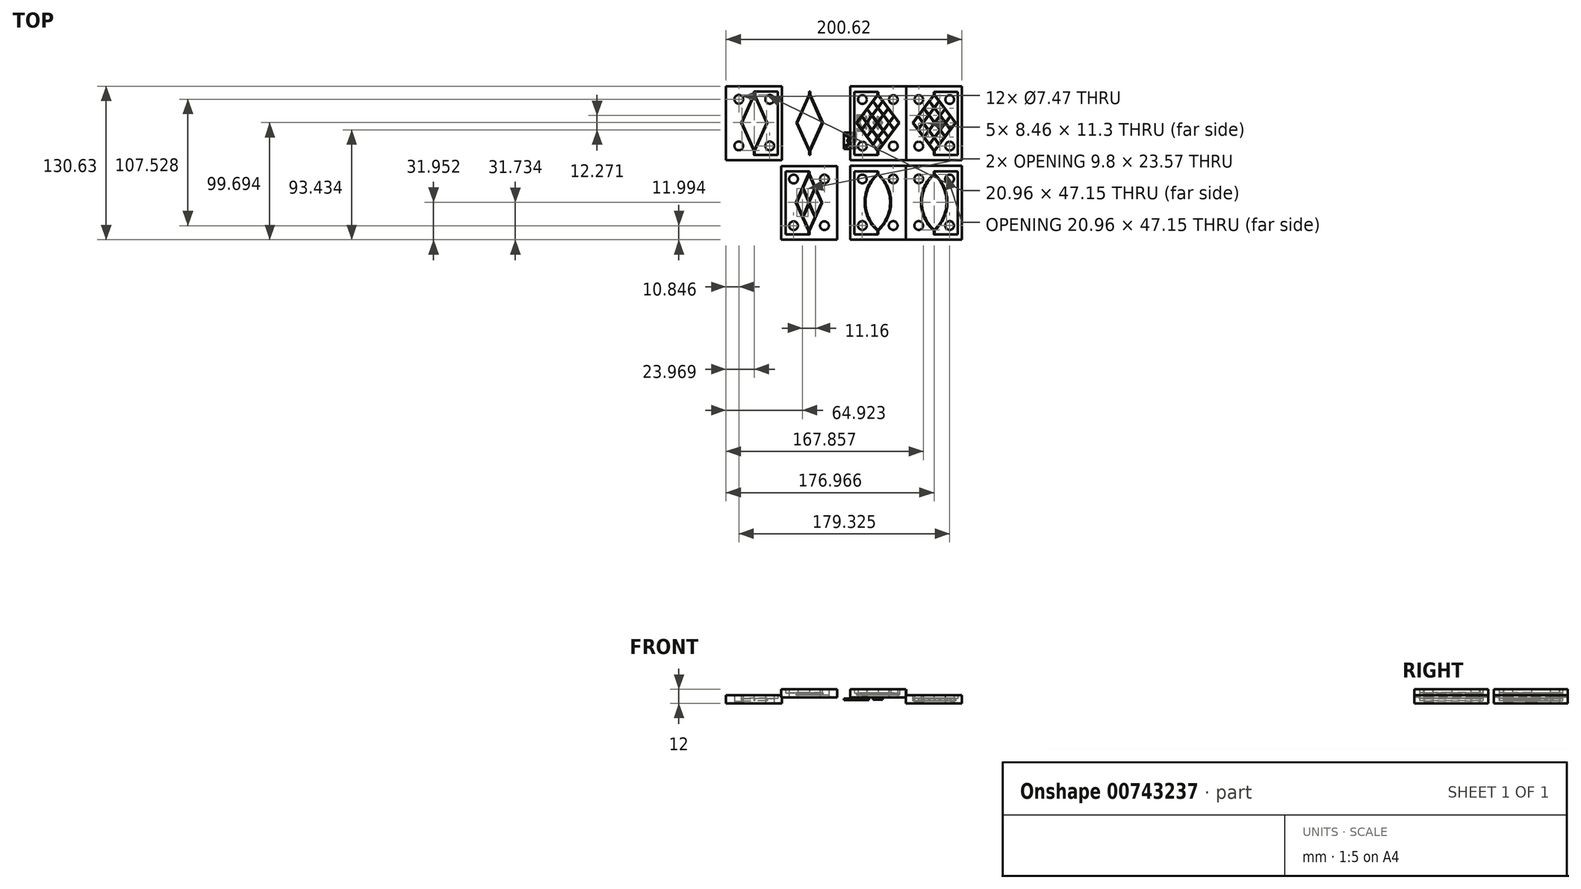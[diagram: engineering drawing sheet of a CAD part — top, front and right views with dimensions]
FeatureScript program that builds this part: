
annotation { "Feature Type Name" : "Feature", "Feature Type Description" : "" }
export const myFeature = defineFeature(function(context is Context, id is Id, definition is map)
    precondition{}
    {
        {
            var Q0;
            Q0=qCreatedBy(makeId("Top.planeOp"),FACE);
            var sketch = newSketch(context, id + "F0", { "sketchPlane" : qUnion([Q0])});
            skLineSegment(sketch, "E0.bottom", {"start": v(-19.96, 26.4) * mm, "end": v(20.09, 26.4) * mm});
            skLineSegment(sketch, "E0.top", {"start": v(-19.96, -27.38) * mm, "end": v(20.09, -27.38) * mm});
            skLineSegment(sketch, "E0.left", {"start": v(-19.96, 26.4) * mm, "end": v(-19.96, -27.38) * mm});
            skLineSegment(sketch, "E0.right", {"start": v(20.09, 26.4) * mm, "end": v(20.09, -27.38) * mm});
            skLineSegment(sketch, "E1.bottom", {"start": v(-23.57, 30.94) * mm, "end": v(23.97, 30.94) * mm});
            skLineSegment(sketch, "E1.top", {"start": v(-23.57, -31.82) * mm, "end": v(23.97, -31.82) * mm});
            skLineSegment(sketch, "E1.left", {"start": v(-23.57, 30.94) * mm, "end": v(-23.57, -31.82) * mm});
            skLineSegment(sketch, "E1.right", {"start": v(23.97, 30.94) * mm, "end": v(23.97, -31.82) * mm});
            skPoint(sketch, "E2.startSnap0", {"position": v(-19.96, -0.48) * mm});
            skLineSegment(sketch, "E3", {"start": v(-13.42, 5.65) * mm, "end": v(-9.19, 11.3) * mm});
            skLineSegment(sketch, "E4", {"start": v(-9.19, 11.3) * mm, "end": v(-5.32, 6.14) * mm});
            skLineSegment(sketch, "E5", {"start": v(-5.32, 6.14) * mm, "end": v(-9.55, 0.48) * mm});
            skLineSegment(sketch, "E6", {"start": v(-17.65, 0) * mm, "end": v(-13.78, 5.17) * mm});
            skLineSegment(sketch, "E7", {"start": v(0, 23.57) * mm, "end": v(-3.87, 18.4) * mm});
            skLineSegment(sketch, "E8", {"start": v(-4.23, 17.92) * mm, "end": v(-8.83, 11.79) * mm});
            skLineSegment(sketch, "E9", {"start": v(-13.78, -5.17) * mm, "end": v(-9.92, 0) * mm});
            skPoint(sketch, "E10.endSnap0", {"position": v(-4.96, 6.62) * mm});
            skLineSegment(sketch, "E11", {"start": v(0, 13.24) * mm, "end": v(3.87, 18.4) * mm});
            skLineSegment(sketch, "E12", {"start": v(-4.96, 6.62) * mm, "end": v(-0.36, 12.76) * mm});
            skLineSegment(sketch, "E13", {"start": v(-13.42, -5.65) * mm, "end": v(-9.55, -0.48) * mm});
            skLineSegment(sketch, "E14", {"start": v(-9.55, -0.48) * mm, "end": v(-5.32, -6.14) * mm});
            skLineSegment(sketch, "E15", {"start": v(-5.32, -6.14) * mm, "end": v(-9.19, -11.3) * mm});
            skLineSegment(sketch, "E16", {"start": v(-9.19, -11.3) * mm, "end": v(-13.42, -5.65) * mm});
            skLineSegment(sketch, "E17", {"start": v(-4.96, -5.65) * mm, "end": v(-0.73, 0) * mm});
            skLineSegment(sketch, "E18", {"start": v(-0.73, 0) * mm, "end": v(-4.96, 5.65) * mm});
            skLineSegment(sketch, "E19", {"start": v(-4.96, 5.65) * mm, "end": v(-9.19, 0) * mm});
            skLineSegment(sketch, "E20", {"start": v(-9.19, 0) * mm, "end": v(-4.96, -5.65) * mm});
            skLineSegment(sketch, "E21", {"start": v(4.23, 6.62) * mm, "end": v(0, 12.27) * mm});
            skLineSegment(sketch, "E22", {"start": v(0, 12.27) * mm, "end": v(-4.6, 6.14) * mm});
            skLineSegment(sketch, "E23", {"start": v(-4.6, 6.14) * mm, "end": v(-0.36, 0.48) * mm});
            skLineSegment(sketch, "E24", {"start": v(-0.36, 0.48) * mm, "end": v(4.23, 6.62) * mm});
            skLineSegment(sketch, "E25", {"start": v(4.6, 7.1) * mm, "end": v(8.46, 12.27) * mm});
            skLineSegment(sketch, "E26", {"start": v(8.46, 12.27) * mm, "end": v(4.23, 17.92) * mm});
            skLineSegment(sketch, "E27", {"start": v(4.23, 17.92) * mm, "end": v(0.36, 12.76) * mm});
            skLineSegment(sketch, "E28", {"start": v(0.36, 12.76) * mm, "end": v(4.6, 7.1) * mm});
            skLineSegment(sketch, "E29", {"start": v(-4.23, -17.92) * mm, "end": v(-0.36, -12.76) * mm});
            skLineSegment(sketch, "E30", {"start": v(-0.36, -12.76) * mm, "end": v(-4.96, -6.62) * mm});
            skLineSegment(sketch, "E31", {"start": v(-8.83, -11.79) * mm, "end": v(-4.96, -6.62) * mm});
            skLineSegment(sketch, "E32", {"start": v(-8.83, -11.79) * mm, "end": v(-4.23, -17.92) * mm});
            skLineSegment(sketch, "E33", {"start": v(0, -12.27) * mm, "end": v(-4.6, -6.14) * mm});
            skLineSegment(sketch, "E34", {"start": v(-0.36, -0.48) * mm, "end": v(-4.6, -6.14) * mm});
            skLineSegment(sketch, "E35", {"start": v(4.23, -6.62) * mm, "end": v(-0.36, -0.48) * mm});
            skLineSegment(sketch, "E36", {"start": v(4.23, -6.62) * mm, "end": v(0, -12.27) * mm});
            skLineSegment(sketch, "E37", {"start": v(9.19, 0) * mm, "end": v(4.6, 6.14) * mm});
            skLineSegment(sketch, "E38", {"start": v(4.6, 6.14) * mm, "end": v(0, 0) * mm});
            skLineSegment(sketch, "E39", {"start": v(0, 0) * mm, "end": v(4.6, -6.14) * mm});
            skLineSegment(sketch, "E40", {"start": v(4.6, -6.14) * mm, "end": v(9.19, 0) * mm});
            skLineSegment(sketch, "E41", {"start": v(4.96, 6.62) * mm, "end": v(8.83, 11.79) * mm});
            skLineSegment(sketch, "E42", {"start": v(8.83, 11.79) * mm, "end": v(13.42, 5.65) * mm});
            skLineSegment(sketch, "E43", {"start": v(13.42, 5.65) * mm, "end": v(9.55, 0.48) * mm});
            skLineSegment(sketch, "E44", {"start": v(9.55, 0.48) * mm, "end": v(4.96, 6.62) * mm});
            skLineSegment(sketch, "E45", {"start": v(-3.87, -18.4) * mm, "end": v(0, -13.24) * mm});
            skLineSegment(sketch, "E46", {"start": v(0, -13.24) * mm, "end": v(3.87, -18.4) * mm});
            skLineSegment(sketch, "E47", {"start": v(3.87, -18.4) * mm, "end": v(0, -23.57) * mm});
            skLineSegment(sketch, "E48", {"start": v(0, -23.57) * mm, "end": v(-3.87, -18.4) * mm});
            skLineSegment(sketch, "E49", {"start": v(4.23, -17.92) * mm, "end": v(8.46, -12.27) * mm});
            skLineSegment(sketch, "E50", {"start": v(8.46, -12.27) * mm, "end": v(4.6, -7.1) * mm});
            skLineSegment(sketch, "E51", {"start": v(4.6, -7.1) * mm, "end": v(0.36, -12.76) * mm});
            skLineSegment(sketch, "E52", {"start": v(0.36, -12.76) * mm, "end": v(4.23, -17.92) * mm});
            skLineSegment(sketch, "E53", {"start": v(8.83, -11.79) * mm, "end": v(4.96, -6.62) * mm});
            skLineSegment(sketch, "E54", {"start": v(4.96, -6.62) * mm, "end": v(9.55, -0.48) * mm});
            skLineSegment(sketch, "E55", {"start": v(9.55, -0.48) * mm, "end": v(13.42, -5.65) * mm});
            skLineSegment(sketch, "E56", {"start": v(13.42, -5.65) * mm, "end": v(8.83, -11.79) * mm});
            skLineSegment(sketch, "E57", {"start": v(17.65, 0) * mm, "end": v(13.78, 5.17) * mm});
            skLineSegment(sketch, "E58", {"start": v(13.78, 5.17) * mm, "end": v(9.92, 0) * mm});
            skLineSegment(sketch, "E59", {"start": v(9.92, 0) * mm, "end": v(13.78, -5.17) * mm});
            skLineSegment(sketch, "E60", {"start": v(13.78, -5.17) * mm, "end": v(17.65, 0) * mm});
            skLineSegment(sketch, "E61", {"start": v(0, 13.24) * mm, "end": v(-3.87, 18.4) * mm});
            skLineSegment(sketch, "E62", {"start": v(3.87, 18.4) * mm, "end": v(0, 23.57) * mm});
            skLineSegment(sketch, "E63", {"start": v(-0.36, 12.76) * mm, "end": v(-4.23, 17.92) * mm});
            skLineSegment(sketch, "E64", {"start": v(-13.78, -5.17) * mm, "end": v(-17.65, 0) * mm});
            skLineSegment(sketch, "E65", {"start": v(-9.92, 0) * mm, "end": v(-13.78, 5.17) * mm});
            skLineSegment(sketch, "E66", {"start": v(-9.55, 0.48) * mm, "end": v(-13.42, 5.65) * mm});
            skLineSegment(sketch, "E67", {"start": v(-4.96, 6.62) * mm, "end": v(-8.83, 11.79) * mm});
            skLineSegment(sketch, "E68", {"start": v(0.36, 24.06) * mm, "end": v(18.38, 0) * mm});
            skLineSegment(sketch, "E69", {"start": v(-18.38, 0) * mm, "end": v(-0.36, 24.06) * mm});
            skLineSegment(sketch, "E70.MirrorCS", {"start": v(-18.38, 0) * mm, "end": v(-0.36, -24.06) * mm});
            skLineSegment(sketch, "E71.MirrorCS", {"start": v(0.36, -24.06) * mm, "end": v(18.38, 0) * mm});
            skLineSegment(sketch, "E72", {"start": v(-0.36, -24.06) * mm, "end": v(-0.36, -27.38) * mm});
            skLineSegment(sketch, "E73", {"start": v(0.36, -24.06) * mm, "end": v(0.36, -27.38) * mm});
            skLineSegment(sketch, "E74", {"start": v(-0.36, 24.06) * mm, "end": v(-0.36, 26.4) * mm});
            skLineSegment(sketch, "E75", {"start": v(0.36, 24.06) * mm, "end": v(0.36, 26.4) * mm});
            skCircle(sketch, "E76", {"center": v(-13.12, 19.83) * mm, "radius": 3.73 * mm});
            skCircle(sketch, "E77.MirrorC", {"center": v(13.12, 19.83) * mm, "radius": 3.73 * mm});
            skCircle(sketch, "E78.MirrorC", {"center": v(-13.12, -19.83) * mm, "radius": 3.73 * mm});
            skCircle(sketch, "E79.MirrorC", {"center": v(13.12, -19.83) * mm, "radius": 3.73 * mm});
            skLineSegment(sketch, "E80.bottom", {"start": v(-77.96, 26.53) * mm, "end": v(-37.9, 26.53) * mm});
            skLineSegment(sketch, "E80.top", {"start": v(-77.96, -27.25) * mm, "end": v(-37.9, -27.25) * mm});
            skLineSegment(sketch, "E80.left", {"start": v(-77.96, 26.53) * mm, "end": v(-77.96, -27.25) * mm});
            skLineSegment(sketch, "E80.right", {"start": v(-37.9, 26.53) * mm, "end": v(-37.9, -27.25) * mm});
            skLineSegment(sketch, "E81.bottom", {"start": v(-81.56, 31.06) * mm, "end": v(-34.02, 31.06) * mm});
            skLineSegment(sketch, "E81.top", {"start": v(-81.56, -31.7) * mm, "end": v(-34.02, -31.7) * mm});
            skLineSegment(sketch, "E81.left", {"start": v(-81.56, 31.06) * mm, "end": v(-81.56, -31.7) * mm});
            skLineSegment(sketch, "E81.right", {"start": v(-34.02, 31.06) * mm, "end": v(-34.02, -31.7) * mm});
            skPoint(sketch, "E82.startSnap0", {"position": v(-77.96, -0.36) * mm});
            skLineSegment(sketch, "E83.MirrorCS", {"start": v(-69.2, -0.05) * mm, "end": v(-58.36, -23.93) * mm});
            skLineSegment(sketch, "E84", {"start": v(-58.36, -23.93) * mm, "end": v(-58.36, -27.25) * mm});
            skLineSegment(sketch, "E85", {"start": v(-57.63, -23.93) * mm, "end": v(-57.63, -27.25) * mm});
            skLineSegment(sketch, "E86", {"start": v(-58.36, 24.18) * mm, "end": v(-58.36, 26.53) * mm});
            skLineSegment(sketch, "E87", {"start": v(-57.63, 24.18) * mm, "end": v(-57.63, 26.53) * mm});
            skCircle(sketch, "E88", {"center": v(-71.12, 19.95) * mm, "radius": 3.73 * mm});
            skCircle(sketch, "E89.MirrorC", {"center": v(-44.87, 19.95) * mm, "radius": 3.73 * mm});
            skCircle(sketch, "E90.MirrorC", {"center": v(-71.12, -19.7) * mm, "radius": 3.73 * mm});
            skCircle(sketch, "E91.MirrorC", {"center": v(-44.87, -19.7) * mm, "radius": 3.73 * mm});
            skLineSegment(sketch, "E92", {"start": v(-69.2, -0.05) * mm, "end": v(-58.36, 24.18) * mm});
            skLineSegment(sketch, "E93.MirrorCS", {"start": v(-46.79, -0.05) * mm, "end": v(-57.63, 24.18) * mm});
            skLineSegment(sketch, "E94.MirrorCS", {"start": v(-47.52, -0.05) * mm, "end": v(-58, 23.7) * mm});
            skLineSegment(sketch, "E95.MirrorCS", {"start": v(-46.79, -0.05) * mm, "end": v(-57.63, -23.93) * mm});
            skLineSegment(sketch, "E96.MirrorCS", {"start": v(-47.52, -0.05) * mm, "end": v(-58, -23.45) * mm});
            skLineSegment(sketch, "E97.MirrorCS", {"start": v(-68.47, -0.05) * mm, "end": v(-58, 23.7) * mm});
            skLineSegment(sketch, "E98.MirrorCS", {"start": v(-68.47, -0.05) * mm, "end": v(-58, -23.45) * mm});
            skLineSegment(sketch, "E99.bottom", {"start": v(-78.56, -41.34) * mm, "end": v(-38.5, -41.34) * mm});
            skLineSegment(sketch, "E99.top", {"start": v(-78.56, -95.12) * mm, "end": v(-38.5, -95.12) * mm});
            skLineSegment(sketch, "E99.left", {"start": v(-78.56, -41.34) * mm, "end": v(-78.56, -95.12) * mm});
            skLineSegment(sketch, "E99.right", {"start": v(-38.5, -41.34) * mm, "end": v(-38.5, -95.12) * mm});
            skLineSegment(sketch, "E100.bottom", {"start": v(-82.17, -36.8) * mm, "end": v(-34.62, -36.8) * mm});
            skLineSegment(sketch, "E100.top", {"start": v(-82.17, -99.57) * mm, "end": v(-34.62, -99.57) * mm});
            skLineSegment(sketch, "E100.left", {"start": v(-82.17, -36.8) * mm, "end": v(-82.17, -99.57) * mm});
            skLineSegment(sketch, "E100.right", {"start": v(-34.62, -36.8) * mm, "end": v(-34.62, -99.57) * mm});
            skPoint(sketch, "E101.startSnap0", {"position": v(-78.56, -68.23) * mm});
            skLineSegment(sketch, "E102.MirrorCS", {"start": v(-69.8, -67.93) * mm, "end": v(-58.96, -91.8) * mm});
            skLineSegment(sketch, "E103", {"start": v(-58.96, -91.8) * mm, "end": v(-58.96, -95.12) * mm});
            skLineSegment(sketch, "E104", {"start": v(-58.23, -91.8) * mm, "end": v(-58.23, -95.12) * mm});
            skLineSegment(sketch, "E105", {"start": v(-58.96, -43.69) * mm, "end": v(-58.96, -41.34) * mm});
            skLineSegment(sketch, "E106", {"start": v(-58.23, -43.69) * mm, "end": v(-58.23, -41.34) * mm});
            skCircle(sketch, "E107", {"center": v(-71.72, -47.92) * mm, "radius": 3.73 * mm});
            skCircle(sketch, "E108.MirrorC", {"center": v(-45.47, -47.92) * mm, "radius": 3.73 * mm});
            skCircle(sketch, "E109.MirrorC", {"center": v(-71.72, -87.58) * mm, "radius": 3.73 * mm});
            skCircle(sketch, "E110.MirrorC", {"center": v(-45.47, -87.58) * mm, "radius": 3.73 * mm});
            skLineSegment(sketch, "E111", {"start": v(-69.8, -67.93) * mm, "end": v(-58.96, -43.69) * mm});
            skLineSegment(sketch, "E112.MirrorCS", {"start": v(-47.4, -67.93) * mm, "end": v(-58.23, -43.69) * mm});
            skLineSegment(sketch, "E113.MirrorCS", {"start": v(-47.4, -67.93) * mm, "end": v(-58.23, -91.8) * mm});
            skLineSegment(sketch, "E114", {"start": v(-58.6, -66.3) * mm, "end": v(-53.68, -55.31) * mm});
            skLineSegment(sketch, "E115", {"start": v(-53.68, -55.31) * mm, "end": v(-58.6, -44.17) * mm});
            skLineSegment(sketch, "E116", {"start": v(-58.6, -66.3) * mm, "end": v(-63.51, -55.31) * mm});
            skLineSegment(sketch, "E117", {"start": v(-63.51, -55.31) * mm, "end": v(-58.6, -44.17) * mm});
            skLineSegment(sketch, "E118", {"start": v(-53.36, -56.05) * mm, "end": v(-48.12, -67.93) * mm});
            skLineSegment(sketch, "E119", {"start": v(-63.84, -56.05) * mm, "end": v(-69.08, -67.93) * mm});
            skLineSegment(sketch, "E120", {"start": v(-58.6, -91.32) * mm, "end": v(-63.51, -80.35) * mm});
            skLineSegment(sketch, "E121", {"start": v(-63.51, -80.35) * mm, "end": v(-58.6, -69.52) * mm});
            skLineSegment(sketch, "E122", {"start": v(-58.6, -69.52) * mm, "end": v(-53.68, -80.35) * mm});
            skLineSegment(sketch, "E123", {"start": v(-53.68, -80.35) * mm, "end": v(-58.6, -91.32) * mm});
            skLineSegment(sketch, "E124", {"start": v(-69.08, -67.93) * mm, "end": v(-63.84, -79.62) * mm});
            skLineSegment(sketch, "E125", {"start": v(-53.36, -79.62) * mm, "end": v(-48.12, -67.93) * mm});
            skLineSegment(sketch, "E126.left", {"start": v(-57.92, -66.3) * mm, "end": v(-57.92, -69.37) * mm});
            skLineSegment(sketch, "E126.right", {"start": v(-59.28, -66.3) * mm, "end": v(-59.28, -69.37) * mm});
            skLineSegment(sketch, "E127", {"start": v(-63.84, -56.05) * mm, "end": v(-59.28, -66.3) * mm});
            skLineSegment(sketch, "E128", {"start": v(-57.92, -66.3) * mm, "end": v(-53.36, -56.05) * mm});
            skLineSegment(sketch, "E129", {"start": v(-57.92, -69.37) * mm, "end": v(-53.36, -79.62) * mm});
            skLineSegment(sketch, "E130", {"start": v(-59.28, -69.37) * mm, "end": v(-63.84, -79.62) * mm});
            skLineSegment(sketch, "E131.bottom", {"start": v(-20.04, -41.21) * mm, "end": v(20, -41.21) * mm});
            skLineSegment(sketch, "E131.top", {"start": v(-20.04, -95) * mm, "end": v(20, -95) * mm});
            skLineSegment(sketch, "E131.left", {"start": v(-20.04, -41.21) * mm, "end": v(-20.04, -95) * mm});
            skLineSegment(sketch, "E131.right", {"start": v(20, -41.21) * mm, "end": v(20, -95) * mm});
            skLineSegment(sketch, "E132.bottom", {"start": v(-23.65, -36.68) * mm, "end": v(23.9, -36.68) * mm});
            skLineSegment(sketch, "E132.top", {"start": v(-23.65, -99.44) * mm, "end": v(23.9, -99.44) * mm});
            skLineSegment(sketch, "E132.left", {"start": v(-23.65, -36.68) * mm, "end": v(-23.65, -99.44) * mm});
            skLineSegment(sketch, "E132.right", {"start": v(23.9, -36.68) * mm, "end": v(23.9, -99.44) * mm});
            skPoint(sketch, "E133.startSnap0", {"position": v(-20.04, -68.1) * mm});
            skLineSegment(sketch, "E134", {"start": v(-0.44, -91.68) * mm, "end": v(-0.44, -95) * mm});
            skLineSegment(sketch, "E135", {"start": v(0.28, -91.68) * mm, "end": v(0.28, -95) * mm});
            skLineSegment(sketch, "E136", {"start": v(-0.44, -43.56) * mm, "end": v(-0.44, -41.21) * mm});
            skLineSegment(sketch, "E137", {"start": v(0.28, -43.56) * mm, "end": v(0.28, -41.21) * mm});
            skCircle(sketch, "E138", {"center": v(-13.2, -47.79) * mm, "radius": 3.73 * mm});
            skCircle(sketch, "E139.MirrorC", {"center": v(13.04, -47.79) * mm, "radius": 3.73 * mm});
            skCircle(sketch, "E140.MirrorC", {"center": v(-13.2, -87.45) * mm, "radius": 3.73 * mm});
            skCircle(sketch, "E141.MirrorC", {"center": v(13.04, -87.45) * mm, "radius": 3.73 * mm});
            skArc(sketch, "E142", {"start": v(-0.44, -43.56) * mm, "mid": v(-11.29, -67.62) * mm, "end": v(-0.44, -91.68) * mm});
            skArc(sketch, "E143", {"start": v(-0.08, -44.04) * mm, "mid": v(-10.56, -67.62) * mm, "end": v(-0.08, -91.2) * mm});
            skArc(sketch, "E144", {"start": v(0.28, -91.68) * mm, "mid": v(11.12, -67.62) * mm, "end": v(0.28, -43.56) * mm});
            skArc(sketch, "E145", {"start": v(-0.08, -91.2) * mm, "mid": v(10.4, -67.62) * mm, "end": v(-0.08, -44.04) * mm});
            skSolve(sketch);
        }
        {
            var Q0;
            Q0=makeQuery(id+"F0.imprint","IMPRINT",FACE,{"disambiguationData":[TD([[makeQuery(id+"F0.imprint","IMPRINT",EDGE,{"derivedFrom":sQuery(id+"F0.wireOp",EDGE,"E3")}),1.0]])]});
            var Q1;
            Q1=makeQuery(id+"F0.imprint","IMPRINT",FACE,{"disambiguationData":[TD([[makeQuery(id+"F0.imprint","IMPRINT",EDGE,{"derivedFrom":sQuery(id+"F0.wireOp",EDGE,"E83.MirrorCS")}),1.0]])]});
            var Q2;
            Q2=makeQuery(id+"F0.imprint","IMPRINT",FACE,{"disambiguationData":[TD([[makeQuery(id+"F0.imprint","IMPRINT",EDGE,{"derivedFrom":sQuery(id+"F0.wireOp",EDGE,"E102.MirrorCS")}),1.0]])]});
            var Q3;
            {var subQ1=sQuery(id+"F0.wireOp",EDGE,"E134");Q3=makeQuery(id+"F0.imprint","IMPRINT",FACE,{"disambiguationData":[TD([[makeQuery(id+"F0.imprint","IMPRINT",EDGE,{"derivedFrom":subQ1}),1.0]])]});}
            extrude(context, id + "F1", {"entities" : qUnion([Q0, Q1, Q2, Q3]), "depth" : .3 * mm, "offsetDistance" : 25 * mm});
        }
        {
            var Q0;
            Q0=makeQuery(id+"F0.imprint","IMPRINT",FACE,{"disambiguationData":[TD([[makeQuery(id+"F0.imprint","IMPRINT",EDGE,{"derivedFrom":sQuery(id+"F0.wireOp",EDGE,"E0.bottom")}),1.0]])]});
            var Q1;
            Q1=makeQuery(id+"F0.imprint","IMPRINT",FACE,{"disambiguationData":[TD([[makeQuery(id+"F0.imprint","IMPRINT",EDGE,{"derivedFrom":sQuery(id+"F0.wireOp",EDGE,"E76")}),1.0]])]});
            var Q2;
            Q2=makeQuery(id+"F0.imprint","IMPRINT",FACE,{"disambiguationData":[TD([[makeQuery(id+"F0.imprint","IMPRINT",EDGE,{"derivedFrom":sQuery(id+"F0.wireOp",EDGE,"edaaeaec-2fa2-4ac8-96e5-24b6cc5294a60.MirrorC")}),-1.0]])]});
            var Q3;
            Q3=makeQuery(id+"F0.imprint","IMPRINT",FACE,{"disambiguationData":[TD([[makeQuery(id+"F0.imprint","IMPRINT",EDGE,{"derivedFrom":sQuery(id+"F0.wireOp",EDGE,"E77.MirrorC")}),-1.0]])]});
            var Q4;
            Q4=makeQuery(id+"F0.imprint","IMPRINT",FACE,{"disambiguationData":[TD([[makeQuery(id+"F0.imprint","IMPRINT",EDGE,{"derivedFrom":sQuery(id+"F0.wireOp",EDGE,"E88")}),1.0]])]});
            var Q5;
            Q5=makeQuery(id+"F0.imprint","IMPRINT",FACE,{"disambiguationData":[TD([[makeQuery(id+"F0.imprint","IMPRINT",EDGE,{"derivedFrom":sQuery(id+"F0.wireOp",EDGE,"E89.MirrorC")}),-1.0]])]});
            var Q6;
            {var subQ1=sQuery(id+"F0.wireOp",EDGE,"E80.left");Q6=makeQuery(id+"F0.imprint","IMPRINT",FACE,{"disambiguationData":[TD([[makeQuery(id+"F0.imprint","IMPRINT",EDGE,{"derivedFrom":subQ1}),-1.0]])]});}
            var Q7;
            Q7=makeQuery(id+"F0.imprint","IMPRINT",FACE,{"disambiguationData":[TD([[makeQuery(id+"F0.imprint","IMPRINT",EDGE,{"derivedFrom":sQuery(id+"F0.wireOp",EDGE,"E107")}),1.0]])]});
            var Q8;
            Q8=makeQuery(id+"F0.imprint","IMPRINT",FACE,{"disambiguationData":[TD([[makeQuery(id+"F0.imprint","IMPRINT",EDGE,{"derivedFrom":sQuery(id+"F0.wireOp",EDGE,"E108.MirrorC")}),-1.0]])]});
            var Q9;
            {var subQ1=sQuery(id+"F0.wireOp",EDGE,"E99.left");Q9=makeQuery(id+"F0.imprint","IMPRINT",FACE,{"disambiguationData":[TD([[makeQuery(id+"F0.imprint","IMPRINT",EDGE,{"derivedFrom":subQ1}),-1.0]])]});}
            var Q10;
            {var subQ1=sQuery(id+"F0.wireOp",EDGE,"E131.left");Q10=makeQuery(id+"F0.imprint","IMPRINT",FACE,{"disambiguationData":[TD([[makeQuery(id+"F0.imprint","IMPRINT",EDGE,{"derivedFrom":subQ1}),-1.0]])]});}
            var Q11;
            Q11=makeQuery(id+"F0.imprint","IMPRINT",FACE,{"disambiguationData":[TD([[makeQuery(id+"F0.imprint","IMPRINT",EDGE,{"derivedFrom":sQuery(id+"F0.wireOp",EDGE,"E138")}),1.0]])]});
            var Q12;
            Q12=makeQuery(id+"F0.imprint","IMPRINT",FACE,{"disambiguationData":[TD([[makeQuery(id+"F0.imprint","IMPRINT",EDGE,{"derivedFrom":sQuery(id+"F0.wireOp",EDGE,"E139.MirrorC")}),-1.0]])]});
            extrude(context, id + "F2", {"entities" : qUnion([Q0, Q1, Q2, Q3, Q4, Q5, Q6, Q7, Q8, Q9, Q10, Q11, Q12]), "depth" : 5 * mm, "offsetDistance" : 25 * mm});
        }
        {
            var Q0;
            {var subQ0=sQuery(id+"F0.wireOp",EDGE,"E0.right");Q0=makeQuery(id+"F0.imprint","IMPRINT",FACE,{"disambiguationData":[TD([[makeQuery(id+"F0.imprint","IMPRINT",EDGE,{"derivedFrom":subQ0}),-1.0]])]});}
            var Q1;
            {var subQ0=sQuery(id+"F0.wireOp",EDGE,"E0.left");Q1=makeQuery(id+"F0.imprint","IMPRINT",FACE,{"disambiguationData":[TD([[makeQuery(id+"F0.imprint","IMPRINT",EDGE,{"derivedFrom":subQ0}),1.0]])]});}
            var Q2;
            {var subQ1=sQuery(id+"F0.wireOp",EDGE,"E131.right");Q2=makeQuery(id+"F0.imprint","IMPRINT",FACE,{"disambiguationData":[TD([[makeQuery(id+"F0.imprint","IMPRINT",EDGE,{"derivedFrom":subQ1}),-1.0]])]});}
            var Q3;
            {var subQ1=sQuery(id+"F0.wireOp",EDGE,"E131.left");Q3=makeQuery(id+"F0.imprint","IMPRINT",FACE,{"disambiguationData":[TD([[makeQuery(id+"F0.imprint","IMPRINT",EDGE,{"derivedFrom":subQ1}),1.0]])]});}
            var Q4;
            Q4=makeQuery(id+"F0.imprint","IMPRINT",FACE,{"disambiguationData":[TD([[makeQuery(id+"F0.imprint","IMPRINT",EDGE,{"derivedFrom":sQuery(id+"F0.wireOp",EDGE,"E143")}),1.0]])]});
            var Q5;
            Q5=makeQuery(id+"F1.opExtrude","CAP_FACE",FACE,{"disambiguationData":[OSD([sQuery(id+"F0.wireOp",EDGE,"E131.bottom"),sQuery(id+"F0.wireOp",EDGE,"E131.top"),sQuery(id+"F0.wireOp",EDGE,"E134"),sQuery(id+"F0.wireOp",EDGE,"E135"),sQuery(id+"F0.wireOp",EDGE,"E136"),sQuery(id+"F0.wireOp",EDGE,"E137"),sQuery(id+"F0.wireOp",EDGE,"E142"),sQuery(id+"F0.wireOp",EDGE,"E143"),sQuery(id+"F0.wireOp",EDGE,"E144"),sQuery(id+"F0.wireOp",EDGE,"E145")])],"isStart":false});
            var Q6;
            {var subQ1=sQuery(id+"F0.wireOp",EDGE,"E99.right");Q6=makeQuery(id+"F0.imprint","IMPRINT",FACE,{"disambiguationData":[TD([[makeQuery(id+"F0.imprint","IMPRINT",EDGE,{"derivedFrom":subQ1}),-1.0]])]});}
            var Q7;
            Q7=makeQuery(id+"F0.imprint","IMPRINT",FACE,{"disambiguationData":[TD([[makeQuery(id+"F0.imprint","IMPRINT",EDGE,{"derivedFrom":sQuery(id+"F0.wireOp",EDGE,"E118")}),-1.0]])]});
            var Q8;
            Q8=makeQuery(id+"F0.imprint","IMPRINT",FACE,{"disambiguationData":[TD([[makeQuery(id+"F0.imprint","IMPRINT",EDGE,{"derivedFrom":sQuery(id+"F0.wireOp",EDGE,"E114")}),1.0]])]});
            var Q9;
            Q9=makeQuery(id+"F0.imprint","IMPRINT",FACE,{"disambiguationData":[TD([[makeQuery(id+"F0.imprint","IMPRINT",EDGE,{"derivedFrom":sQuery(id+"F0.wireOp",EDGE,"E119")}),1.0]])]});
            var Q10;
            Q10=makeQuery(id+"F0.imprint","IMPRINT",FACE,{"disambiguationData":[TD([[makeQuery(id+"F0.imprint","IMPRINT",EDGE,{"derivedFrom":sQuery(id+"F0.wireOp",EDGE,"E120")}),-1.0]])]});
            var Q11;
            {var subQ0=sQuery(id+"F0.wireOp",EDGE,"E99.left");Q11=makeQuery(id+"F0.imprint","IMPRINT",FACE,{"disambiguationData":[TD([[makeQuery(id+"F0.imprint","IMPRINT",EDGE,{"derivedFrom":subQ0}),1.0]])]});}
            var Q12;
            Q12=makeQuery(id+"F1.opExtrude","CAP_FACE",FACE,{"disambiguationData":[OSD([sQuery(id+"F0.wireOp",EDGE,"E99.bottom"),sQuery(id+"F0.wireOp",EDGE,"E99.top"),sQuery(id+"F0.wireOp",EDGE,"E102.MirrorCS"),sQuery(id+"F0.wireOp",EDGE,"E103"),sQuery(id+"F0.wireOp",EDGE,"E104"),sQuery(id+"F0.wireOp",EDGE,"E105"),sQuery(id+"F0.wireOp",EDGE,"E106"),sQuery(id+"F0.wireOp",EDGE,"E111"),sQuery(id+"F0.wireOp",EDGE,"E112.MirrorCS"),sQuery(id+"F0.wireOp",EDGE,"E113.MirrorCS"),sQuery(id+"F0.wireOp",EDGE,"E114"),sQuery(id+"F0.wireOp",EDGE,"E115"),sQuery(id+"F0.wireOp",EDGE,"E116"),sQuery(id+"F0.wireOp",EDGE,"E117"),sQuery(id+"F0.wireOp",EDGE,"E118"),sQuery(id+"F0.wireOp",EDGE,"E119"),sQuery(id+"F0.wireOp",EDGE,"E120"),sQuery(id+"F0.wireOp",EDGE,"E121"),sQuery(id+"F0.wireOp",EDGE,"E122"),sQuery(id+"F0.wireOp",EDGE,"E123"),sQuery(id+"F0.wireOp",EDGE,"E124"),sQuery(id+"F0.wireOp",EDGE,"E125"),sQuery(id+"F0.wireOp",EDGE,"E126.right"),sQuery(id+"F0.wireOp",EDGE,"E126.left"),sQuery(id+"F0.wireOp",EDGE,"E127"),sQuery(id+"F0.wireOp",EDGE,"E128"),sQuery(id+"F0.wireOp",EDGE,"E129"),sQuery(id+"F0.wireOp",EDGE,"E130")])],"isStart":false});
            var Q13;
            {var subQ0=sQuery(id+"F0.wireOp",EDGE,"E80.left");Q13=makeQuery(id+"F0.imprint","IMPRINT",FACE,{"disambiguationData":[TD([[makeQuery(id+"F0.imprint","IMPRINT",EDGE,{"derivedFrom":subQ0}),1.0]])]});}
            var Q14;
            Q14=makeQuery(id+"F1.opExtrude","CAP_FACE",FACE,{"disambiguationData":[OSD([sQuery(id+"F0.wireOp",EDGE,"E80.bottom"),sQuery(id+"F0.wireOp",EDGE,"E80.top"),sQuery(id+"F0.wireOp",EDGE,"E83.MirrorCS"),sQuery(id+"F0.wireOp",EDGE,"E84"),sQuery(id+"F0.wireOp",EDGE,"E85"),sQuery(id+"F0.wireOp",EDGE,"E86"),sQuery(id+"F0.wireOp",EDGE,"E87"),sQuery(id+"F0.wireOp",EDGE,"E92"),sQuery(id+"F0.wireOp",EDGE,"E93.MirrorCS"),sQuery(id+"F0.wireOp",EDGE,"E94.MirrorCS"),sQuery(id+"F0.wireOp",EDGE,"E95.MirrorCS"),sQuery(id+"F0.wireOp",EDGE,"E96.MirrorCS"),sQuery(id+"F0.wireOp",EDGE,"E97.MirrorCS"),sQuery(id+"F0.wireOp",EDGE,"E98.MirrorCS")])],"isStart":false});
            var Q15;
            Q15=makeQuery(id+"F0.imprint","IMPRINT",FACE,{"disambiguationData":[TD([[makeQuery(id+"F0.imprint","IMPRINT",EDGE,{"derivedFrom":sQuery(id+"F0.wireOp",EDGE,"E94.MirrorCS")}),1.0]])]});
            var Q16;
            {var subQ1=sQuery(id+"F0.wireOp",EDGE,"E80.right");Q16=makeQuery(id+"F0.imprint","IMPRINT",FACE,{"disambiguationData":[TD([[makeQuery(id+"F0.imprint","IMPRINT",EDGE,{"derivedFrom":subQ1}),-1.0]])]});}
            var Q17;
            Q17=makeQuery(id+"F0.imprint","IMPRINT",FACE,{"disambiguationData":[TD([[makeQuery(id+"F0.imprint","IMPRINT",EDGE,{"derivedFrom":sQuery(id+"F0.wireOp",EDGE,"E7")}),1.0]])]});
            var Q18;
            Q18=makeQuery(id+"F0.imprint","IMPRINT",FACE,{"disambiguationData":[TD([[makeQuery(id+"F0.imprint","IMPRINT",EDGE,{"derivedFrom":sQuery(id+"F0.wireOp",EDGE,"E8")}),1.0]])]});
            var Q19;
            Q19=makeQuery(id+"F0.imprint","IMPRINT",FACE,{"disambiguationData":[TD([[makeQuery(id+"F0.imprint","IMPRINT",EDGE,{"derivedFrom":sQuery(id+"F0.wireOp",EDGE,"E25")}),1.0]])]});
            var Q20;
            Q20=makeQuery(id+"F0.imprint","IMPRINT",FACE,{"disambiguationData":[TD([[makeQuery(id+"F0.imprint","IMPRINT",EDGE,{"derivedFrom":sQuery(id+"F0.wireOp",EDGE,"E21")}),1.0]])]});
            var Q21;
            Q21=makeQuery(id+"F0.imprint","IMPRINT",FACE,{"disambiguationData":[TD([[makeQuery(id+"F0.imprint","IMPRINT",EDGE,{"derivedFrom":sQuery(id+"F0.wireOp",EDGE,"E41")}),-1.0]])]});
            var Q22;
            Q22=makeQuery(id+"F0.imprint","IMPRINT",FACE,{"disambiguationData":[TD([[makeQuery(id+"F0.imprint","IMPRINT",EDGE,{"derivedFrom":sQuery(id+"F0.wireOp",EDGE,"E37")}),1.0]])]});
            var Q23;
            Q23=makeQuery(id+"F0.imprint","IMPRINT",FACE,{"disambiguationData":[TD([[makeQuery(id+"F0.imprint","IMPRINT",EDGE,{"derivedFrom":sQuery(id+"F0.wireOp",EDGE,"E57")}),1.0]])]});
            var Q24;
            Q24=makeQuery(id+"F0.imprint","IMPRINT",FACE,{"disambiguationData":[TD([[makeQuery(id+"F0.imprint","IMPRINT",EDGE,{"derivedFrom":sQuery(id+"F0.wireOp",EDGE,"E53")}),-1.0]])]});
            var Q25;
            Q25=makeQuery(id+"F0.imprint","IMPRINT",FACE,{"disambiguationData":[TD([[makeQuery(id+"F0.imprint","IMPRINT",EDGE,{"derivedFrom":sQuery(id+"F0.wireOp",EDGE,"E49")}),1.0]])]});
            var Q26;
            Q26=makeQuery(id+"F0.imprint","IMPRINT",FACE,{"disambiguationData":[TD([[makeQuery(id+"F0.imprint","IMPRINT",EDGE,{"derivedFrom":sQuery(id+"F0.wireOp",EDGE,"E33")}),-1.0]])]});
            var Q27;
            Q27=makeQuery(id+"F0.imprint","IMPRINT",FACE,{"disambiguationData":[TD([[makeQuery(id+"F0.imprint","IMPRINT",EDGE,{"derivedFrom":sQuery(id+"F0.wireOp",EDGE,"E45")}),-1.0]])]});
            var Q28;
            Q28=makeQuery(id+"F0.imprint","IMPRINT",FACE,{"disambiguationData":[TD([[makeQuery(id+"F0.imprint","IMPRINT",EDGE,{"derivedFrom":sQuery(id+"F0.wireOp",EDGE,"E29")}),1.0]])]});
            var Q29;
            Q29=makeQuery(id+"F0.imprint","IMPRINT",FACE,{"disambiguationData":[TD([[makeQuery(id+"F0.imprint","IMPRINT",EDGE,{"derivedFrom":sQuery(id+"F0.wireOp",EDGE,"E17")}),1.0]])]});
            var Q30;
            Q30=makeQuery(id+"F0.imprint","IMPRINT",FACE,{"disambiguationData":[TD([[makeQuery(id+"F0.imprint","IMPRINT",EDGE,{"derivedFrom":sQuery(id+"F0.wireOp",EDGE,"E13")}),-1.0]])]});
            var Q31;
            Q31=makeQuery(id+"F0.imprint","IMPRINT",FACE,{"disambiguationData":[TD([[makeQuery(id+"F0.imprint","IMPRINT",EDGE,{"derivedFrom":sQuery(id+"F0.wireOp",EDGE,"E3")}),-1.0]])]});
            var Q32;
            Q32=makeQuery(id+"F1.opExtrude","CAP_FACE",FACE,{"disambiguationData":[OSD([sQuery(id+"F0.wireOp",EDGE,"E0.bottom"),sQuery(id+"F0.wireOp",EDGE,"E0.top"),sQuery(id+"F0.wireOp",EDGE,"E3"),sQuery(id+"F0.wireOp",EDGE,"E4"),sQuery(id+"F0.wireOp",EDGE,"E5"),sQuery(id+"F0.wireOp",EDGE,"E6"),sQuery(id+"F0.wireOp",EDGE,"E7"),sQuery(id+"F0.wireOp",EDGE,"E8"),sQuery(id+"F0.wireOp",EDGE,"E9"),sQuery(id+"F0.wireOp",EDGE,"E11"),sQuery(id+"F0.wireOp",EDGE,"E12"),sQuery(id+"F0.wireOp",EDGE,"E13"),sQuery(id+"F0.wireOp",EDGE,"E14"),sQuery(id+"F0.wireOp",EDGE,"E15"),sQuery(id+"F0.wireOp",EDGE,"E16"),sQuery(id+"F0.wireOp",EDGE,"E17"),sQuery(id+"F0.wireOp",EDGE,"E18"),sQuery(id+"F0.wireOp",EDGE,"E19"),sQuery(id+"F0.wireOp",EDGE,"E20"),sQuery(id+"F0.wireOp",EDGE,"E21"),sQuery(id+"F0.wireOp",EDGE,"E22"),sQuery(id+"F0.wireOp",EDGE,"E23"),sQuery(id+"F0.wireOp",EDGE,"E24"),sQuery(id+"F0.wireOp",EDGE,"E25"),sQuery(id+"F0.wireOp",EDGE,"E26"),sQuery(id+"F0.wireOp",EDGE,"E27"),sQuery(id+"F0.wireOp",EDGE,"E28"),sQuery(id+"F0.wireOp",EDGE,"E29"),sQuery(id+"F0.wireOp",EDGE,"E30"),sQuery(id+"F0.wireOp",EDGE,"E31"),sQuery(id+"F0.wireOp",EDGE,"E32"),sQuery(id+"F0.wireOp",EDGE,"E33"),sQuery(id+"F0.wireOp",EDGE,"E34"),sQuery(id+"F0.wireOp",EDGE,"E35"),sQuery(id+"F0.wireOp",EDGE,"E36"),sQuery(id+"F0.wireOp",EDGE,"E37"),sQuery(id+"F0.wireOp",EDGE,"E38"),sQuery(id+"F0.wireOp",EDGE,"E39"),sQuery(id+"F0.wireOp",EDGE,"E40"),sQuery(id+"F0.wireOp",EDGE,"E41"),sQuery(id+"F0.wireOp",EDGE,"E42"),sQuery(id+"F0.wireOp",EDGE,"E43"),sQuery(id+"F0.wireOp",EDGE,"E44"),sQuery(id+"F0.wireOp",EDGE,"E45"),sQuery(id+"F0.wireOp",EDGE,"E46"),sQuery(id+"F0.wireOp",EDGE,"E47"),sQuery(id+"F0.wireOp",EDGE,"E48"),sQuery(id+"F0.wireOp",EDGE,"E49"),sQuery(id+"F0.wireOp",EDGE,"E50"),sQuery(id+"F0.wireOp",EDGE,"E51"),sQuery(id+"F0.wireOp",EDGE,"E52"),sQuery(id+"F0.wireOp",EDGE,"E53"),sQuery(id+"F0.wireOp",EDGE,"E54"),sQuery(id+"F0.wireOp",EDGE,"E55"),sQuery(id+"F0.wireOp",EDGE,"E56"),sQuery(id+"F0.wireOp",EDGE,"E57"),sQuery(id+"F0.wireOp",EDGE,"E58"),sQuery(id+"F0.wireOp",EDGE,"E59"),sQuery(id+"F0.wireOp",EDGE,"E60"),sQuery(id+"F0.wireOp",EDGE,"E61"),sQuery(id+"F0.wireOp",EDGE,"E62"),sQuery(id+"F0.wireOp",EDGE,"E63"),sQuery(id+"F0.wireOp",EDGE,"E64"),sQuery(id+"F0.wireOp",EDGE,"E65"),sQuery(id+"F0.wireOp",EDGE,"E66"),sQuery(id+"F0.wireOp",EDGE,"E67"),sQuery(id+"F0.wireOp",EDGE,"E68"),sQuery(id+"F0.wireOp",EDGE,"E69"),sQuery(id+"F0.wireOp",EDGE,"E70.MirrorCS"),sQuery(id+"F0.wireOp",EDGE,"E71.MirrorCS"),sQuery(id+"F0.wireOp",EDGE,"E72"),sQuery(id+"F0.wireOp",EDGE,"E73"),sQuery(id+"F0.wireOp",EDGE,"E74"),sQuery(id+"F0.wireOp",EDGE,"E75")])],"isStart":false});
            extrude(context, id + "F3", {"entities" : qUnion([Q0, Q1, Q2, Q3, Q4, Q5, Q6, Q7, Q8, Q9, Q10, Q11, Q12, Q13, Q14, Q15, Q16, Q17, Q18, Q19, Q20, Q21, Q22, Q23, Q24, Q25, Q26, Q27, Q28, Q29, Q30, Q31, Q32]), "depth" : 2 * mm, "offsetDistance" : 25 * mm});
        }
        {
            var Q0;
            {var subQ0=sQuery(id+"F0.wireOp",EDGE,"E72");Q0=makeQuery(id+"F3.opExtrude","CAP_EDGE",EDGE,{"disambiguationData":[OSD([subQ0]),TDD([makeQuery(id+"F1.opExtrude","CAP_EDGE",EDGE,{"disambiguationData":[OSD([subQ0])],"isStart":false})])],"isStart":false});}
            var Q1;
            {var subQ0=sQuery(id+"F0.wireOp",EDGE,"E73");Q1=makeQuery(id+"F3.opExtrude","CAP_EDGE",EDGE,{"disambiguationData":[OSD([subQ0]),TDD([makeQuery(id+"F1.opExtrude","CAP_EDGE",EDGE,{"disambiguationData":[OSD([subQ0])],"isStart":false})])],"isStart":false});}
            var Q2;
            {var subQ0=sQuery(id+"F0.wireOp",EDGE,"E70.MirrorCS");Q2=makeQuery(id+"F3.opExtrude","CAP_EDGE",EDGE,{"disambiguationData":[OSD([subQ0]),TDD([makeQuery(id+"F1.opExtrude","CAP_EDGE",EDGE,{"disambiguationData":[OSD([subQ0])],"isStart":false})])],"isStart":false});}
            var Q3;
            {var subQ0=sQuery(id+"F0.wireOp",EDGE,"E71.MirrorCS");Q3=makeQuery(id+"F3.opExtrude","CAP_EDGE",EDGE,{"disambiguationData":[OSD([subQ0]),TDD([makeQuery(id+"F1.opExtrude","CAP_EDGE",EDGE,{"disambiguationData":[OSD([subQ0])],"isStart":false})])],"isStart":false});}
            var Q4;
            {var subQ0=sQuery(id+"F0.wireOp",EDGE,"E47");Q4=makeQuery(id+"F3.opExtrude","CAP_EDGE",EDGE,{"disambiguationData":[OSD([subQ0]),TDD([makeQuery(id+"F1.opExtrude","CAP_EDGE",EDGE,{"disambiguationData":[OSD([subQ0])],"isStart":false})])],"isStart":false});}
            var Q5;
            {var subQ0=sQuery(id+"F0.wireOp",EDGE,"E48");Q5=makeQuery(id+"F3.opExtrude","CAP_EDGE",EDGE,{"disambiguationData":[OSD([subQ0]),TDD([makeQuery(id+"F1.opExtrude","CAP_EDGE",EDGE,{"disambiguationData":[OSD([subQ0])],"isStart":false})])],"isStart":false});}
            var Q6;
            {var subQ0=sQuery(id+"F0.wireOp",EDGE,"E46");Q6=makeQuery(id+"F3.opExtrude","CAP_EDGE",EDGE,{"disambiguationData":[OSD([subQ0]),TDD([makeQuery(id+"F1.opExtrude","CAP_EDGE",EDGE,{"disambiguationData":[OSD([subQ0])],"isStart":false})])],"isStart":false});}
            var Q7;
            {var subQ0=sQuery(id+"F0.wireOp",EDGE,"E45");Q7=makeQuery(id+"F3.opExtrude","CAP_EDGE",EDGE,{"disambiguationData":[OSD([subQ0]),TDD([makeQuery(id+"F1.opExtrude","CAP_EDGE",EDGE,{"disambiguationData":[OSD([subQ0])],"isStart":false})])],"isStart":false});}
            var Q8;
            {var subQ0=sQuery(id+"F0.wireOp",EDGE,"E52");Q8=makeQuery(id+"F3.opExtrude","CAP_EDGE",EDGE,{"disambiguationData":[OSD([subQ0]),TDD([makeQuery(id+"F1.opExtrude","CAP_EDGE",EDGE,{"disambiguationData":[OSD([subQ0])],"isStart":false})])],"isStart":false});}
            var Q9;
            {var subQ0=sQuery(id+"F0.wireOp",EDGE,"E49");Q9=makeQuery(id+"F3.opExtrude","CAP_EDGE",EDGE,{"disambiguationData":[OSD([subQ0]),TDD([makeQuery(id+"F1.opExtrude","CAP_EDGE",EDGE,{"disambiguationData":[OSD([subQ0])],"isStart":false})])],"isStart":false});}
            var Q10;
            {var subQ0=sQuery(id+"F0.wireOp",EDGE,"E50");Q10=makeQuery(id+"F3.opExtrude","CAP_EDGE",EDGE,{"disambiguationData":[OSD([subQ0]),TDD([makeQuery(id+"F1.opExtrude","CAP_EDGE",EDGE,{"disambiguationData":[OSD([subQ0])],"isStart":false})])],"isStart":false});}
            var Q11;
            {var subQ0=sQuery(id+"F0.wireOp",EDGE,"E51");Q11=makeQuery(id+"F3.opExtrude","CAP_EDGE",EDGE,{"disambiguationData":[OSD([subQ0]),TDD([makeQuery(id+"F1.opExtrude","CAP_EDGE",EDGE,{"disambiguationData":[OSD([subQ0])],"isStart":false})])],"isStart":false});}
            var Q12;
            {var subQ0=sQuery(id+"F0.wireOp",EDGE,"E56");Q12=makeQuery(id+"F3.opExtrude","CAP_EDGE",EDGE,{"disambiguationData":[OSD([subQ0]),TDD([makeQuery(id+"F1.opExtrude","CAP_EDGE",EDGE,{"disambiguationData":[OSD([subQ0])],"isStart":false})])],"isStart":false});}
            var Q13;
            {var subQ0=sQuery(id+"F0.wireOp",EDGE,"E55");Q13=makeQuery(id+"F3.opExtrude","CAP_EDGE",EDGE,{"disambiguationData":[OSD([subQ0]),TDD([makeQuery(id+"F1.opExtrude","CAP_EDGE",EDGE,{"disambiguationData":[OSD([subQ0])],"isStart":false})])],"isStart":false});}
            var Q14;
            {var subQ0=sQuery(id+"F0.wireOp",EDGE,"E53");Q14=makeQuery(id+"F3.opExtrude","CAP_EDGE",EDGE,{"disambiguationData":[OSD([subQ0]),TDD([makeQuery(id+"F1.opExtrude","CAP_EDGE",EDGE,{"disambiguationData":[OSD([subQ0])],"isStart":false})])],"isStart":false});}
            var Q15;
            {var subQ0=sQuery(id+"F0.wireOp",EDGE,"E54");Q15=makeQuery(id+"F3.opExtrude","CAP_EDGE",EDGE,{"disambiguationData":[OSD([subQ0]),TDD([makeQuery(id+"F1.opExtrude","CAP_EDGE",EDGE,{"disambiguationData":[OSD([subQ0])],"isStart":false})])],"isStart":false});}
            var Q16;
            {var subQ0=sQuery(id+"F0.wireOp",EDGE,"E68");Q16=makeQuery(id+"F3.opExtrude","CAP_EDGE",EDGE,{"disambiguationData":[OSD([subQ0]),TDD([makeQuery(id+"F1.opExtrude","CAP_EDGE",EDGE,{"disambiguationData":[OSD([subQ0])],"isStart":false})])],"isStart":false});}
            var Q17;
            {var subQ0=sQuery(id+"F0.wireOp",EDGE,"E57");Q17=makeQuery(id+"F3.opExtrude","CAP_EDGE",EDGE,{"disambiguationData":[OSD([subQ0]),TDD([makeQuery(id+"F1.opExtrude","CAP_EDGE",EDGE,{"disambiguationData":[OSD([subQ0])],"isStart":false})])],"isStart":false});}
            var Q18;
            {var subQ0=sQuery(id+"F0.wireOp",EDGE,"E60");Q18=makeQuery(id+"F3.opExtrude","CAP_EDGE",EDGE,{"disambiguationData":[OSD([subQ0]),TDD([makeQuery(id+"F1.opExtrude","CAP_EDGE",EDGE,{"disambiguationData":[OSD([subQ0])],"isStart":false})])],"isStart":false});}
            var Q19;
            {var subQ0=sQuery(id+"F0.wireOp",EDGE,"E59");Q19=makeQuery(id+"F3.opExtrude","CAP_EDGE",EDGE,{"disambiguationData":[OSD([subQ0]),TDD([makeQuery(id+"F1.opExtrude","CAP_EDGE",EDGE,{"disambiguationData":[OSD([subQ0])],"isStart":false})])],"isStart":false});}
            var Q20;
            {var subQ0=sQuery(id+"F0.wireOp",EDGE,"E58");Q20=makeQuery(id+"F3.opExtrude","CAP_EDGE",EDGE,{"disambiguationData":[OSD([subQ0]),TDD([makeQuery(id+"F1.opExtrude","CAP_EDGE",EDGE,{"disambiguationData":[OSD([subQ0])],"isStart":false})])],"isStart":false});}
            var Q21;
            {var subQ0=sQuery(id+"F0.wireOp",EDGE,"E43");Q21=makeQuery(id+"F3.opExtrude","CAP_EDGE",EDGE,{"disambiguationData":[OSD([subQ0]),TDD([makeQuery(id+"F1.opExtrude","CAP_EDGE",EDGE,{"disambiguationData":[OSD([subQ0])],"isStart":false})])],"isStart":false});}
            var Q22;
            {var subQ0=sQuery(id+"F0.wireOp",EDGE,"E44");Q22=makeQuery(id+"F3.opExtrude","CAP_EDGE",EDGE,{"disambiguationData":[OSD([subQ0]),TDD([makeQuery(id+"F1.opExtrude","CAP_EDGE",EDGE,{"disambiguationData":[OSD([subQ0])],"isStart":false})])],"isStart":false});}
            var Q23;
            {var subQ0=sQuery(id+"F0.wireOp",EDGE,"E37");Q23=makeQuery(id+"F3.opExtrude","CAP_EDGE",EDGE,{"disambiguationData":[OSD([subQ0]),TDD([makeQuery(id+"F1.opExtrude","CAP_EDGE",EDGE,{"disambiguationData":[OSD([subQ0])],"isStart":false})])],"isStart":false});}
            var Q24;
            {var subQ0=sQuery(id+"F0.wireOp",EDGE,"E40");Q24=makeQuery(id+"F3.opExtrude","CAP_EDGE",EDGE,{"disambiguationData":[OSD([subQ0]),TDD([makeQuery(id+"F1.opExtrude","CAP_EDGE",EDGE,{"disambiguationData":[OSD([subQ0])],"isStart":false})])],"isStart":false});}
            var Q25;
            {var subQ0=sQuery(id+"F0.wireOp",EDGE,"E38");Q25=makeQuery(id+"F3.opExtrude","CAP_EDGE",EDGE,{"disambiguationData":[OSD([subQ0]),TDD([makeQuery(id+"F1.opExtrude","CAP_EDGE",EDGE,{"disambiguationData":[OSD([subQ0])],"isStart":false})])],"isStart":false});}
            var Q26;
            {var subQ0=sQuery(id+"F0.wireOp",EDGE,"E39");Q26=makeQuery(id+"F3.opExtrude","CAP_EDGE",EDGE,{"disambiguationData":[OSD([subQ0]),TDD([makeQuery(id+"F1.opExtrude","CAP_EDGE",EDGE,{"disambiguationData":[OSD([subQ0])],"isStart":false})])],"isStart":false});}
            var Q27;
            {var subQ0=sQuery(id+"F0.wireOp",EDGE,"E25");Q27=makeQuery(id+"F3.opExtrude","CAP_EDGE",EDGE,{"disambiguationData":[OSD([subQ0]),TDD([makeQuery(id+"F1.opExtrude","CAP_EDGE",EDGE,{"disambiguationData":[OSD([subQ0])],"isStart":false})])],"isStart":false});}
            var Q28;
            {var subQ0=sQuery(id+"F0.wireOp",EDGE,"E26");Q28=makeQuery(id+"F3.opExtrude","CAP_EDGE",EDGE,{"disambiguationData":[OSD([subQ0]),TDD([makeQuery(id+"F1.opExtrude","CAP_EDGE",EDGE,{"disambiguationData":[OSD([subQ0])],"isStart":false})])],"isStart":false});}
            var Q29;
            {var subQ0=sQuery(id+"F0.wireOp",EDGE,"E27");Q29=makeQuery(id+"F3.opExtrude","CAP_EDGE",EDGE,{"disambiguationData":[OSD([subQ0]),TDD([makeQuery(id+"F1.opExtrude","CAP_EDGE",EDGE,{"disambiguationData":[OSD([subQ0])],"isStart":false})])],"isStart":false});}
            var Q30;
            {var subQ0=sQuery(id+"F0.wireOp",EDGE,"E28");Q30=makeQuery(id+"F3.opExtrude","CAP_EDGE",EDGE,{"disambiguationData":[OSD([subQ0]),TDD([makeQuery(id+"F1.opExtrude","CAP_EDGE",EDGE,{"disambiguationData":[OSD([subQ0])],"isStart":false})])],"isStart":false});}
            var Q31;
            {var subQ0=sQuery(id+"F0.wireOp",EDGE,"E24");Q31=makeQuery(id+"F3.opExtrude","CAP_EDGE",EDGE,{"disambiguationData":[OSD([subQ0]),TDD([makeQuery(id+"F1.opExtrude","CAP_EDGE",EDGE,{"disambiguationData":[OSD([subQ0])],"isStart":false})])],"isStart":false});}
            var Q32;
            {var subQ0=sQuery(id+"F0.wireOp",EDGE,"E21");Q32=makeQuery(id+"F3.opExtrude","CAP_EDGE",EDGE,{"disambiguationData":[OSD([subQ0]),TDD([makeQuery(id+"F1.opExtrude","CAP_EDGE",EDGE,{"disambiguationData":[OSD([subQ0])],"isStart":false})])],"isStart":false});}
            var Q33;
            {var subQ0=sQuery(id+"F0.wireOp",EDGE,"E22");Q33=makeQuery(id+"F3.opExtrude","CAP_EDGE",EDGE,{"disambiguationData":[OSD([subQ0]),TDD([makeQuery(id+"F1.opExtrude","CAP_EDGE",EDGE,{"disambiguationData":[OSD([subQ0])],"isStart":false})])],"isStart":false});}
            var Q34;
            {var subQ0=sQuery(id+"F0.wireOp",EDGE,"E23");Q34=makeQuery(id+"F3.opExtrude","CAP_EDGE",EDGE,{"disambiguationData":[OSD([subQ0]),TDD([makeQuery(id+"F1.opExtrude","CAP_EDGE",EDGE,{"disambiguationData":[OSD([subQ0])],"isStart":false})])],"isStart":false});}
            var Q35;
            {var subQ0=sQuery(id+"F0.wireOp",EDGE,"E17");Q35=makeQuery(id+"F3.opExtrude","CAP_EDGE",EDGE,{"disambiguationData":[OSD([subQ0]),TDD([makeQuery(id+"F1.opExtrude","CAP_EDGE",EDGE,{"disambiguationData":[OSD([subQ0])],"isStart":false})])],"isStart":false});}
            var Q36;
            {var subQ0=sQuery(id+"F0.wireOp",EDGE,"E18");Q36=makeQuery(id+"F3.opExtrude","CAP_EDGE",EDGE,{"disambiguationData":[OSD([subQ0]),TDD([makeQuery(id+"F1.opExtrude","CAP_EDGE",EDGE,{"disambiguationData":[OSD([subQ0])],"isStart":false})])],"isStart":false});}
            var Q37;
            {var subQ0=sQuery(id+"F0.wireOp",EDGE,"E19");Q37=makeQuery(id+"F3.opExtrude","CAP_EDGE",EDGE,{"disambiguationData":[OSD([subQ0]),TDD([makeQuery(id+"F1.opExtrude","CAP_EDGE",EDGE,{"disambiguationData":[OSD([subQ0])],"isStart":false})])],"isStart":false});}
            var Q38;
            {var subQ0=sQuery(id+"F0.wireOp",EDGE,"E20");Q38=makeQuery(id+"F3.opExtrude","CAP_EDGE",EDGE,{"disambiguationData":[OSD([subQ0]),TDD([makeQuery(id+"F1.opExtrude","CAP_EDGE",EDGE,{"disambiguationData":[OSD([subQ0])],"isStart":false})])],"isStart":false});}
            var Q39;
            {var subQ0=sQuery(id+"F0.wireOp",EDGE,"E15");Q39=makeQuery(id+"F3.opExtrude","CAP_EDGE",EDGE,{"disambiguationData":[OSD([subQ0]),TDD([makeQuery(id+"F1.opExtrude","CAP_EDGE",EDGE,{"disambiguationData":[OSD([subQ0])],"isStart":false})])],"isStart":false});}
            var Q40;
            {var subQ0=sQuery(id+"F0.wireOp",EDGE,"E16");Q40=makeQuery(id+"F3.opExtrude","CAP_EDGE",EDGE,{"disambiguationData":[OSD([subQ0]),TDD([makeQuery(id+"F1.opExtrude","CAP_EDGE",EDGE,{"disambiguationData":[OSD([subQ0])],"isStart":false})])],"isStart":false});}
            var Q41;
            {var subQ0=sQuery(id+"F0.wireOp",EDGE,"E14");Q41=makeQuery(id+"F3.opExtrude","CAP_EDGE",EDGE,{"disambiguationData":[OSD([subQ0]),TDD([makeQuery(id+"F1.opExtrude","CAP_EDGE",EDGE,{"disambiguationData":[OSD([subQ0])],"isStart":false})])],"isStart":false});}
            var Q42;
            {var subQ0=sQuery(id+"F0.wireOp",EDGE,"E13");Q42=makeQuery(id+"F3.opExtrude","CAP_EDGE",EDGE,{"disambiguationData":[OSD([subQ0]),TDD([makeQuery(id+"F1.opExtrude","CAP_EDGE",EDGE,{"disambiguationData":[OSD([subQ0])],"isStart":false})])],"isStart":false});}
            var Q43;
            {var subQ0=sQuery(id+"F0.wireOp",EDGE,"E9");Q43=makeQuery(id+"F3.opExtrude","CAP_EDGE",EDGE,{"disambiguationData":[OSD([subQ0]),TDD([makeQuery(id+"F1.opExtrude","CAP_EDGE",EDGE,{"disambiguationData":[OSD([subQ0])],"isStart":false})])],"isStart":false});}
            var Q44;
            {var subQ0=sQuery(id+"F0.wireOp",EDGE,"E64");Q44=makeQuery(id+"F3.opExtrude","CAP_EDGE",EDGE,{"disambiguationData":[OSD([subQ0]),TDD([makeQuery(id+"F1.opExtrude","CAP_EDGE",EDGE,{"disambiguationData":[OSD([subQ0])],"isStart":false})])],"isStart":false});}
            var Q45;
            {var subQ0=sQuery(id+"F0.wireOp",EDGE,"E65");Q45=makeQuery(id+"F3.opExtrude","CAP_EDGE",EDGE,{"disambiguationData":[OSD([subQ0]),TDD([makeQuery(id+"F1.opExtrude","CAP_EDGE",EDGE,{"disambiguationData":[OSD([subQ0])],"isStart":false})])],"isStart":false});}
            var Q46;
            {var subQ0=sQuery(id+"F0.wireOp",EDGE,"E6");Q46=makeQuery(id+"F3.opExtrude","CAP_EDGE",EDGE,{"disambiguationData":[OSD([subQ0]),TDD([makeQuery(id+"F1.opExtrude","CAP_EDGE",EDGE,{"disambiguationData":[OSD([subQ0])],"isStart":false})])],"isStart":false});}
            var Q47;
            {var subQ0=sQuery(id+"F0.wireOp",EDGE,"E66");Q47=makeQuery(id+"F3.opExtrude","CAP_EDGE",EDGE,{"disambiguationData":[OSD([subQ0]),TDD([makeQuery(id+"F1.opExtrude","CAP_EDGE",EDGE,{"disambiguationData":[OSD([subQ0])],"isStart":false})])],"isStart":false});}
            var Q48;
            {var subQ0=sQuery(id+"F0.wireOp",EDGE,"E3");Q48=makeQuery(id+"F3.opExtrude","CAP_EDGE",EDGE,{"disambiguationData":[OSD([subQ0]),TDD([makeQuery(id+"F1.opExtrude","CAP_EDGE",EDGE,{"disambiguationData":[OSD([subQ0])],"isStart":false})])],"isStart":false});}
            var Q49;
            {var subQ0=sQuery(id+"F0.wireOp",EDGE,"E4");Q49=makeQuery(id+"F3.opExtrude","CAP_EDGE",EDGE,{"disambiguationData":[OSD([subQ0]),TDD([makeQuery(id+"F1.opExtrude","CAP_EDGE",EDGE,{"disambiguationData":[OSD([subQ0])],"isStart":false})])],"isStart":false});}
            var Q50;
            {var subQ0=sQuery(id+"F0.wireOp",EDGE,"E5");Q50=makeQuery(id+"F3.opExtrude","CAP_EDGE",EDGE,{"disambiguationData":[OSD([subQ0]),TDD([makeQuery(id+"F1.opExtrude","CAP_EDGE",EDGE,{"disambiguationData":[OSD([subQ0])],"isStart":false})])],"isStart":false});}
            var Q51;
            {var subQ0=sQuery(id+"F0.wireOp",EDGE,"E63");Q51=makeQuery(id+"F3.opExtrude","CAP_EDGE",EDGE,{"disambiguationData":[OSD([subQ0]),TDD([makeQuery(id+"F1.opExtrude","CAP_EDGE",EDGE,{"disambiguationData":[OSD([subQ0])],"isStart":false})])],"isStart":false});}
            var Q52;
            {var subQ0=sQuery(id+"F0.wireOp",EDGE,"E12");Q52=makeQuery(id+"F3.opExtrude","CAP_EDGE",EDGE,{"disambiguationData":[OSD([subQ0]),TDD([makeQuery(id+"F1.opExtrude","CAP_EDGE",EDGE,{"disambiguationData":[OSD([subQ0])],"isStart":false})])],"isStart":false});}
            var Q53;
            {var subQ0=sQuery(id+"F0.wireOp",EDGE,"E8");Q53=makeQuery(id+"F3.opExtrude","CAP_EDGE",EDGE,{"disambiguationData":[OSD([subQ0]),TDD([makeQuery(id+"F1.opExtrude","CAP_EDGE",EDGE,{"disambiguationData":[OSD([subQ0])],"isStart":false})])],"isStart":false});}
            var Q54;
            {var subQ0=sQuery(id+"F0.wireOp",EDGE,"E67");Q54=makeQuery(id+"F3.opExtrude","CAP_EDGE",EDGE,{"disambiguationData":[OSD([subQ0]),TDD([makeQuery(id+"F1.opExtrude","CAP_EDGE",EDGE,{"disambiguationData":[OSD([subQ0])],"isStart":false})])],"isStart":false});}
            var Q55;
            {var subQ0=sQuery(id+"F0.wireOp",EDGE,"E75");Q55=makeQuery(id+"F3.opExtrude","CAP_EDGE",EDGE,{"disambiguationData":[OSD([subQ0]),TDD([makeQuery(id+"F1.opExtrude","CAP_EDGE",EDGE,{"disambiguationData":[OSD([subQ0])],"isStart":false})])],"isStart":false});}
            var Q56;
            {var subQ0=sQuery(id+"F0.wireOp",EDGE,"E74");Q56=makeQuery(id+"F3.opExtrude","CAP_EDGE",EDGE,{"disambiguationData":[OSD([subQ0]),TDD([makeQuery(id+"F1.opExtrude","CAP_EDGE",EDGE,{"disambiguationData":[OSD([subQ0])],"isStart":false})])],"isStart":false});}
            var Q57;
            {var subQ0=sQuery(id+"F0.wireOp",EDGE,"E7");Q57=makeQuery(id+"F3.opExtrude","CAP_EDGE",EDGE,{"disambiguationData":[OSD([subQ0]),TDD([makeQuery(id+"F1.opExtrude","CAP_EDGE",EDGE,{"disambiguationData":[OSD([subQ0])],"isStart":false})])],"isStart":false});}
            var Q58;
            {var subQ0=sQuery(id+"F0.wireOp",EDGE,"E69");Q58=makeQuery(id+"F3.opExtrude","CAP_EDGE",EDGE,{"disambiguationData":[OSD([subQ0]),TDD([makeQuery(id+"F1.opExtrude","CAP_EDGE",EDGE,{"disambiguationData":[OSD([subQ0])],"isStart":false})])],"isStart":false});}
            var Q59;
            {var subQ0=sQuery(id+"F0.wireOp",EDGE,"E62");Q59=makeQuery(id+"F3.opExtrude","CAP_EDGE",EDGE,{"disambiguationData":[OSD([subQ0]),TDD([makeQuery(id+"F1.opExtrude","CAP_EDGE",EDGE,{"disambiguationData":[OSD([subQ0])],"isStart":false})])],"isStart":false});}
            var Q60;
            {var subQ0=sQuery(id+"F0.wireOp",EDGE,"E61");Q60=makeQuery(id+"F3.opExtrude","CAP_EDGE",EDGE,{"disambiguationData":[OSD([subQ0]),TDD([makeQuery(id+"F1.opExtrude","CAP_EDGE",EDGE,{"disambiguationData":[OSD([subQ0])],"isStart":false})])],"isStart":false});}
            var Q61;
            {var subQ0=sQuery(id+"F0.wireOp",EDGE,"E11");Q61=makeQuery(id+"F3.opExtrude","CAP_EDGE",EDGE,{"disambiguationData":[OSD([subQ0]),TDD([makeQuery(id+"F1.opExtrude","CAP_EDGE",EDGE,{"disambiguationData":[OSD([subQ0])],"isStart":false})])],"isStart":false});}
            var Q62;
            {var subQ0=sQuery(id+"F0.wireOp",EDGE,"E32");Q62=makeQuery(id+"F3.opExtrude","CAP_EDGE",EDGE,{"disambiguationData":[OSD([subQ0]),TDD([makeQuery(id+"F1.opExtrude","CAP_EDGE",EDGE,{"disambiguationData":[OSD([subQ0])],"isStart":false})])],"isStart":false});}
            var Q63;
            {var subQ0=sQuery(id+"F0.wireOp",EDGE,"E30");Q63=makeQuery(id+"F3.opExtrude","CAP_EDGE",EDGE,{"disambiguationData":[OSD([subQ0]),TDD([makeQuery(id+"F1.opExtrude","CAP_EDGE",EDGE,{"disambiguationData":[OSD([subQ0])],"isStart":false})])],"isStart":false});}
            var Q64;
            {var subQ0=sQuery(id+"F0.wireOp",EDGE,"E31");Q64=makeQuery(id+"F3.opExtrude","CAP_EDGE",EDGE,{"disambiguationData":[OSD([subQ0]),TDD([makeQuery(id+"F1.opExtrude","CAP_EDGE",EDGE,{"disambiguationData":[OSD([subQ0])],"isStart":false})])],"isStart":false});}
            var Q65;
            {var subQ0=sQuery(id+"F0.wireOp",EDGE,"E29");Q65=makeQuery(id+"F3.opExtrude","CAP_EDGE",EDGE,{"disambiguationData":[OSD([subQ0]),TDD([makeQuery(id+"F1.opExtrude","CAP_EDGE",EDGE,{"disambiguationData":[OSD([subQ0])],"isStart":false})])],"isStart":false});}
            var Q66;
            {var subQ0=sQuery(id+"F0.wireOp",EDGE,"E33");Q66=makeQuery(id+"F3.opExtrude","CAP_EDGE",EDGE,{"disambiguationData":[OSD([subQ0]),TDD([makeQuery(id+"F1.opExtrude","CAP_EDGE",EDGE,{"disambiguationData":[OSD([subQ0])],"isStart":false})])],"isStart":false});}
            var Q67;
            {var subQ0=sQuery(id+"F0.wireOp",EDGE,"E36");Q67=makeQuery(id+"F3.opExtrude","CAP_EDGE",EDGE,{"disambiguationData":[OSD([subQ0]),TDD([makeQuery(id+"F1.opExtrude","CAP_EDGE",EDGE,{"disambiguationData":[OSD([subQ0])],"isStart":false})])],"isStart":false});}
            var Q68;
            {var subQ0=sQuery(id+"F0.wireOp",EDGE,"E34");Q68=makeQuery(id+"F3.opExtrude","CAP_EDGE",EDGE,{"disambiguationData":[OSD([subQ0]),TDD([makeQuery(id+"F1.opExtrude","CAP_EDGE",EDGE,{"disambiguationData":[OSD([subQ0])],"isStart":false})])],"isStart":false});}
            var Q69;
            {var subQ0=sQuery(id+"F0.wireOp",EDGE,"E35");Q69=makeQuery(id+"F3.opExtrude","CAP_EDGE",EDGE,{"disambiguationData":[OSD([subQ0]),TDD([makeQuery(id+"F1.opExtrude","CAP_EDGE",EDGE,{"disambiguationData":[OSD([subQ0])],"isStart":false})])],"isStart":false});}
            var Q70;
            {var subQ0=sQuery(id+"F0.wireOp",EDGE,"E41");Q70=makeQuery(id+"F3.opExtrude","CAP_EDGE",EDGE,{"disambiguationData":[OSD([subQ0]),TDD([makeQuery(id+"F1.opExtrude","CAP_EDGE",EDGE,{"disambiguationData":[OSD([subQ0])],"isStart":false})])],"isStart":false});}
            var Q71;
            {var subQ0=sQuery(id+"F0.wireOp",EDGE,"E42");Q71=makeQuery(id+"F3.opExtrude","CAP_EDGE",EDGE,{"disambiguationData":[OSD([subQ0]),TDD([makeQuery(id+"F1.opExtrude","CAP_EDGE",EDGE,{"disambiguationData":[OSD([subQ0])],"isStart":false})])],"isStart":false});}
            var Q72;
            {var subQ0=sQuery(id+"F0.wireOp",EDGE,"E92");Q72=makeQuery(id+"F3.opExtrude","CAP_EDGE",EDGE,{"disambiguationData":[OSD([subQ0]),TDD([makeQuery(id+"F1.opExtrude","CAP_EDGE",EDGE,{"disambiguationData":[OSD([subQ0])],"isStart":false})])],"isStart":false});}
            var Q73;
            {var subQ0=sQuery(id+"F0.wireOp",EDGE,"E97.MirrorCS");Q73=makeQuery(id+"F3.opExtrude","CAP_EDGE",EDGE,{"disambiguationData":[OSD([subQ0]),TDD([makeQuery(id+"F1.opExtrude","CAP_EDGE",EDGE,{"disambiguationData":[OSD([subQ0])],"isStart":false})])],"isStart":false});}
            var Q74;
            {var subQ0=sQuery(id+"F0.wireOp",EDGE,"E94.MirrorCS");Q74=makeQuery(id+"F3.opExtrude","CAP_EDGE",EDGE,{"disambiguationData":[OSD([subQ0]),TDD([makeQuery(id+"F1.opExtrude","CAP_EDGE",EDGE,{"disambiguationData":[OSD([subQ0])],"isStart":false})])],"isStart":false});}
            var Q75;
            {var subQ0=sQuery(id+"F0.wireOp",EDGE,"E93.MirrorCS");Q75=makeQuery(id+"F3.opExtrude","CAP_EDGE",EDGE,{"disambiguationData":[OSD([subQ0]),TDD([makeQuery(id+"F1.opExtrude","CAP_EDGE",EDGE,{"disambiguationData":[OSD([subQ0])],"isStart":false})])],"isStart":false});}
            var Q76;
            {var subQ0=sQuery(id+"F0.wireOp",EDGE,"E86");Q76=makeQuery(id+"F3.opExtrude","CAP_EDGE",EDGE,{"disambiguationData":[OSD([subQ0]),TDD([makeQuery(id+"F1.opExtrude","CAP_EDGE",EDGE,{"disambiguationData":[OSD([subQ0])],"isStart":false})])],"isStart":false});}
            var Q77;
            {var subQ0=sQuery(id+"F0.wireOp",EDGE,"E87");Q77=makeQuery(id+"F3.opExtrude","CAP_EDGE",EDGE,{"disambiguationData":[OSD([subQ0]),TDD([makeQuery(id+"F1.opExtrude","CAP_EDGE",EDGE,{"disambiguationData":[OSD([subQ0])],"isStart":false})])],"isStart":false});}
            var Q78;
            {var subQ0=sQuery(id+"F0.wireOp",EDGE,"E85");Q78=makeQuery(id+"F3.opExtrude","CAP_EDGE",EDGE,{"disambiguationData":[OSD([subQ0]),TDD([makeQuery(id+"F1.opExtrude","CAP_EDGE",EDGE,{"disambiguationData":[OSD([subQ0])],"isStart":false})])],"isStart":false});}
            var Q79;
            {var subQ0=sQuery(id+"F0.wireOp",EDGE,"E84");Q79=makeQuery(id+"F3.opExtrude","CAP_EDGE",EDGE,{"disambiguationData":[OSD([subQ0]),TDD([makeQuery(id+"F1.opExtrude","CAP_EDGE",EDGE,{"disambiguationData":[OSD([subQ0])],"isStart":false})])],"isStart":false});}
            var Q80;
            {var subQ0=sQuery(id+"F0.wireOp",EDGE,"E83.MirrorCS");Q80=makeQuery(id+"F3.opExtrude","CAP_EDGE",EDGE,{"disambiguationData":[OSD([subQ0]),TDD([makeQuery(id+"F1.opExtrude","CAP_EDGE",EDGE,{"disambiguationData":[OSD([subQ0])],"isStart":false})])],"isStart":false});}
            var Q81;
            {var subQ0=sQuery(id+"F0.wireOp",EDGE,"E98.MirrorCS");Q81=makeQuery(id+"F3.opExtrude","CAP_EDGE",EDGE,{"disambiguationData":[OSD([subQ0]),TDD([makeQuery(id+"F1.opExtrude","CAP_EDGE",EDGE,{"disambiguationData":[OSD([subQ0])],"isStart":false})])],"isStart":false});}
            var Q82;
            {var subQ0=sQuery(id+"F0.wireOp",EDGE,"E96.MirrorCS");Q82=makeQuery(id+"F3.opExtrude","CAP_EDGE",EDGE,{"disambiguationData":[OSD([subQ0]),TDD([makeQuery(id+"F1.opExtrude","CAP_EDGE",EDGE,{"disambiguationData":[OSD([subQ0])],"isStart":false})])],"isStart":false});}
            var Q83;
            {var subQ0=sQuery(id+"F0.wireOp",EDGE,"E95.MirrorCS");Q83=makeQuery(id+"F3.opExtrude","CAP_EDGE",EDGE,{"disambiguationData":[OSD([subQ0]),TDD([makeQuery(id+"F1.opExtrude","CAP_EDGE",EDGE,{"disambiguationData":[OSD([subQ0])],"isStart":false})])],"isStart":false});}
            var Q84;
            {var subQ0=sQuery(id+"F0.wireOp",EDGE,"E112.MirrorCS");Q84=makeQuery(id+"F3.opExtrude","CAP_EDGE",EDGE,{"disambiguationData":[OSD([subQ0]),TDD([makeQuery(id+"F1.opExtrude","CAP_EDGE",EDGE,{"disambiguationData":[OSD([subQ0])],"isStart":false})])],"isStart":false});}
            var Q85;
            {var subQ0=sQuery(id+"F0.wireOp",EDGE,"E111");Q85=makeQuery(id+"F3.opExtrude","CAP_EDGE",EDGE,{"disambiguationData":[OSD([subQ0]),TDD([makeQuery(id+"F1.opExtrude","CAP_EDGE",EDGE,{"disambiguationData":[OSD([subQ0])],"isStart":false})])],"isStart":false});}
            var Q86;
            {var subQ0=sQuery(id+"F0.wireOp",EDGE,"E105");Q86=makeQuery(id+"F3.opExtrude","CAP_EDGE",EDGE,{"disambiguationData":[OSD([subQ0]),TDD([makeQuery(id+"F1.opExtrude","CAP_EDGE",EDGE,{"disambiguationData":[OSD([subQ0])],"isStart":false})])],"isStart":false});}
            var Q87;
            {var subQ0=sQuery(id+"F0.wireOp",EDGE,"E106");Q87=makeQuery(id+"F3.opExtrude","CAP_EDGE",EDGE,{"disambiguationData":[OSD([subQ0]),TDD([makeQuery(id+"F1.opExtrude","CAP_EDGE",EDGE,{"disambiguationData":[OSD([subQ0])],"isStart":false})])],"isStart":false});}
            var Q88;
            {var subQ0=sQuery(id+"F0.wireOp",EDGE,"E102.MirrorCS");Q88=makeQuery(id+"F3.opExtrude","CAP_EDGE",EDGE,{"disambiguationData":[OSD([subQ0]),TDD([makeQuery(id+"F1.opExtrude","CAP_EDGE",EDGE,{"disambiguationData":[OSD([subQ0])],"isStart":false})])],"isStart":false});}
            var Q89;
            {var subQ0=sQuery(id+"F0.wireOp",EDGE,"E113.MirrorCS");Q89=makeQuery(id+"F3.opExtrude","CAP_EDGE",EDGE,{"disambiguationData":[OSD([subQ0]),TDD([makeQuery(id+"F1.opExtrude","CAP_EDGE",EDGE,{"disambiguationData":[OSD([subQ0])],"isStart":false})])],"isStart":false});}
            var Q90;
            {var subQ0=sQuery(id+"F0.wireOp",EDGE,"E119");Q90=makeQuery(id+"F3.opExtrude","CAP_EDGE",EDGE,{"disambiguationData":[OSD([subQ0]),TDD([makeQuery(id+"F1.opExtrude","CAP_EDGE",EDGE,{"disambiguationData":[OSD([subQ0])],"isStart":false})])],"isStart":false});}
            var Q91;
            {var subQ0=sQuery(id+"F0.wireOp",EDGE,"E127");Q91=makeQuery(id+"F3.opExtrude","CAP_EDGE",EDGE,{"disambiguationData":[OSD([subQ0]),TDD([makeQuery(id+"F1.opExtrude","CAP_EDGE",EDGE,{"disambiguationData":[OSD([subQ0])],"isStart":false})])],"isStart":false});}
            var Q92;
            {var subQ0=sQuery(id+"F0.wireOp",EDGE,"E117");Q92=makeQuery(id+"F3.opExtrude","CAP_EDGE",EDGE,{"disambiguationData":[OSD([subQ0]),TDD([makeQuery(id+"F1.opExtrude","CAP_EDGE",EDGE,{"disambiguationData":[OSD([subQ0])],"isStart":false})])],"isStart":false});}
            var Q93;
            {var subQ0=sQuery(id+"F0.wireOp",EDGE,"E115");Q93=makeQuery(id+"F3.opExtrude","CAP_EDGE",EDGE,{"disambiguationData":[OSD([subQ0]),TDD([makeQuery(id+"F1.opExtrude","CAP_EDGE",EDGE,{"disambiguationData":[OSD([subQ0])],"isStart":false})])],"isStart":false});}
            var Q94;
            {var subQ0=sQuery(id+"F0.wireOp",EDGE,"E114");Q94=makeQuery(id+"F3.opExtrude","CAP_EDGE",EDGE,{"disambiguationData":[OSD([subQ0]),TDD([makeQuery(id+"F1.opExtrude","CAP_EDGE",EDGE,{"disambiguationData":[OSD([subQ0])],"isStart":false})])],"isStart":false});}
            var Q95;
            {var subQ0=sQuery(id+"F0.wireOp",EDGE,"E116");Q95=makeQuery(id+"F3.opExtrude","CAP_EDGE",EDGE,{"disambiguationData":[OSD([subQ0]),TDD([makeQuery(id+"F1.opExtrude","CAP_EDGE",EDGE,{"disambiguationData":[OSD([subQ0])],"isStart":false})])],"isStart":false});}
            var Q96;
            {var subQ0=sQuery(id+"F0.wireOp",EDGE,"E130");Q96=makeQuery(id+"F3.opExtrude","CAP_EDGE",EDGE,{"disambiguationData":[OSD([subQ0]),TDD([makeQuery(id+"F1.opExtrude","CAP_EDGE",EDGE,{"disambiguationData":[OSD([subQ0])],"isStart":false})])],"isStart":false});}
            var Q97;
            {var subQ0=sQuery(id+"F0.wireOp",EDGE,"E126.right");Q97=makeQuery(id+"F3.opExtrude","CAP_EDGE",EDGE,{"disambiguationData":[OSD([subQ0]),TDD([makeQuery(id+"F1.opExtrude","CAP_EDGE",EDGE,{"disambiguationData":[OSD([subQ0])],"isStart":false})])],"isStart":false});}
            var Q98;
            {var subQ0=sQuery(id+"F0.wireOp",EDGE,"E126.left");Q98=makeQuery(id+"F3.opExtrude","CAP_EDGE",EDGE,{"disambiguationData":[OSD([subQ0]),TDD([makeQuery(id+"F1.opExtrude","CAP_EDGE",EDGE,{"disambiguationData":[OSD([subQ0])],"isStart":false})])],"isStart":false});}
            var Q99;
            {var subQ0=sQuery(id+"F0.wireOp",EDGE,"E129");Q99=makeQuery(id+"F3.opExtrude","CAP_EDGE",EDGE,{"disambiguationData":[OSD([subQ0]),TDD([makeQuery(id+"F1.opExtrude","CAP_EDGE",EDGE,{"disambiguationData":[OSD([subQ0])],"isStart":false})])],"isStart":false});}
            var Q100;
            {var subQ0=sQuery(id+"F0.wireOp",EDGE,"E122");Q100=makeQuery(id+"F3.opExtrude","CAP_EDGE",EDGE,{"disambiguationData":[OSD([subQ0]),TDD([makeQuery(id+"F0.imprint","IMPRINT",EDGE,{"derivedFrom":subQ0})])],"isStart":false});}
            var Q101;
            {var subQ0=sQuery(id+"F0.wireOp",EDGE,"E118");Q101=makeQuery(id+"F3.opExtrude","CAP_EDGE",EDGE,{"disambiguationData":[OSD([subQ0]),TDD([makeQuery(id+"F1.opExtrude","CAP_EDGE",EDGE,{"disambiguationData":[OSD([subQ0])],"isStart":false})])],"isStart":false});}
            var Q102;
            {var subQ0=sQuery(id+"F0.wireOp",EDGE,"E128");Q102=makeQuery(id+"F3.opExtrude","CAP_EDGE",EDGE,{"disambiguationData":[OSD([subQ0]),TDD([makeQuery(id+"F1.opExtrude","CAP_EDGE",EDGE,{"disambiguationData":[OSD([subQ0])],"isStart":false})])],"isStart":false});}
            var Q103;
            {var subQ0=sQuery(id+"F0.wireOp",EDGE,"E125");Q103=makeQuery(id+"F3.opExtrude","CAP_EDGE",EDGE,{"disambiguationData":[OSD([subQ0]),TDD([makeQuery(id+"F1.opExtrude","CAP_EDGE",EDGE,{"disambiguationData":[OSD([subQ0])],"isStart":false})])],"isStart":false});}
            var Q104;
            {var subQ0=sQuery(id+"F0.wireOp",EDGE,"E103");Q104=makeQuery(id+"F3.opExtrude","CAP_EDGE",EDGE,{"disambiguationData":[OSD([subQ0]),TDD([makeQuery(id+"F1.opExtrude","CAP_EDGE",EDGE,{"disambiguationData":[OSD([subQ0])],"isStart":false})])],"isStart":false});}
            var Q105;
            {var subQ0=sQuery(id+"F0.wireOp",EDGE,"E104");Q105=makeQuery(id+"F3.opExtrude","CAP_EDGE",EDGE,{"disambiguationData":[OSD([subQ0]),TDD([makeQuery(id+"F1.opExtrude","CAP_EDGE",EDGE,{"disambiguationData":[OSD([subQ0])],"isStart":false})])],"isStart":false});}
            var Q106;
            {var subQ0=sQuery(id+"F0.wireOp",EDGE,"E123");Q106=makeQuery(id+"F3.opExtrude","CAP_EDGE",EDGE,{"disambiguationData":[OSD([subQ0]),TDD([makeQuery(id+"F1.opExtrude","CAP_EDGE",EDGE,{"disambiguationData":[OSD([subQ0])],"isStart":false})])],"isStart":false});}
            var Q107;
            {var subQ0=sQuery(id+"F0.wireOp",EDGE,"E124");Q107=makeQuery(id+"F3.opExtrude","CAP_EDGE",EDGE,{"disambiguationData":[OSD([subQ0]),TDD([makeQuery(id+"F1.opExtrude","CAP_EDGE",EDGE,{"disambiguationData":[OSD([subQ0])],"isStart":false})])],"isStart":false});}
            var Q108;
            {var subQ0=sQuery(id+"F0.wireOp",EDGE,"E120");Q108=makeQuery(id+"F3.opExtrude","CAP_EDGE",EDGE,{"disambiguationData":[OSD([subQ0]),TDD([makeQuery(id+"F1.opExtrude","CAP_EDGE",EDGE,{"disambiguationData":[OSD([subQ0])],"isStart":false})])],"isStart":false});}
            var Q109;
            {var subQ0=sQuery(id+"F0.wireOp",EDGE,"E121");Q109=makeQuery(id+"F3.opExtrude","CAP_EDGE",EDGE,{"disambiguationData":[OSD([subQ0]),TDD([makeQuery(id+"F1.opExtrude","CAP_EDGE",EDGE,{"disambiguationData":[OSD([subQ0])],"isStart":false})])],"isStart":false});}
            var Q110;
            {var subQ0=sQuery(id+"F0.wireOp",EDGE,"E143");Q110=makeQuery(id+"F3.opExtrude","CAP_EDGE",EDGE,{"disambiguationData":[OSD([subQ0]),TDD([makeQuery(id+"F1.opExtrude","CAP_EDGE",EDGE,{"disambiguationData":[OSD([subQ0])],"isStart":false})])],"isStart":false});}
            var Q111;
            {var subQ0=sQuery(id+"F0.wireOp",EDGE,"E145");Q111=makeQuery(id+"F3.opExtrude","CAP_EDGE",EDGE,{"disambiguationData":[OSD([subQ0]),TDD([makeQuery(id+"F1.opExtrude","CAP_EDGE",EDGE,{"disambiguationData":[OSD([subQ0])],"isStart":false})])],"isStart":false});}
            var Q112;
            {var subQ0=sQuery(id+"F0.wireOp",EDGE,"E136");Q112=makeQuery(id+"F3.opExtrude","CAP_EDGE",EDGE,{"disambiguationData":[OSD([subQ0]),TDD([makeQuery(id+"F1.opExtrude","CAP_EDGE",EDGE,{"disambiguationData":[OSD([subQ0])],"isStart":false})])],"isStart":false});}
            var Q113;
            {var subQ0=sQuery(id+"F0.wireOp",EDGE,"E137");Q113=makeQuery(id+"F3.opExtrude","CAP_EDGE",EDGE,{"disambiguationData":[OSD([subQ0]),TDD([makeQuery(id+"F1.opExtrude","CAP_EDGE",EDGE,{"disambiguationData":[OSD([subQ0])],"isStart":false})])],"isStart":false});}
            var Q114;
            {var subQ0=sQuery(id+"F0.wireOp",EDGE,"E142");Q114=makeQuery(id+"F3.opExtrude","CAP_EDGE",EDGE,{"disambiguationData":[OSD([subQ0]),TDD([makeQuery(id+"F1.opExtrude","CAP_EDGE",EDGE,{"disambiguationData":[OSD([subQ0])],"isStart":false})])],"isStart":false});}
            var Q115;
            {var subQ0=sQuery(id+"F0.wireOp",EDGE,"E144");Q115=makeQuery(id+"F3.opExtrude","CAP_EDGE",EDGE,{"disambiguationData":[OSD([subQ0]),TDD([makeQuery(id+"F1.opExtrude","CAP_EDGE",EDGE,{"disambiguationData":[OSD([subQ0])],"isStart":false})])],"isStart":false});}
            var Q116;
            {var subQ0=sQuery(id+"F0.wireOp",EDGE,"E134");Q116=makeQuery(id+"F3.opExtrude","CAP_EDGE",EDGE,{"disambiguationData":[OSD([subQ0]),TDD([makeQuery(id+"F1.opExtrude","CAP_EDGE",EDGE,{"disambiguationData":[OSD([subQ0])],"isStart":false})])],"isStart":false});}
            var Q117;
            {var subQ0=sQuery(id+"F0.wireOp",EDGE,"E135");Q117=makeQuery(id+"F3.opExtrude","CAP_EDGE",EDGE,{"disambiguationData":[OSD([subQ0]),TDD([makeQuery(id+"F1.opExtrude","CAP_EDGE",EDGE,{"disambiguationData":[OSD([subQ0])],"isStart":false})])],"isStart":false});}
            fillet(context, id + "F4", {"entities" : qUnion([Q0, Q1, Q2, Q3, Q4, Q5, Q6, Q7, Q8, Q9, Q10, Q11, Q12, Q13, Q14, Q15, Q16, Q17, Q18, Q19, Q20, Q21, Q22, Q23, Q24, Q25, Q26, Q27, Q28, Q29, Q30, Q31, Q32, Q33, Q34, Q35, Q36, Q37, Q38, Q39, Q40, Q41, Q42, Q43, Q44, Q45, Q46, Q47, Q48, Q49, Q50, Q51, Q52, Q53, Q54, Q55, Q56, Q57, Q58, Q59, Q60, Q61, Q62, Q63, Q64, Q65, Q66, Q67, Q68, Q69, Q70, Q71, Q72, Q73, Q74, Q75, Q76, Q77, Q78, Q79, Q80, Q81, Q82, Q83, Q84, Q85, Q86, Q87, Q88, Q89, Q90, Q91, Q92, Q93, Q94, Q95, Q96, Q97, Q98, Q99, Q100, Q101, Q102, Q103, Q104, Q105, Q106, Q107, Q108, Q109, Q110, Q111, Q112, Q113, Q114, Q115, Q116, Q117]), "radius" : .29 * mm, "allowEdgeOverflow" : false});
        }
        {
            var Q0;
            {var subQ0=sQuery(id+"F0.wireOp",EDGE,"E60");var subQ1=sQuery(id+"F0.wireOp",EDGE,"E59");var subQ2=sQuery(id+"F0.wireOp",EDGE,"E58");var subQ3=sQuery(id+"F0.wireOp",EDGE,"E57");var subQ4=sQuery(id+"F0.wireOp",EDGE,"E56");var subQ5=sQuery(id+"F0.wireOp",EDGE,"E55");var subQ6=sQuery(id+"F0.wireOp",EDGE,"E54");var subQ7=sQuery(id+"F0.wireOp",EDGE,"E53");var subQ8=sQuery(id+"F0.wireOp",EDGE,"E52");var subQ9=sQuery(id+"F0.wireOp",EDGE,"E51");var subQ10=sQuery(id+"F0.wireOp",EDGE,"E50");var subQ11=sQuery(id+"F0.wireOp",EDGE,"E49");var subQ12=sQuery(id+"F0.wireOp",EDGE,"E48");var subQ13=sQuery(id+"F0.wireOp",EDGE,"E47");var subQ14=sQuery(id+"F0.wireOp",EDGE,"E46");var subQ15=sQuery(id+"F0.wireOp",EDGE,"E45");var subQ16=sQuery(id+"F0.wireOp",EDGE,"E44");var subQ17=sQuery(id+"F0.wireOp",EDGE,"E43");var subQ18=sQuery(id+"F0.wireOp",EDGE,"E42");var subQ19=sQuery(id+"F0.wireOp",EDGE,"E41");var subQ20=sQuery(id+"F0.wireOp",EDGE,"E40");var subQ21=sQuery(id+"F0.wireOp",EDGE,"E39");var subQ22=sQuery(id+"F0.wireOp",EDGE,"E38");var subQ23=sQuery(id+"F0.wireOp",EDGE,"E37");var subQ24=sQuery(id+"F0.wireOp",EDGE,"E36");var subQ25=sQuery(id+"F0.wireOp",EDGE,"E35");var subQ26=sQuery(id+"F0.wireOp",EDGE,"E34");var subQ27=sQuery(id+"F0.wireOp",EDGE,"E33");var subQ28=sQuery(id+"F0.wireOp",EDGE,"E32");var subQ29=sQuery(id+"F0.wireOp",EDGE,"E31");var subQ30=sQuery(id+"F0.wireOp",EDGE,"E30");var subQ31=sQuery(id+"F0.wireOp",EDGE,"E29");var subQ32=sQuery(id+"F0.wireOp",EDGE,"E28");var subQ33=sQuery(id+"F0.wireOp",EDGE,"E27");var subQ34=sQuery(id+"F0.wireOp",EDGE,"E26");var subQ35=sQuery(id+"F0.wireOp",EDGE,"E25");var subQ36=sQuery(id+"F0.wireOp",EDGE,"E24");var subQ37=sQuery(id+"F0.wireOp",EDGE,"E23");var subQ38=sQuery(id+"F0.wireOp",EDGE,"E22");var subQ39=sQuery(id+"F0.wireOp",EDGE,"E21");var subQ40=sQuery(id+"F0.wireOp",EDGE,"E20");var subQ41=sQuery(id+"F0.wireOp",EDGE,"E19");var subQ42=sQuery(id+"F0.wireOp",EDGE,"E18");var subQ43=sQuery(id+"F0.wireOp",EDGE,"E17");var subQ44=sQuery(id+"F0.wireOp",EDGE,"E16");var subQ45=sQuery(id+"F0.wireOp",EDGE,"E15");var subQ46=sQuery(id+"F0.wireOp",EDGE,"E14");var subQ47=sQuery(id+"F0.wireOp",EDGE,"E13");var subQ48=sQuery(id+"F0.wireOp",EDGE,"E67");var subQ49=sQuery(id+"F0.wireOp",EDGE,"E63");var subQ50=sQuery(id+"F0.wireOp",EDGE,"E12");var subQ51=sQuery(id+"F0.wireOp",EDGE,"E8");var subQ52=sQuery(id+"F0.wireOp",EDGE,"E62");var subQ53=sQuery(id+"F0.wireOp",EDGE,"E61");var subQ54=sQuery(id+"F0.wireOp",EDGE,"E11");var subQ55=sQuery(id+"F0.wireOp",EDGE,"E7");var subQ56=sQuery(id+"F0.wireOp",EDGE,"E65");var subQ57=sQuery(id+"F0.wireOp",EDGE,"E64");var subQ58=sQuery(id+"F0.wireOp",EDGE,"E9");var subQ59=sQuery(id+"F0.wireOp",EDGE,"E6");var subQ60=sQuery(id+"F0.wireOp",EDGE,"E66");var subQ61=sQuery(id+"F0.wireOp",EDGE,"E5");var subQ62=sQuery(id+"F0.wireOp",EDGE,"E4");var subQ63=sQuery(id+"F0.wireOp",EDGE,"E3");var subQ64=sQuery(id+"F0.wireOp",EDGE,"edaaeaec-2fa2-4ac8-96e5-24b6cc5294a60.MirrorC");var subQ65=sQuery(id+"F0.wireOp",EDGE,"E75");var subQ66=sQuery(id+"F0.wireOp",EDGE,"E73");var subQ67=sQuery(id+"F0.wireOp",EDGE,"E71.MirrorCS");var subQ68=sQuery(id+"F0.wireOp",EDGE,"E68");var subQ69=sQuery(id+"F0.wireOp",EDGE,"E0.right");var subQ70=sQuery(id+"F0.wireOp",EDGE,"E0.top");var subQ71=sQuery(id+"F0.wireOp",EDGE,"E0.bottom");var subQ72=sQuery(id+"F0.wireOp",EDGE,"E76");var subQ73=sQuery(id+"F0.wireOp",EDGE,"E74");var subQ74=sQuery(id+"F0.wireOp",EDGE,"E72");var subQ75=sQuery(id+"F0.wireOp",EDGE,"E70.MirrorCS");var subQ76=sQuery(id+"F0.wireOp",EDGE,"E69");var subQ77=sQuery(id+"F0.wireOp",EDGE,"E0.left");var subQ78=makeQuery(id+"F2.opExtrude","CAP_FACE",FACE,{"disambiguationData":[OSD([subQ71,subQ70,subQ77,subQ69,sQuery(id+"F0.wireOp",EDGE,"E1.bottom"),sQuery(id+"F0.wireOp",EDGE,"E1.top"),sQuery(id+"F0.wireOp",EDGE,"E1.left"),sQuery(id+"F0.wireOp",EDGE,"E1.right")])],"isStart":true});Q0=makeQuery(id+"F6.boolean.opBoolean","MERGE",FACE,{"derivedFrom":[subQ78,makeQuery(id+"F6.opPattern","COPY",FACE,{"derivedFrom":makeQuery(id+"F1.opExtrude","CAP_FACE",FACE,{"disambiguationData":[OSD([subQ71,subQ70,subQ63,subQ62,subQ61,subQ59,subQ55,subQ51,subQ58,subQ54,subQ50,subQ47,subQ46,subQ45,subQ44,subQ43,subQ42,subQ41,subQ40,subQ39,subQ38,subQ37,subQ36,subQ35,subQ34,subQ33,subQ32,subQ31,subQ30,subQ29,subQ28,subQ27,subQ26,subQ25,subQ24,subQ23,subQ22,subQ21,subQ20,subQ19,subQ18,subQ17,subQ16,subQ15,subQ14,subQ13,subQ12,subQ11,subQ10,subQ9,subQ8,subQ7,subQ6,subQ5,subQ4,subQ3,subQ2,subQ1,subQ0,subQ53,subQ52,subQ49,subQ57,subQ56,subQ60,subQ48,subQ68,subQ76,subQ75,subQ67,subQ74,subQ66,subQ73,subQ65])],"isStart":true}),"instanceName":"1"}),makeQuery(id+"F6.opPattern","COPY",FACE,{"derivedFrom":subQ78,"instanceName":"1"}),makeQuery(id+"F6.opPattern","COPY",FACE,{"derivedFrom":makeQuery(id+"F2.opExtrude","CAP_FACE",FACE,{"disambiguationData":[OSD([subQ72])],"isStart":true}),"instanceName":"1"}),makeQuery(id+"F6.opPattern","COPY",FACE,{"derivedFrom":makeQuery(id+"F2.opExtrude","CAP_FACE",FACE,{"disambiguationData":[OSD([subQ64])],"isStart":true}),"instanceName":"1"}),makeQuery(id+"F6.opPattern","COPY",FACE,{"derivedFrom":makeQuery(id+"F3.opExtrude","CAP_FACE",FACE,{"disambiguationData":[OSD([subQ71,subQ70,subQ77,subQ76,subQ75,subQ74,subQ73,subQ72,sQuery(id+"F0.wireOp",EDGE,"0858af88-9474-4ed9-898e-377d812cf8890.MirrorC")])],"isStart":true}),"instanceName":"1"}),makeQuery(id+"F6.opPattern","COPY",FACE,{"derivedFrom":makeQuery(id+"F3.opExtrude","CAP_FACE",FACE,{"disambiguationData":[OSD([subQ71,subQ70,subQ69,subQ68,subQ67,subQ66,subQ65,subQ64,sQuery(id+"F0.wireOp",EDGE,"ccb5a7b4-4bd2-4bd8-aee6-5957949556a70.MirrorC")])],"isStart":true}),"instanceName":"1"}),makeQuery(id+"F6.opPattern","COPY",FACE,{"derivedFrom":makeQuery(id+"F3.opExtrude","CAP_FACE",FACE,{"disambiguationData":[OSD([subQ63,subQ62,subQ61,subQ60])],"isStart":true}),"instanceName":"1"}),makeQuery(id+"F6.opPattern","COPY",FACE,{"derivedFrom":makeQuery(id+"F3.opExtrude","CAP_FACE",FACE,{"disambiguationData":[OSD([subQ59,subQ58,subQ57,subQ56])],"isStart":true}),"instanceName":"1"}),makeQuery(id+"F6.opPattern","COPY",FACE,{"derivedFrom":makeQuery(id+"F3.opExtrude","CAP_FACE",FACE,{"disambiguationData":[OSD([subQ55,subQ54,subQ53,subQ52])],"isStart":true}),"instanceName":"1"}),makeQuery(id+"F6.opPattern","COPY",FACE,{"derivedFrom":makeQuery(id+"F3.opExtrude","CAP_FACE",FACE,{"disambiguationData":[OSD([subQ51,subQ50,subQ49,subQ48])],"isStart":true}),"instanceName":"1"}),makeQuery(id+"F6.opPattern","COPY",FACE,{"derivedFrom":makeQuery(id+"F3.opExtrude","CAP_FACE",FACE,{"disambiguationData":[OSD([subQ47,subQ46,subQ45,subQ44])],"isStart":true}),"instanceName":"1"}),makeQuery(id+"F6.opPattern","COPY",FACE,{"derivedFrom":makeQuery(id+"F3.opExtrude","CAP_FACE",FACE,{"disambiguationData":[OSD([subQ43,subQ42,subQ41,subQ40])],"isStart":true}),"instanceName":"1"}),makeQuery(id+"F6.opPattern","COPY",FACE,{"derivedFrom":makeQuery(id+"F3.opExtrude","CAP_FACE",FACE,{"disambiguationData":[OSD([subQ39,subQ38,subQ37,subQ36])],"isStart":true}),"instanceName":"1"}),makeQuery(id+"F6.opPattern","COPY",FACE,{"derivedFrom":makeQuery(id+"F3.opExtrude","CAP_FACE",FACE,{"disambiguationData":[OSD([subQ35,subQ34,subQ33,subQ32])],"isStart":true}),"instanceName":"1"}),makeQuery(id+"F6.opPattern","COPY",FACE,{"derivedFrom":makeQuery(id+"F3.opExtrude","CAP_FACE",FACE,{"disambiguationData":[OSD([subQ31,subQ30,subQ29,subQ28])],"isStart":true}),"instanceName":"1"}),makeQuery(id+"F6.opPattern","COPY",FACE,{"derivedFrom":makeQuery(id+"F3.opExtrude","CAP_FACE",FACE,{"disambiguationData":[OSD([subQ27,subQ26,subQ25,subQ24])],"isStart":true}),"instanceName":"1"}),makeQuery(id+"F6.opPattern","COPY",FACE,{"derivedFrom":makeQuery(id+"F3.opExtrude","CAP_FACE",FACE,{"disambiguationData":[OSD([subQ23,subQ22,subQ21,subQ20])],"isStart":true}),"instanceName":"1"}),makeQuery(id+"F6.opPattern","COPY",FACE,{"derivedFrom":makeQuery(id+"F3.opExtrude","CAP_FACE",FACE,{"disambiguationData":[OSD([subQ19,subQ18,subQ17,subQ16])],"isStart":true}),"instanceName":"1"}),makeQuery(id+"F6.opPattern","COPY",FACE,{"derivedFrom":makeQuery(id+"F3.opExtrude","CAP_FACE",FACE,{"disambiguationData":[OSD([subQ15,subQ14,subQ13,subQ12])],"isStart":true}),"instanceName":"1"}),makeQuery(id+"F6.opPattern","COPY",FACE,{"derivedFrom":makeQuery(id+"F3.opExtrude","CAP_FACE",FACE,{"disambiguationData":[OSD([subQ11,subQ10,subQ9,subQ8])],"isStart":true}),"instanceName":"1"}),makeQuery(id+"F6.opPattern","COPY",FACE,{"derivedFrom":makeQuery(id+"F3.opExtrude","CAP_FACE",FACE,{"disambiguationData":[OSD([subQ7,subQ6,subQ5,subQ4])],"isStart":true}),"instanceName":"1"}),makeQuery(id+"F6.opPattern","COPY",FACE,{"derivedFrom":makeQuery(id+"F3.opExtrude","CAP_FACE",FACE,{"disambiguationData":[OSD([subQ3,subQ2,subQ1,subQ0])],"isStart":true}),"instanceName":"1"})]});}
            var Q1;
            {var subQ0=sQuery(id+"F0.wireOp",EDGE,"E0.right");Q1=makeQuery(id+"F0.imprint","IMPRINT",FACE,{"disambiguationData":[TD([[makeQuery(id+"F0.imprint","IMPRINT",EDGE,{"derivedFrom":subQ0}),-1.0]])]});}
            var Q2;
            Q2=makeQuery(id+"F0.imprint","IMPRINT",FACE,{"disambiguationData":[TD([[makeQuery(id+"F0.imprint","IMPRINT",EDGE,{"derivedFrom":sQuery(id+"F0.wireOp",EDGE,"edaaeaec-2fa2-4ac8-96e5-24b6cc5294a60.MirrorC")}),-1.0]])]});
            var Q3;
            Q3=makeQuery(id+"F0.imprint","IMPRINT",FACE,{"disambiguationData":[TD([[makeQuery(id+"F0.imprint","IMPRINT",EDGE,{"derivedFrom":sQuery(id+"F0.wireOp",EDGE,"E76")}),1.0]])]});
            var Q4;
            {var subQ0=sQuery(id+"F0.wireOp",EDGE,"E0.left");Q4=makeQuery(id+"F0.imprint","IMPRINT",FACE,{"disambiguationData":[TD([[makeQuery(id+"F0.imprint","IMPRINT",EDGE,{"derivedFrom":subQ0}),1.0]])]});}
            var Q5;
            Q5=makeQuery(id+"F0.imprint","IMPRINT",FACE,{"disambiguationData":[TD([[makeQuery(id+"F0.imprint","IMPRINT",EDGE,{"derivedFrom":sQuery(id+"F0.wireOp",EDGE,"E3")}),1.0]])]});
            var Q6;
            Q6=makeQuery(id+"F0.imprint","IMPRINT",FACE,{"disambiguationData":[TD([[makeQuery(id+"F0.imprint","IMPRINT",EDGE,{"derivedFrom":sQuery(id+"F0.wireOp",EDGE,"E57")}),1.0]])]});
            var Q7;
            Q7=makeQuery(id+"F0.imprint","IMPRINT",FACE,{"disambiguationData":[TD([[makeQuery(id+"F0.imprint","IMPRINT",EDGE,{"derivedFrom":sQuery(id+"F0.wireOp",EDGE,"E53")}),-1.0]])]});
            var Q8;
            Q8=makeQuery(id+"F0.imprint","IMPRINT",FACE,{"disambiguationData":[TD([[makeQuery(id+"F0.imprint","IMPRINT",EDGE,{"derivedFrom":sQuery(id+"F0.wireOp",EDGE,"E37")}),1.0]])]});
            var Q9;
            Q9=makeQuery(id+"F0.imprint","IMPRINT",FACE,{"disambiguationData":[TD([[makeQuery(id+"F0.imprint","IMPRINT",EDGE,{"derivedFrom":sQuery(id+"F0.wireOp",EDGE,"E41")}),-1.0]])]});
            var Q10;
            Q10=makeQuery(id+"F0.imprint","IMPRINT",FACE,{"disambiguationData":[TD([[makeQuery(id+"F0.imprint","IMPRINT",EDGE,{"derivedFrom":sQuery(id+"F0.wireOp",EDGE,"E25")}),1.0]])]});
            var Q11;
            Q11=makeQuery(id+"F0.imprint","IMPRINT",FACE,{"disambiguationData":[TD([[makeQuery(id+"F0.imprint","IMPRINT",EDGE,{"derivedFrom":sQuery(id+"F0.wireOp",EDGE,"E8")}),1.0]])]});
            var Q12;
            Q12=makeQuery(id+"F0.imprint","IMPRINT",FACE,{"disambiguationData":[TD([[makeQuery(id+"F0.imprint","IMPRINT",EDGE,{"derivedFrom":sQuery(id+"F0.wireOp",EDGE,"E17")}),1.0]])]});
            var Q13;
            Q13=makeQuery(id+"F0.imprint","IMPRINT",FACE,{"disambiguationData":[TD([[makeQuery(id+"F0.imprint","IMPRINT",EDGE,{"derivedFrom":sQuery(id+"F0.wireOp",EDGE,"E33")}),-1.0]])]});
            var Q14;
            Q14=makeQuery(id+"F0.imprint","IMPRINT",FACE,{"disambiguationData":[TD([[makeQuery(id+"F0.imprint","IMPRINT",EDGE,{"derivedFrom":sQuery(id+"F0.wireOp",EDGE,"E45")}),-1.0]])]});
            var Q15;
            Q15=makeQuery(id+"F0.imprint","IMPRINT",FACE,{"disambiguationData":[TD([[makeQuery(id+"F0.imprint","IMPRINT",EDGE,{"derivedFrom":sQuery(id+"F0.wireOp",EDGE,"E29")}),1.0]])]});
            var Q16;
            Q16=makeQuery(id+"F0.imprint","IMPRINT",FACE,{"disambiguationData":[TD([[makeQuery(id+"F0.imprint","IMPRINT",EDGE,{"derivedFrom":sQuery(id+"F0.wireOp",EDGE,"E13")}),-1.0]])]});
            var Q17;
            Q17=makeQuery(id+"F0.imprint","IMPRINT",FACE,{"disambiguationData":[TD([[makeQuery(id+"F0.imprint","IMPRINT",EDGE,{"derivedFrom":sQuery(id+"F0.wireOp",EDGE,"E6")}),-1.0]])]});
            var Q18;
            Q18=makeQuery(id+"F0.imprint","IMPRINT",FACE,{"disambiguationData":[TD([[makeQuery(id+"F0.imprint","IMPRINT",EDGE,{"derivedFrom":sQuery(id+"F0.wireOp",EDGE,"E7")}),1.0]])]});
            var Q19;
            Q19=makeQuery(id+"F0.imprint","IMPRINT",FACE,{"disambiguationData":[TD([[makeQuery(id+"F0.imprint","IMPRINT",EDGE,{"derivedFrom":sQuery(id+"F0.wireOp",EDGE,"E21")}),1.0]])]});
            var Q20;
            Q20=makeQuery(id+"F0.imprint","IMPRINT",FACE,{"disambiguationData":[TD([[makeQuery(id+"F0.imprint","IMPRINT",EDGE,{"derivedFrom":sQuery(id+"F0.wireOp",EDGE,"E3")}),-1.0]])]});
            var Q21;
            Q21=makeQuery(id+"F0.imprint","IMPRINT",FACE,{"disambiguationData":[TD([[makeQuery(id+"F0.imprint","IMPRINT",EDGE,{"derivedFrom":sQuery(id+"F0.wireOp",EDGE,"E49")}),1.0]])]});
            var Q22;
            Q22=makeQuery(id+"F0.imprint","IMPRINT",FACE,{"disambiguationData":[TD([[makeQuery(id+"F0.imprint","IMPRINT",EDGE,{"derivedFrom":sQuery(id+"F0.wireOp",EDGE,"ccb5a7b4-4bd2-4bd8-aee6-5957949556a70.MirrorC")}),1.0]])]});
            var Q23;
            Q23=makeQuery(id+"F0.imprint","IMPRINT",FACE,{"disambiguationData":[TD([[makeQuery(id+"F0.imprint","IMPRINT",EDGE,{"derivedFrom":sQuery(id+"F0.wireOp",EDGE,"0858af88-9474-4ed9-898e-377d812cf8890.MirrorC")}),-1.0]])]});
            var Q24;
            Q24=makeQuery(id+"F0.imprint","IMPRINT",FACE,{"disambiguationData":[TD([[makeQuery(id+"F0.imprint","IMPRINT",EDGE,{"derivedFrom":sQuery(id+"F0.wireOp",EDGE,"E78.MirrorC")}),-1.0]])]});
            var Q25;
            Q25=makeQuery(id+"F0.imprint","IMPRINT",FACE,{"disambiguationData":[TD([[makeQuery(id+"F0.imprint","IMPRINT",EDGE,{"derivedFrom":sQuery(id+"F0.wireOp",EDGE,"E79.MirrorC")}),1.0]])]});
            var Q26;
            Q26=makeQuery(id+"F0.imprint","IMPRINT",FACE,{"disambiguationData":[TD([[makeQuery(id+"F0.imprint","IMPRINT",EDGE,{"derivedFrom":sQuery(id+"F0.wireOp",EDGE,"E77.MirrorC")}),-1.0]])]});
            var Q27;
            {var subQ1=sQuery(id+"F0.wireOp",EDGE,"E80.left");Q27=makeQuery(id+"F0.imprint","IMPRINT",FACE,{"disambiguationData":[TD([[makeQuery(id+"F0.imprint","IMPRINT",EDGE,{"derivedFrom":subQ1}),-1.0]])]});}
            var Q28;
            Q28=makeQuery(id+"F0.imprint","IMPRINT",FACE,{"disambiguationData":[TD([[makeQuery(id+"F0.imprint","IMPRINT",EDGE,{"derivedFrom":sQuery(id+"F0.wireOp",EDGE,"E90.MirrorC")}),-1.0]])]});
            var Q29;
            Q29=makeQuery(id+"F0.imprint","IMPRINT",FACE,{"disambiguationData":[TD([[makeQuery(id+"F0.imprint","IMPRINT",EDGE,{"derivedFrom":sQuery(id+"F0.wireOp",EDGE,"E91.MirrorC")}),1.0]])]});
            var Q30;
            Q30=makeQuery(id+"F0.imprint","IMPRINT",FACE,{"disambiguationData":[TD([[makeQuery(id+"F0.imprint","IMPRINT",EDGE,{"derivedFrom":sQuery(id+"F0.wireOp",EDGE,"E89.MirrorC")}),-1.0]])]});
            var Q31;
            Q31=makeQuery(id+"F0.imprint","IMPRINT",FACE,{"disambiguationData":[TD([[makeQuery(id+"F0.imprint","IMPRINT",EDGE,{"derivedFrom":sQuery(id+"F0.wireOp",EDGE,"E88")}),1.0]])]});
            var Q32;
            Q32=makeQuery(id+"F0.imprint","IMPRINT",FACE,{"disambiguationData":[TD([[makeQuery(id+"F0.imprint","IMPRINT",EDGE,{"derivedFrom":sQuery(id+"F0.wireOp",EDGE,"E94.MirrorCS")}),1.0]])]});
            var Q33;
            Q33=makeQuery(id+"F0.imprint","IMPRINT",FACE,{"disambiguationData":[TD([[makeQuery(id+"F0.imprint","IMPRINT",EDGE,{"derivedFrom":sQuery(id+"F0.wireOp",EDGE,"E83.MirrorCS")}),1.0]])]});
            var Q34;
            {var subQ0=sQuery(id+"F0.wireOp",EDGE,"E80.left");Q34=makeQuery(id+"F0.imprint","IMPRINT",FACE,{"disambiguationData":[TD([[makeQuery(id+"F0.imprint","IMPRINT",EDGE,{"derivedFrom":subQ0}),1.0]])]});}
            var Q35;
            {var subQ1=sQuery(id+"F0.wireOp",EDGE,"E80.right");Q35=makeQuery(id+"F0.imprint","IMPRINT",FACE,{"disambiguationData":[TD([[makeQuery(id+"F0.imprint","IMPRINT",EDGE,{"derivedFrom":subQ1}),-1.0]])]});}
            var Q36;
            Q36=makeQuery(id+"F0.imprint","IMPRINT",FACE,{"disambiguationData":[TD([[makeQuery(id+"F0.imprint","IMPRINT",EDGE,{"derivedFrom":sQuery(id+"F0.wireOp",EDGE,"E110.MirrorC")}),1.0]])]});
            var Q37;
            Q37=makeQuery(id+"F0.imprint","IMPRINT",FACE,{"disambiguationData":[TD([[makeQuery(id+"F0.imprint","IMPRINT",EDGE,{"derivedFrom":sQuery(id+"F0.wireOp",EDGE,"E109.MirrorC")}),-1.0]])]});
            var Q38;
            Q38=makeQuery(id+"F0.imprint","IMPRINT",FACE,{"disambiguationData":[TD([[makeQuery(id+"F0.imprint","IMPRINT",EDGE,{"derivedFrom":sQuery(id+"F0.wireOp",EDGE,"E108.MirrorC")}),-1.0]])]});
            var Q39;
            Q39=makeQuery(id+"F0.imprint","IMPRINT",FACE,{"disambiguationData":[TD([[makeQuery(id+"F0.imprint","IMPRINT",EDGE,{"derivedFrom":sQuery(id+"F0.wireOp",EDGE,"E107")}),1.0]])]});
            var Q40;
            {var subQ1=sQuery(id+"F0.wireOp",EDGE,"E99.right");Q40=makeQuery(id+"F0.imprint","IMPRINT",FACE,{"disambiguationData":[TD([[makeQuery(id+"F0.imprint","IMPRINT",EDGE,{"derivedFrom":subQ1}),-1.0]])]});}
            var Q41;
            {var subQ1=sQuery(id+"F0.wireOp",EDGE,"E99.left");Q41=makeQuery(id+"F0.imprint","IMPRINT",FACE,{"disambiguationData":[TD([[makeQuery(id+"F0.imprint","IMPRINT",EDGE,{"derivedFrom":subQ1}),-1.0]])]});}
            var Q42;
            Q42=makeQuery(id+"F0.imprint","IMPRINT",FACE,{"disambiguationData":[TD([[makeQuery(id+"F0.imprint","IMPRINT",EDGE,{"derivedFrom":sQuery(id+"F0.wireOp",EDGE,"E102.MirrorCS")}),1.0]])]});
            var Q43;
            Q43=makeQuery(id+"F0.imprint","IMPRINT",FACE,{"disambiguationData":[TD([[makeQuery(id+"F0.imprint","IMPRINT",EDGE,{"derivedFrom":sQuery(id+"F0.wireOp",EDGE,"E114")}),1.0]])]});
            var Q44;
            Q44=makeQuery(id+"F0.imprint","IMPRINT",FACE,{"disambiguationData":[TD([[makeQuery(id+"F0.imprint","IMPRINT",EDGE,{"derivedFrom":sQuery(id+"F0.wireOp",EDGE,"E118")}),-1.0]])]});
            var Q45;
            Q45=makeQuery(id+"F0.imprint","IMPRINT",FACE,{"disambiguationData":[TD([[makeQuery(id+"F0.imprint","IMPRINT",EDGE,{"derivedFrom":sQuery(id+"F0.wireOp",EDGE,"E120")}),-1.0]])]});
            var Q46;
            Q46=makeQuery(id+"F0.imprint","IMPRINT",FACE,{"disambiguationData":[TD([[makeQuery(id+"F0.imprint","IMPRINT",EDGE,{"derivedFrom":sQuery(id+"F0.wireOp",EDGE,"E119")}),1.0]])]});
            var Q47;
            {var subQ0=sQuery(id+"F0.wireOp",EDGE,"E99.left");Q47=makeQuery(id+"F0.imprint","IMPRINT",FACE,{"disambiguationData":[TD([[makeQuery(id+"F0.imprint","IMPRINT",EDGE,{"derivedFrom":subQ0}),1.0]])]});}
            var Q48;
            Q48=makeQuery(id+"F0.imprint","IMPRINT",FACE,{"disambiguationData":[TD([[makeQuery(id+"F0.imprint","IMPRINT",EDGE,{"derivedFrom":sQuery(id+"F0.wireOp",EDGE,"E140.MirrorC")}),-1.0]])]});
            var Q49;
            Q49=makeQuery(id+"F0.imprint","IMPRINT",FACE,{"disambiguationData":[TD([[makeQuery(id+"F0.imprint","IMPRINT",EDGE,{"derivedFrom":sQuery(id+"F0.wireOp",EDGE,"E141.MirrorC")}),1.0]])]});
            var Q50;
            Q50=makeQuery(id+"F0.imprint","IMPRINT",FACE,{"disambiguationData":[TD([[makeQuery(id+"F0.imprint","IMPRINT",EDGE,{"derivedFrom":sQuery(id+"F0.wireOp",EDGE,"E138")}),1.0]])]});
            var Q51;
            Q51=makeQuery(id+"F0.imprint","IMPRINT",FACE,{"disambiguationData":[TD([[makeQuery(id+"F0.imprint","IMPRINT",EDGE,{"derivedFrom":sQuery(id+"F0.wireOp",EDGE,"E139.MirrorC")}),-1.0]])]});
            var Q52;
            {var subQ1=sQuery(id+"F0.wireOp",EDGE,"E131.left");Q52=makeQuery(id+"F0.imprint","IMPRINT",FACE,{"disambiguationData":[TD([[makeQuery(id+"F0.imprint","IMPRINT",EDGE,{"derivedFrom":subQ1}),-1.0]])]});}
            var Q53;
            Q53=makeQuery(id+"F0.imprint","IMPRINT",FACE,{"disambiguationData":[TD([[makeQuery(id+"F0.imprint","IMPRINT",EDGE,{"derivedFrom":sQuery(id+"F0.wireOp",EDGE,"E143")}),1.0]])]});
            var Q54;
            {var subQ1=sQuery(id+"F0.wireOp",EDGE,"E134");Q54=makeQuery(id+"F0.imprint","IMPRINT",FACE,{"disambiguationData":[TD([[makeQuery(id+"F0.imprint","IMPRINT",EDGE,{"derivedFrom":subQ1}),1.0]])]});}
            var Q55;
            {var subQ1=sQuery(id+"F0.wireOp",EDGE,"E131.left");Q55=makeQuery(id+"F0.imprint","IMPRINT",FACE,{"disambiguationData":[TD([[makeQuery(id+"F0.imprint","IMPRINT",EDGE,{"derivedFrom":subQ1}),1.0]])]});}
            var Q56;
            {var subQ1=sQuery(id+"F0.wireOp",EDGE,"E131.right");Q56=makeQuery(id+"F0.imprint","IMPRINT",FACE,{"disambiguationData":[TD([[makeQuery(id+"F0.imprint","IMPRINT",EDGE,{"derivedFrom":subQ1}),-1.0]])]});}
            var Q57;
            Q57=sQuery(id+"F0.wireOp",EDGE,"E1.left");
            var Q58;
            Q58=sQuery(id+"F0.wireOp",EDGE,"E1.bottom");
            var Q59;
            Q59=sQuery(id+"F0.wireOp",EDGE,"E1.top");
            var Q60;
            Q60=sQuery(id+"F0.wireOp",EDGE,"E1.right");
            extrude(context, id + "F5", {"entities" : qUnion([Q0, Q1, Q2, Q3, Q4, Q5, Q6, Q7, Q8, Q9, Q10, Q11, Q12, Q13, Q14, Q15, Q16, Q17, Q18, Q19, Q20, Q21, Q22, Q23, Q24, Q25, Q26, Q27, Q28, Q29, Q30, Q31, Q32, Q33, Q34, Q35, Q36, Q37, Q38, Q39, Q40, Q41, Q42, Q43, Q44, Q45, Q46, Q47, Q48, Q49, Q50, Q51, Q52, Q53, Q54, Q55, Q56]), "operationType" : NewBodyOperationType.ADD, "surfaceEntities" : qUnion([Q57, Q58, Q59, Q60]), "depth" : 2 * mm, "offsetDistance" : 25 * mm});
        }
        {
            var Q0;
            Q0=makeQuery(id+"F2.opExtrude","SWEPT_BODY",BODY,{"disambiguationData":[OSD([sQuery(id+"F0.wireOp",EDGE,"ccb5a7b4-4bd2-4bd8-aee6-5957949556a70.MirrorC")])]});
            var Q1;
            Q1=makeQuery(id+"F3.opExtrude","SWEPT_BODY",BODY,{"disambiguationData":[OSD([sQuery(id+"F0.wireOp",EDGE,"E3"),sQuery(id+"F0.wireOp",EDGE,"E4"),sQuery(id+"F0.wireOp",EDGE,"E5"),sQuery(id+"F0.wireOp",EDGE,"E66")])]});
            var Q2;
            Q2=makeQuery(id+"F3.opExtrude","SWEPT_BODY",BODY,{"disambiguationData":[OSD([sQuery(id+"F0.wireOp",EDGE,"E13"),sQuery(id+"F0.wireOp",EDGE,"E14"),sQuery(id+"F0.wireOp",EDGE,"E15"),sQuery(id+"F0.wireOp",EDGE,"E16")])]});
            var Q3;
            Q3=makeQuery(id+"F3.opExtrude","SWEPT_BODY",BODY,{"disambiguationData":[OSD([sQuery(id+"F0.wireOp",EDGE,"E8"),sQuery(id+"F0.wireOp",EDGE,"E12"),sQuery(id+"F0.wireOp",EDGE,"E63"),sQuery(id+"F0.wireOp",EDGE,"E67")])]});
            var Q4;
            Q4=makeQuery(id+"F3.opExtrude","SWEPT_BODY",BODY,{"disambiguationData":[OSD([sQuery(id+"F0.wireOp",EDGE,"E17"),sQuery(id+"F0.wireOp",EDGE,"E18"),sQuery(id+"F0.wireOp",EDGE,"E19"),sQuery(id+"F0.wireOp",EDGE,"E20")])]});
            var Q5;
            Q5=makeQuery(id+"F3.opExtrude","SWEPT_BODY",BODY,{"disambiguationData":[OSD([sQuery(id+"F0.wireOp",EDGE,"E25"),sQuery(id+"F0.wireOp",EDGE,"E26"),sQuery(id+"F0.wireOp",EDGE,"E27"),sQuery(id+"F0.wireOp",EDGE,"E28")])]});
            var Q6;
            Q6=makeQuery(id+"F3.opExtrude","SWEPT_BODY",BODY,{"disambiguationData":[OSD([sQuery(id+"F0.wireOp",EDGE,"E33"),sQuery(id+"F0.wireOp",EDGE,"E34"),sQuery(id+"F0.wireOp",EDGE,"E35"),sQuery(id+"F0.wireOp",EDGE,"E36")])]});
            var Q7;
            Q7=makeQuery(id+"F3.opExtrude","SWEPT_BODY",BODY,{"disambiguationData":[OSD([sQuery(id+"F0.wireOp",EDGE,"E7"),sQuery(id+"F0.wireOp",EDGE,"E11"),sQuery(id+"F0.wireOp",EDGE,"E61"),sQuery(id+"F0.wireOp",EDGE,"E62")])]});
            var Q8;
            Q8=makeQuery(id+"F3.opExtrude","SWEPT_BODY",BODY,{"disambiguationData":[OSD([sQuery(id+"F0.wireOp",EDGE,"E6"),sQuery(id+"F0.wireOp",EDGE,"E9"),sQuery(id+"F0.wireOp",EDGE,"E64"),sQuery(id+"F0.wireOp",EDGE,"E65")])]});
            var Q9;
            Q9=makeQuery(id+"F3.opExtrude","SWEPT_BODY",BODY,{"disambiguationData":[OSD([sQuery(id+"F0.wireOp",EDGE,"E0.bottom"),sQuery(id+"F0.wireOp",EDGE,"E0.top"),sQuery(id+"F0.wireOp",EDGE,"E0.right"),sQuery(id+"F0.wireOp",EDGE,"E68"),sQuery(id+"F0.wireOp",EDGE,"E71.MirrorCS"),sQuery(id+"F0.wireOp",EDGE,"E73"),sQuery(id+"F0.wireOp",EDGE,"E75"),sQuery(id+"F0.wireOp",EDGE,"edaaeaec-2fa2-4ac8-96e5-24b6cc5294a60.MirrorC"),sQuery(id+"F0.wireOp",EDGE,"ccb5a7b4-4bd2-4bd8-aee6-5957949556a70.MirrorC")])]});
            var Q10;
            Q10=makeQuery(id+"F2.opExtrude","SWEPT_BODY",BODY,{"disambiguationData":[OSD([sQuery(id+"F0.wireOp",EDGE,"E76")])]});
            var Q11;
            Q11=makeQuery(id+"F3.opExtrude","SWEPT_BODY",BODY,{"disambiguationData":[OSD([sQuery(id+"F0.wireOp",EDGE,"E0.bottom"),sQuery(id+"F0.wireOp",EDGE,"E0.top"),sQuery(id+"F0.wireOp",EDGE,"E0.left"),sQuery(id+"F0.wireOp",EDGE,"E69"),sQuery(id+"F0.wireOp",EDGE,"E70.MirrorCS"),sQuery(id+"F0.wireOp",EDGE,"E72"),sQuery(id+"F0.wireOp",EDGE,"E74"),sQuery(id+"F0.wireOp",EDGE,"E76"),sQuery(id+"F0.wireOp",EDGE,"0858af88-9474-4ed9-898e-377d812cf8890.MirrorC")])]});
            var Q12;
            Q12=makeQuery(id+"F3.opExtrude","SWEPT_BODY",BODY,{"disambiguationData":[OSD([sQuery(id+"F0.wireOp",EDGE,"E57"),sQuery(id+"F0.wireOp",EDGE,"E58"),sQuery(id+"F0.wireOp",EDGE,"E59"),sQuery(id+"F0.wireOp",EDGE,"E60")])]});
            var Q13;
            Q13=makeQuery(id+"F2.opExtrude","SWEPT_BODY",BODY,{"disambiguationData":[OSD([sQuery(id+"F0.wireOp",EDGE,"E0.bottom"),sQuery(id+"F0.wireOp",EDGE,"E0.top"),sQuery(id+"F0.wireOp",EDGE,"E0.left"),sQuery(id+"F0.wireOp",EDGE,"E0.right"),sQuery(id+"F0.wireOp",EDGE,"E1.bottom"),sQuery(id+"F0.wireOp",EDGE,"E1.top"),sQuery(id+"F0.wireOp",EDGE,"E1.left"),sQuery(id+"F0.wireOp",EDGE,"E1.right")])]});
            var Q14;
            Q14=makeQuery(id+"F3.opExtrude","SWEPT_BODY",BODY,{"disambiguationData":[OSD([sQuery(id+"F0.wireOp",EDGE,"E29"),sQuery(id+"F0.wireOp",EDGE,"E30"),sQuery(id+"F0.wireOp",EDGE,"E31"),sQuery(id+"F0.wireOp",EDGE,"E32")])]});
            var Q15;
            Q15=makeQuery(id+"F3.opExtrude","SWEPT_BODY",BODY,{"disambiguationData":[OSD([sQuery(id+"F0.wireOp",EDGE,"E37"),sQuery(id+"F0.wireOp",EDGE,"E38"),sQuery(id+"F0.wireOp",EDGE,"E39"),sQuery(id+"F0.wireOp",EDGE,"E40")])]});
            var Q16;
            Q16=makeQuery(id+"F3.opExtrude","SWEPT_BODY",BODY,{"disambiguationData":[OSD([sQuery(id+"F0.wireOp",EDGE,"E21"),sQuery(id+"F0.wireOp",EDGE,"E22"),sQuery(id+"F0.wireOp",EDGE,"E23"),sQuery(id+"F0.wireOp",EDGE,"E24")])]});
            var Q17;
            Q17=makeQuery(id+"F3.opExtrude","SWEPT_BODY",BODY,{"disambiguationData":[OSD([sQuery(id+"F0.wireOp",EDGE,"E53"),sQuery(id+"F0.wireOp",EDGE,"E54"),sQuery(id+"F0.wireOp",EDGE,"E55"),sQuery(id+"F0.wireOp",EDGE,"E56")])]});
            var Q18;
            Q18=makeQuery(id+"F3.opExtrude","SWEPT_BODY",BODY,{"disambiguationData":[OSD([sQuery(id+"F0.wireOp",EDGE,"E41"),sQuery(id+"F0.wireOp",EDGE,"E42"),sQuery(id+"F0.wireOp",EDGE,"E43"),sQuery(id+"F0.wireOp",EDGE,"E44")])]});
            var Q19;
            Q19=makeQuery(id+"F3.opExtrude","SWEPT_BODY",BODY,{"disambiguationData":[OSD([sQuery(id+"F0.wireOp",EDGE,"E49"),sQuery(id+"F0.wireOp",EDGE,"E50"),sQuery(id+"F0.wireOp",EDGE,"E51"),sQuery(id+"F0.wireOp",EDGE,"E52")])]});
            var Q20;
            Q20=makeQuery(id+"F3.opExtrude","SWEPT_BODY",BODY,{"disambiguationData":[OSD([sQuery(id+"F0.wireOp",EDGE,"E45"),sQuery(id+"F0.wireOp",EDGE,"E46"),sQuery(id+"F0.wireOp",EDGE,"E47"),sQuery(id+"F0.wireOp",EDGE,"E48")])]});
            var Q21;
            Q21=makeQuery(id+"F3.opExtrude","SWEPT_BODY",BODY,{"disambiguationData":[OSD([sQuery(id+"F0.wireOp",EDGE,"E0.bottom"),sQuery(id+"F0.wireOp",EDGE,"E0.top"),sQuery(id+"F0.wireOp",EDGE,"E3"),sQuery(id+"F0.wireOp",EDGE,"E4"),sQuery(id+"F0.wireOp",EDGE,"E5"),sQuery(id+"F0.wireOp",EDGE,"E6"),sQuery(id+"F0.wireOp",EDGE,"E7"),sQuery(id+"F0.wireOp",EDGE,"E8"),sQuery(id+"F0.wireOp",EDGE,"E9"),sQuery(id+"F0.wireOp",EDGE,"E11"),sQuery(id+"F0.wireOp",EDGE,"E12"),sQuery(id+"F0.wireOp",EDGE,"E13"),sQuery(id+"F0.wireOp",EDGE,"E14"),sQuery(id+"F0.wireOp",EDGE,"E15"),sQuery(id+"F0.wireOp",EDGE,"E16"),sQuery(id+"F0.wireOp",EDGE,"E17"),sQuery(id+"F0.wireOp",EDGE,"E18"),sQuery(id+"F0.wireOp",EDGE,"E19"),sQuery(id+"F0.wireOp",EDGE,"E20"),sQuery(id+"F0.wireOp",EDGE,"E21"),sQuery(id+"F0.wireOp",EDGE,"E22"),sQuery(id+"F0.wireOp",EDGE,"E23"),sQuery(id+"F0.wireOp",EDGE,"E24"),sQuery(id+"F0.wireOp",EDGE,"E25"),sQuery(id+"F0.wireOp",EDGE,"E26"),sQuery(id+"F0.wireOp",EDGE,"E27"),sQuery(id+"F0.wireOp",EDGE,"E28"),sQuery(id+"F0.wireOp",EDGE,"E29"),sQuery(id+"F0.wireOp",EDGE,"E30"),sQuery(id+"F0.wireOp",EDGE,"E31"),sQuery(id+"F0.wireOp",EDGE,"E32"),sQuery(id+"F0.wireOp",EDGE,"E33"),sQuery(id+"F0.wireOp",EDGE,"E34"),sQuery(id+"F0.wireOp",EDGE,"E35"),sQuery(id+"F0.wireOp",EDGE,"E36"),sQuery(id+"F0.wireOp",EDGE,"E37"),sQuery(id+"F0.wireOp",EDGE,"E38"),sQuery(id+"F0.wireOp",EDGE,"E39"),sQuery(id+"F0.wireOp",EDGE,"E40"),sQuery(id+"F0.wireOp",EDGE,"E41"),sQuery(id+"F0.wireOp",EDGE,"E42"),sQuery(id+"F0.wireOp",EDGE,"E43"),sQuery(id+"F0.wireOp",EDGE,"E44"),sQuery(id+"F0.wireOp",EDGE,"E45"),sQuery(id+"F0.wireOp",EDGE,"E46"),sQuery(id+"F0.wireOp",EDGE,"E47"),sQuery(id+"F0.wireOp",EDGE,"E48"),sQuery(id+"F0.wireOp",EDGE,"E49"),sQuery(id+"F0.wireOp",EDGE,"E50"),sQuery(id+"F0.wireOp",EDGE,"E51"),sQuery(id+"F0.wireOp",EDGE,"E52"),sQuery(id+"F0.wireOp",EDGE,"E53"),sQuery(id+"F0.wireOp",EDGE,"E54"),sQuery(id+"F0.wireOp",EDGE,"E55"),sQuery(id+"F0.wireOp",EDGE,"E56"),sQuery(id+"F0.wireOp",EDGE,"E57"),sQuery(id+"F0.wireOp",EDGE,"E58"),sQuery(id+"F0.wireOp",EDGE,"E59"),sQuery(id+"F0.wireOp",EDGE,"E60"),sQuery(id+"F0.wireOp",EDGE,"E61"),sQuery(id+"F0.wireOp",EDGE,"E62"),sQuery(id+"F0.wireOp",EDGE,"E63"),sQuery(id+"F0.wireOp",EDGE,"E64"),sQuery(id+"F0.wireOp",EDGE,"E65"),sQuery(id+"F0.wireOp",EDGE,"E66"),sQuery(id+"F0.wireOp",EDGE,"E67"),sQuery(id+"F0.wireOp",EDGE,"E68"),sQuery(id+"F0.wireOp",EDGE,"E69"),sQuery(id+"F0.wireOp",EDGE,"E70.MirrorCS"),sQuery(id+"F0.wireOp",EDGE,"E71.MirrorCS"),sQuery(id+"F0.wireOp",EDGE,"E72"),sQuery(id+"F0.wireOp",EDGE,"E73"),sQuery(id+"F0.wireOp",EDGE,"E74"),sQuery(id+"F0.wireOp",EDGE,"E75")])]});
            var Q22;
            Q22=makeQuery(id+"F1.opExtrude","SWEPT_BODY",BODY,{"disambiguationData":[OSD([sQuery(id+"F0.wireOp",EDGE,"E0.bottom"),sQuery(id+"F0.wireOp",EDGE,"E0.top"),sQuery(id+"F0.wireOp",EDGE,"E3"),sQuery(id+"F0.wireOp",EDGE,"E4"),sQuery(id+"F0.wireOp",EDGE,"E5"),sQuery(id+"F0.wireOp",EDGE,"E6"),sQuery(id+"F0.wireOp",EDGE,"E7"),sQuery(id+"F0.wireOp",EDGE,"E8"),sQuery(id+"F0.wireOp",EDGE,"E9"),sQuery(id+"F0.wireOp",EDGE,"E11"),sQuery(id+"F0.wireOp",EDGE,"E12"),sQuery(id+"F0.wireOp",EDGE,"E13"),sQuery(id+"F0.wireOp",EDGE,"E14"),sQuery(id+"F0.wireOp",EDGE,"E15"),sQuery(id+"F0.wireOp",EDGE,"E16"),sQuery(id+"F0.wireOp",EDGE,"E17"),sQuery(id+"F0.wireOp",EDGE,"E18"),sQuery(id+"F0.wireOp",EDGE,"E19"),sQuery(id+"F0.wireOp",EDGE,"E20"),sQuery(id+"F0.wireOp",EDGE,"E21"),sQuery(id+"F0.wireOp",EDGE,"E22"),sQuery(id+"F0.wireOp",EDGE,"E23"),sQuery(id+"F0.wireOp",EDGE,"E24"),sQuery(id+"F0.wireOp",EDGE,"E25"),sQuery(id+"F0.wireOp",EDGE,"E26"),sQuery(id+"F0.wireOp",EDGE,"E27"),sQuery(id+"F0.wireOp",EDGE,"E28"),sQuery(id+"F0.wireOp",EDGE,"E29"),sQuery(id+"F0.wireOp",EDGE,"E30"),sQuery(id+"F0.wireOp",EDGE,"E31"),sQuery(id+"F0.wireOp",EDGE,"E32"),sQuery(id+"F0.wireOp",EDGE,"E33"),sQuery(id+"F0.wireOp",EDGE,"E34"),sQuery(id+"F0.wireOp",EDGE,"E35"),sQuery(id+"F0.wireOp",EDGE,"E36"),sQuery(id+"F0.wireOp",EDGE,"E37"),sQuery(id+"F0.wireOp",EDGE,"E38"),sQuery(id+"F0.wireOp",EDGE,"E39"),sQuery(id+"F0.wireOp",EDGE,"E40"),sQuery(id+"F0.wireOp",EDGE,"E41"),sQuery(id+"F0.wireOp",EDGE,"E42"),sQuery(id+"F0.wireOp",EDGE,"E43"),sQuery(id+"F0.wireOp",EDGE,"E44"),sQuery(id+"F0.wireOp",EDGE,"E45"),sQuery(id+"F0.wireOp",EDGE,"E46"),sQuery(id+"F0.wireOp",EDGE,"E47"),sQuery(id+"F0.wireOp",EDGE,"E48"),sQuery(id+"F0.wireOp",EDGE,"E49"),sQuery(id+"F0.wireOp",EDGE,"E50"),sQuery(id+"F0.wireOp",EDGE,"E51"),sQuery(id+"F0.wireOp",EDGE,"E52"),sQuery(id+"F0.wireOp",EDGE,"E53"),sQuery(id+"F0.wireOp",EDGE,"E54"),sQuery(id+"F0.wireOp",EDGE,"E55"),sQuery(id+"F0.wireOp",EDGE,"E56"),sQuery(id+"F0.wireOp",EDGE,"E57"),sQuery(id+"F0.wireOp",EDGE,"E58"),sQuery(id+"F0.wireOp",EDGE,"E59"),sQuery(id+"F0.wireOp",EDGE,"E60"),sQuery(id+"F0.wireOp",EDGE,"E61"),sQuery(id+"F0.wireOp",EDGE,"E62"),sQuery(id+"F0.wireOp",EDGE,"E63"),sQuery(id+"F0.wireOp",EDGE,"E64"),sQuery(id+"F0.wireOp",EDGE,"E65"),sQuery(id+"F0.wireOp",EDGE,"E66"),sQuery(id+"F0.wireOp",EDGE,"E67"),sQuery(id+"F0.wireOp",EDGE,"E68"),sQuery(id+"F0.wireOp",EDGE,"E69"),sQuery(id+"F0.wireOp",EDGE,"E70.MirrorCS"),sQuery(id+"F0.wireOp",EDGE,"E71.MirrorCS"),sQuery(id+"F0.wireOp",EDGE,"E72"),sQuery(id+"F0.wireOp",EDGE,"E73"),sQuery(id+"F0.wireOp",EDGE,"E74"),sQuery(id+"F0.wireOp",EDGE,"E75")])]});
            var Q23;
            Q23=makeQuery(id+"F2.opExtrude","SWEPT_BODY",BODY,{"disambiguationData":[OSD([sQuery(id+"F0.wireOp",EDGE,"edaaeaec-2fa2-4ac8-96e5-24b6cc5294a60.MirrorC")])]});
            var Q24;
            Q24=makeQuery(id+"F2.opExtrude","SWEPT_FACE",FACE,{"disambiguationData":[OSD([sQuery(id+"F0.wireOp",EDGE,"E1.right")])]});
            mirror(context, id + "F6", {"operationType" : NewBodyOperationType.ADD, "entities" : qUnion([Q0, Q1, Q2, Q3, Q4, Q5, Q6, Q7, Q8, Q9, Q10, Q11, Q12, Q13, Q14, Q15, Q16, Q17, Q18, Q19, Q20, Q21, Q22, Q23]), "mirrorPlane" : qUnion([Q24])});
        }
        {
            var Q0;
            Q0=makeQuery(id+"F1.opExtrude","SWEPT_BODY",BODY,{"disambiguationData":[OSD([sQuery(id+"F0.wireOp",EDGE,"E80.bottom"),sQuery(id+"F0.wireOp",EDGE,"E80.top"),sQuery(id+"F0.wireOp",EDGE,"E83.MirrorCS"),sQuery(id+"F0.wireOp",EDGE,"E84"),sQuery(id+"F0.wireOp",EDGE,"E85"),sQuery(id+"F0.wireOp",EDGE,"E86"),sQuery(id+"F0.wireOp",EDGE,"E87"),sQuery(id+"F0.wireOp",EDGE,"E92"),sQuery(id+"F0.wireOp",EDGE,"E93.MirrorCS"),sQuery(id+"F0.wireOp",EDGE,"E94.MirrorCS"),sQuery(id+"F0.wireOp",EDGE,"E95.MirrorCS"),sQuery(id+"F0.wireOp",EDGE,"E96.MirrorCS"),sQuery(id+"F0.wireOp",EDGE,"E97.MirrorCS"),sQuery(id+"F0.wireOp",EDGE,"E98.MirrorCS")])]});
            var Q1;
            Q1=makeQuery(id+"F3.opExtrude","SWEPT_BODY",BODY,{"disambiguationData":[OSD([sQuery(id+"F0.wireOp",EDGE,"E80.bottom"),sQuery(id+"F0.wireOp",EDGE,"E80.top"),sQuery(id+"F0.wireOp",EDGE,"E83.MirrorCS"),sQuery(id+"F0.wireOp",EDGE,"E84"),sQuery(id+"F0.wireOp",EDGE,"E85"),sQuery(id+"F0.wireOp",EDGE,"E86"),sQuery(id+"F0.wireOp",EDGE,"E87"),sQuery(id+"F0.wireOp",EDGE,"E92"),sQuery(id+"F0.wireOp",EDGE,"E93.MirrorCS"),sQuery(id+"F0.wireOp",EDGE,"E94.MirrorCS"),sQuery(id+"F0.wireOp",EDGE,"E95.MirrorCS"),sQuery(id+"F0.wireOp",EDGE,"E96.MirrorCS"),sQuery(id+"F0.wireOp",EDGE,"E97.MirrorCS"),sQuery(id+"F0.wireOp",EDGE,"E98.MirrorCS")])]});
            var Q2;
            {var subQ0=sQuery(id+"F0.wireOp",EDGE,"E81.left");Q2=makeQuery(id+"F5.boolean.opBoolean","MERGE",FACE,{"derivedFrom":[makeQuery(id+"F2.opExtrude","SWEPT_FACE",FACE,{"disambiguationData":[OSD([subQ0])]}),makeQuery(id+"F5.opExtrude","SWEPT_FACE",FACE,{"disambiguationData":[OSD([subQ0])]})]});}
            mirror(context, id + "F7", {"operationType" : NewBodyOperationType.ADD, "entities" : qUnion([Q0, Q1]), "mirrorPlane" : qUnion([Q2])});
        }
        {
            var Q0;
            Q0=makeQuery(id+"F3.opExtrude","SWEPT_BODY",BODY,{"disambiguationData":[OSD([sQuery(id+"F0.wireOp",EDGE,"E99.bottom"),sQuery(id+"F0.wireOp",EDGE,"E99.top"),sQuery(id+"F0.wireOp",EDGE,"E102.MirrorCS"),sQuery(id+"F0.wireOp",EDGE,"E103"),sQuery(id+"F0.wireOp",EDGE,"E104"),sQuery(id+"F0.wireOp",EDGE,"E105"),sQuery(id+"F0.wireOp",EDGE,"E106"),sQuery(id+"F0.wireOp",EDGE,"E111"),sQuery(id+"F0.wireOp",EDGE,"E112.MirrorCS"),sQuery(id+"F0.wireOp",EDGE,"E113.MirrorCS"),sQuery(id+"F0.wireOp",EDGE,"E114"),sQuery(id+"F0.wireOp",EDGE,"E115"),sQuery(id+"F0.wireOp",EDGE,"E116"),sQuery(id+"F0.wireOp",EDGE,"E117"),sQuery(id+"F0.wireOp",EDGE,"E118"),sQuery(id+"F0.wireOp",EDGE,"E119"),sQuery(id+"F0.wireOp",EDGE,"E120"),sQuery(id+"F0.wireOp",EDGE,"E121"),sQuery(id+"F0.wireOp",EDGE,"E122"),sQuery(id+"F0.wireOp",EDGE,"E123"),sQuery(id+"F0.wireOp",EDGE,"E124"),sQuery(id+"F0.wireOp",EDGE,"E125"),sQuery(id+"F0.wireOp",EDGE,"E126.right"),sQuery(id+"F0.wireOp",EDGE,"E126.left"),sQuery(id+"F0.wireOp",EDGE,"E127"),sQuery(id+"F0.wireOp",EDGE,"E128"),sQuery(id+"F0.wireOp",EDGE,"E129"),sQuery(id+"F0.wireOp",EDGE,"E130")])]});
            var Q1;
            Q1=makeQuery(id+"F3.opExtrude","SWEPT_BODY",BODY,{"disambiguationData":[OSD([sQuery(id+"F0.wireOp",EDGE,"E99.bottom"),sQuery(id+"F0.wireOp",EDGE,"E99.top"),sQuery(id+"F0.wireOp",EDGE,"E99.left"),sQuery(id+"F0.wireOp",EDGE,"E99.right"),sQuery(id+"F0.wireOp",EDGE,"E100.bottom"),sQuery(id+"F0.wireOp",EDGE,"E100.top"),sQuery(id+"F0.wireOp",EDGE,"E100.left"),sQuery(id+"F0.wireOp",EDGE,"E100.right")])]});
            var Q2;
            Q2=makeQuery(id+"F1.opExtrude","SWEPT_BODY",BODY,{"disambiguationData":[OSD([sQuery(id+"F0.wireOp",EDGE,"E99.bottom"),sQuery(id+"F0.wireOp",EDGE,"E99.top"),sQuery(id+"F0.wireOp",EDGE,"E102.MirrorCS"),sQuery(id+"F0.wireOp",EDGE,"E103"),sQuery(id+"F0.wireOp",EDGE,"E104"),sQuery(id+"F0.wireOp",EDGE,"E105"),sQuery(id+"F0.wireOp",EDGE,"E106"),sQuery(id+"F0.wireOp",EDGE,"E111"),sQuery(id+"F0.wireOp",EDGE,"E112.MirrorCS"),sQuery(id+"F0.wireOp",EDGE,"E113.MirrorCS"),sQuery(id+"F0.wireOp",EDGE,"E114"),sQuery(id+"F0.wireOp",EDGE,"E115"),sQuery(id+"F0.wireOp",EDGE,"E116"),sQuery(id+"F0.wireOp",EDGE,"E117"),sQuery(id+"F0.wireOp",EDGE,"E118"),sQuery(id+"F0.wireOp",EDGE,"E119"),sQuery(id+"F0.wireOp",EDGE,"E120"),sQuery(id+"F0.wireOp",EDGE,"E121"),sQuery(id+"F0.wireOp",EDGE,"E122"),sQuery(id+"F0.wireOp",EDGE,"E123"),sQuery(id+"F0.wireOp",EDGE,"E124"),sQuery(id+"F0.wireOp",EDGE,"E125"),sQuery(id+"F0.wireOp",EDGE,"E126.right"),sQuery(id+"F0.wireOp",EDGE,"E126.left"),sQuery(id+"F0.wireOp",EDGE,"E127"),sQuery(id+"F0.wireOp",EDGE,"E128"),sQuery(id+"F0.wireOp",EDGE,"E129"),sQuery(id+"F0.wireOp",EDGE,"E130")])]});
            var Q3;
            {var subQ0=sQuery(id+"F0.wireOp",EDGE,"E100.left");Q3=makeQuery(id+"F5.boolean.opBoolean","MERGE",FACE,{"derivedFrom":[makeQuery(id+"F2.opExtrude","SWEPT_FACE",FACE,{"disambiguationData":[OSD([subQ0])]}),makeQuery(id+"F5.opExtrude","SWEPT_FACE",FACE,{"disambiguationData":[OSD([subQ0])]})]});}
            mirror(context, id + "F8", {"entities" : qUnion([Q0, Q1, Q2]), "mirrorPlane" : qUnion([Q3])});
        }
        {
            var Q0;
            Q0=makeQuery(id+"F3.opExtrude","SWEPT_BODY",BODY,{"disambiguationData":[OSD([sQuery(id+"F0.wireOp",EDGE,"E131.bottom"),sQuery(id+"F0.wireOp",EDGE,"E131.top"),sQuery(id+"F0.wireOp",EDGE,"E134"),sQuery(id+"F0.wireOp",EDGE,"E135"),sQuery(id+"F0.wireOp",EDGE,"E136"),sQuery(id+"F0.wireOp",EDGE,"E137"),sQuery(id+"F0.wireOp",EDGE,"E142"),sQuery(id+"F0.wireOp",EDGE,"E143"),sQuery(id+"F0.wireOp",EDGE,"E144"),sQuery(id+"F0.wireOp",EDGE,"E145")])]});
            var Q1;
            Q1=makeQuery(id+"F1.opExtrude","SWEPT_BODY",BODY,{"disambiguationData":[OSD([sQuery(id+"F0.wireOp",EDGE,"E131.bottom"),sQuery(id+"F0.wireOp",EDGE,"E131.top"),sQuery(id+"F0.wireOp",EDGE,"E134"),sQuery(id+"F0.wireOp",EDGE,"E135"),sQuery(id+"F0.wireOp",EDGE,"E136"),sQuery(id+"F0.wireOp",EDGE,"E137"),sQuery(id+"F0.wireOp",EDGE,"E142"),sQuery(id+"F0.wireOp",EDGE,"E143"),sQuery(id+"F0.wireOp",EDGE,"E144"),sQuery(id+"F0.wireOp",EDGE,"E145")])]});
            var Q2;
            {var subQ0=sQuery(id+"F0.wireOp",EDGE,"E132.right");Q2=makeQuery(id+"F5.boolean.opBoolean","MERGE",FACE,{"derivedFrom":[makeQuery(id+"F2.opExtrude","SWEPT_FACE",FACE,{"disambiguationData":[OSD([subQ0])]}),makeQuery(id+"F5.opExtrude","SWEPT_FACE",FACE,{"disambiguationData":[OSD([subQ0])]})]});}
            mirror(context, id + "F9", {"operationType" : NewBodyOperationType.ADD, "entities" : qUnion([Q0, Q1]), "mirrorPlane" : qUnion([Q2])});
        }
        {
            var Q0;
            Q0=makeQuery(id+"F3.opExtrude","SWEPT_BODY",BODY,{"disambiguationData":[OSD([sQuery(id+"F0.wireOp",EDGE,"E0.bottom"),sQuery(id+"F0.wireOp",EDGE,"E0.top"),sQuery(id+"F0.wireOp",EDGE,"E3"),sQuery(id+"F0.wireOp",EDGE,"E4"),sQuery(id+"F0.wireOp",EDGE,"E5"),sQuery(id+"F0.wireOp",EDGE,"E6"),sQuery(id+"F0.wireOp",EDGE,"E7"),sQuery(id+"F0.wireOp",EDGE,"E8"),sQuery(id+"F0.wireOp",EDGE,"E9"),sQuery(id+"F0.wireOp",EDGE,"E11"),sQuery(id+"F0.wireOp",EDGE,"E12"),sQuery(id+"F0.wireOp",EDGE,"E13"),sQuery(id+"F0.wireOp",EDGE,"E14"),sQuery(id+"F0.wireOp",EDGE,"E15"),sQuery(id+"F0.wireOp",EDGE,"E16"),sQuery(id+"F0.wireOp",EDGE,"E17"),sQuery(id+"F0.wireOp",EDGE,"E18"),sQuery(id+"F0.wireOp",EDGE,"E19"),sQuery(id+"F0.wireOp",EDGE,"E20"),sQuery(id+"F0.wireOp",EDGE,"E21"),sQuery(id+"F0.wireOp",EDGE,"E22"),sQuery(id+"F0.wireOp",EDGE,"E23"),sQuery(id+"F0.wireOp",EDGE,"E24"),sQuery(id+"F0.wireOp",EDGE,"E25"),sQuery(id+"F0.wireOp",EDGE,"E26"),sQuery(id+"F0.wireOp",EDGE,"E27"),sQuery(id+"F0.wireOp",EDGE,"E28"),sQuery(id+"F0.wireOp",EDGE,"E29"),sQuery(id+"F0.wireOp",EDGE,"E30"),sQuery(id+"F0.wireOp",EDGE,"E31"),sQuery(id+"F0.wireOp",EDGE,"E32"),sQuery(id+"F0.wireOp",EDGE,"E33"),sQuery(id+"F0.wireOp",EDGE,"E34"),sQuery(id+"F0.wireOp",EDGE,"E35"),sQuery(id+"F0.wireOp",EDGE,"E36"),sQuery(id+"F0.wireOp",EDGE,"E37"),sQuery(id+"F0.wireOp",EDGE,"E38"),sQuery(id+"F0.wireOp",EDGE,"E39"),sQuery(id+"F0.wireOp",EDGE,"E40"),sQuery(id+"F0.wireOp",EDGE,"E41"),sQuery(id+"F0.wireOp",EDGE,"E42"),sQuery(id+"F0.wireOp",EDGE,"E43"),sQuery(id+"F0.wireOp",EDGE,"E44"),sQuery(id+"F0.wireOp",EDGE,"E45"),sQuery(id+"F0.wireOp",EDGE,"E46"),sQuery(id+"F0.wireOp",EDGE,"E47"),sQuery(id+"F0.wireOp",EDGE,"E48"),sQuery(id+"F0.wireOp",EDGE,"E49"),sQuery(id+"F0.wireOp",EDGE,"E50"),sQuery(id+"F0.wireOp",EDGE,"E51"),sQuery(id+"F0.wireOp",EDGE,"E52"),sQuery(id+"F0.wireOp",EDGE,"E53"),sQuery(id+"F0.wireOp",EDGE,"E54"),sQuery(id+"F0.wireOp",EDGE,"E55"),sQuery(id+"F0.wireOp",EDGE,"E56"),sQuery(id+"F0.wireOp",EDGE,"E57"),sQuery(id+"F0.wireOp",EDGE,"E58"),sQuery(id+"F0.wireOp",EDGE,"E59"),sQuery(id+"F0.wireOp",EDGE,"E60"),sQuery(id+"F0.wireOp",EDGE,"E61"),sQuery(id+"F0.wireOp",EDGE,"E62"),sQuery(id+"F0.wireOp",EDGE,"E63"),sQuery(id+"F0.wireOp",EDGE,"E64"),sQuery(id+"F0.wireOp",EDGE,"E65"),sQuery(id+"F0.wireOp",EDGE,"E66"),sQuery(id+"F0.wireOp",EDGE,"E67"),sQuery(id+"F0.wireOp",EDGE,"E68"),sQuery(id+"F0.wireOp",EDGE,"E69"),sQuery(id+"F0.wireOp",EDGE,"E70.MirrorCS"),sQuery(id+"F0.wireOp",EDGE,"E71.MirrorCS"),sQuery(id+"F0.wireOp",EDGE,"E72"),sQuery(id+"F0.wireOp",EDGE,"E73"),sQuery(id+"F0.wireOp",EDGE,"E74"),sQuery(id+"F0.wireOp",EDGE,"E75")])]});
            var Q1;
            Q1=makeQuery(id+"F1.opExtrude","SWEPT_BODY",BODY,{"disambiguationData":[OSD([sQuery(id+"F0.wireOp",EDGE,"E0.bottom"),sQuery(id+"F0.wireOp",EDGE,"E0.top"),sQuery(id+"F0.wireOp",EDGE,"E3"),sQuery(id+"F0.wireOp",EDGE,"E4"),sQuery(id+"F0.wireOp",EDGE,"E5"),sQuery(id+"F0.wireOp",EDGE,"E6"),sQuery(id+"F0.wireOp",EDGE,"E7"),sQuery(id+"F0.wireOp",EDGE,"E8"),sQuery(id+"F0.wireOp",EDGE,"E9"),sQuery(id+"F0.wireOp",EDGE,"E11"),sQuery(id+"F0.wireOp",EDGE,"E12"),sQuery(id+"F0.wireOp",EDGE,"E13"),sQuery(id+"F0.wireOp",EDGE,"E14"),sQuery(id+"F0.wireOp",EDGE,"E15"),sQuery(id+"F0.wireOp",EDGE,"E16"),sQuery(id+"F0.wireOp",EDGE,"E17"),sQuery(id+"F0.wireOp",EDGE,"E18"),sQuery(id+"F0.wireOp",EDGE,"E19"),sQuery(id+"F0.wireOp",EDGE,"E20"),sQuery(id+"F0.wireOp",EDGE,"E21"),sQuery(id+"F0.wireOp",EDGE,"E22"),sQuery(id+"F0.wireOp",EDGE,"E23"),sQuery(id+"F0.wireOp",EDGE,"E24"),sQuery(id+"F0.wireOp",EDGE,"E25"),sQuery(id+"F0.wireOp",EDGE,"E26"),sQuery(id+"F0.wireOp",EDGE,"E27"),sQuery(id+"F0.wireOp",EDGE,"E28"),sQuery(id+"F0.wireOp",EDGE,"E29"),sQuery(id+"F0.wireOp",EDGE,"E30"),sQuery(id+"F0.wireOp",EDGE,"E31"),sQuery(id+"F0.wireOp",EDGE,"E32"),sQuery(id+"F0.wireOp",EDGE,"E33"),sQuery(id+"F0.wireOp",EDGE,"E34"),sQuery(id+"F0.wireOp",EDGE,"E35"),sQuery(id+"F0.wireOp",EDGE,"E36"),sQuery(id+"F0.wireOp",EDGE,"E37"),sQuery(id+"F0.wireOp",EDGE,"E38"),sQuery(id+"F0.wireOp",EDGE,"E39"),sQuery(id+"F0.wireOp",EDGE,"E40"),sQuery(id+"F0.wireOp",EDGE,"E41"),sQuery(id+"F0.wireOp",EDGE,"E42"),sQuery(id+"F0.wireOp",EDGE,"E43"),sQuery(id+"F0.wireOp",EDGE,"E44"),sQuery(id+"F0.wireOp",EDGE,"E45"),sQuery(id+"F0.wireOp",EDGE,"E46"),sQuery(id+"F0.wireOp",EDGE,"E47"),sQuery(id+"F0.wireOp",EDGE,"E48"),sQuery(id+"F0.wireOp",EDGE,"E49"),sQuery(id+"F0.wireOp",EDGE,"E50"),sQuery(id+"F0.wireOp",EDGE,"E51"),sQuery(id+"F0.wireOp",EDGE,"E52"),sQuery(id+"F0.wireOp",EDGE,"E53"),sQuery(id+"F0.wireOp",EDGE,"E54"),sQuery(id+"F0.wireOp",EDGE,"E55"),sQuery(id+"F0.wireOp",EDGE,"E56"),sQuery(id+"F0.wireOp",EDGE,"E57"),sQuery(id+"F0.wireOp",EDGE,"E58"),sQuery(id+"F0.wireOp",EDGE,"E59"),sQuery(id+"F0.wireOp",EDGE,"E60"),sQuery(id+"F0.wireOp",EDGE,"E61"),sQuery(id+"F0.wireOp",EDGE,"E62"),sQuery(id+"F0.wireOp",EDGE,"E63"),sQuery(id+"F0.wireOp",EDGE,"E64"),sQuery(id+"F0.wireOp",EDGE,"E65"),sQuery(id+"F0.wireOp",EDGE,"E66"),sQuery(id+"F0.wireOp",EDGE,"E67"),sQuery(id+"F0.wireOp",EDGE,"E68"),sQuery(id+"F0.wireOp",EDGE,"E69"),sQuery(id+"F0.wireOp",EDGE,"E70.MirrorCS"),sQuery(id+"F0.wireOp",EDGE,"E71.MirrorCS"),sQuery(id+"F0.wireOp",EDGE,"E72"),sQuery(id+"F0.wireOp",EDGE,"E73"),sQuery(id+"F0.wireOp",EDGE,"E74"),sQuery(id+"F0.wireOp",EDGE,"E75")])]});
            var Q2;
            Q2=makeQuery(id+"F3.opExtrude","SWEPT_BODY",BODY,{"disambiguationData":[OSD([sQuery(id+"F0.wireOp",EDGE,"E80.bottom"),sQuery(id+"F0.wireOp",EDGE,"E80.top"),sQuery(id+"F0.wireOp",EDGE,"E83.MirrorCS"),sQuery(id+"F0.wireOp",EDGE,"E84"),sQuery(id+"F0.wireOp",EDGE,"E85"),sQuery(id+"F0.wireOp",EDGE,"E86"),sQuery(id+"F0.wireOp",EDGE,"E87"),sQuery(id+"F0.wireOp",EDGE,"E92"),sQuery(id+"F0.wireOp",EDGE,"E93.MirrorCS"),sQuery(id+"F0.wireOp",EDGE,"E94.MirrorCS"),sQuery(id+"F0.wireOp",EDGE,"E95.MirrorCS"),sQuery(id+"F0.wireOp",EDGE,"E96.MirrorCS"),sQuery(id+"F0.wireOp",EDGE,"E97.MirrorCS"),sQuery(id+"F0.wireOp",EDGE,"E98.MirrorCS")])]});
            var Q3;
            Q3=makeQuery(id+"F8.opPattern","COPY",BODY,{"derivedFrom":makeQuery(id+"F3.opExtrude","SWEPT_BODY",BODY,{"disambiguationData":[OSD([sQuery(id+"F0.wireOp",EDGE,"E99.bottom"),sQuery(id+"F0.wireOp",EDGE,"E99.top"),sQuery(id+"F0.wireOp",EDGE,"E99.left"),sQuery(id+"F0.wireOp",EDGE,"E99.right"),sQuery(id+"F0.wireOp",EDGE,"E100.bottom"),sQuery(id+"F0.wireOp",EDGE,"E100.top"),sQuery(id+"F0.wireOp",EDGE,"E100.left"),sQuery(id+"F0.wireOp",EDGE,"E100.right")])]}),"instanceName":"1"});
            var Q4;
            Q4=makeQuery(id+"F8.opPattern","COPY",BODY,{"derivedFrom":makeQuery(id+"F1.opExtrude","SWEPT_BODY",BODY,{"disambiguationData":[OSD([sQuery(id+"F0.wireOp",EDGE,"E99.bottom"),sQuery(id+"F0.wireOp",EDGE,"E99.top"),sQuery(id+"F0.wireOp",EDGE,"E102.MirrorCS"),sQuery(id+"F0.wireOp",EDGE,"E103"),sQuery(id+"F0.wireOp",EDGE,"E104"),sQuery(id+"F0.wireOp",EDGE,"E105"),sQuery(id+"F0.wireOp",EDGE,"E106"),sQuery(id+"F0.wireOp",EDGE,"E111"),sQuery(id+"F0.wireOp",EDGE,"E112.MirrorCS"),sQuery(id+"F0.wireOp",EDGE,"E113.MirrorCS"),sQuery(id+"F0.wireOp",EDGE,"E114"),sQuery(id+"F0.wireOp",EDGE,"E115"),sQuery(id+"F0.wireOp",EDGE,"E116"),sQuery(id+"F0.wireOp",EDGE,"E117"),sQuery(id+"F0.wireOp",EDGE,"E118"),sQuery(id+"F0.wireOp",EDGE,"E119"),sQuery(id+"F0.wireOp",EDGE,"E120"),sQuery(id+"F0.wireOp",EDGE,"E121"),sQuery(id+"F0.wireOp",EDGE,"E122"),sQuery(id+"F0.wireOp",EDGE,"E123"),sQuery(id+"F0.wireOp",EDGE,"E124"),sQuery(id+"F0.wireOp",EDGE,"E125"),sQuery(id+"F0.wireOp",EDGE,"E126.right"),sQuery(id+"F0.wireOp",EDGE,"E126.left"),sQuery(id+"F0.wireOp",EDGE,"E127"),sQuery(id+"F0.wireOp",EDGE,"E128"),sQuery(id+"F0.wireOp",EDGE,"E129"),sQuery(id+"F0.wireOp",EDGE,"E130")])]}),"instanceName":"1"});
            var Q5;
            Q5=makeQuery(id+"F3.opExtrude","SWEPT_BODY",BODY,{"disambiguationData":[OSD([sQuery(id+"F0.wireOp",EDGE,"E99.bottom"),sQuery(id+"F0.wireOp",EDGE,"E99.top"),sQuery(id+"F0.wireOp",EDGE,"E102.MirrorCS"),sQuery(id+"F0.wireOp",EDGE,"E103"),sQuery(id+"F0.wireOp",EDGE,"E104"),sQuery(id+"F0.wireOp",EDGE,"E105"),sQuery(id+"F0.wireOp",EDGE,"E106"),sQuery(id+"F0.wireOp",EDGE,"E111"),sQuery(id+"F0.wireOp",EDGE,"E112.MirrorCS"),sQuery(id+"F0.wireOp",EDGE,"E113.MirrorCS"),sQuery(id+"F0.wireOp",EDGE,"E114"),sQuery(id+"F0.wireOp",EDGE,"E115"),sQuery(id+"F0.wireOp",EDGE,"E116"),sQuery(id+"F0.wireOp",EDGE,"E117"),sQuery(id+"F0.wireOp",EDGE,"E118"),sQuery(id+"F0.wireOp",EDGE,"E119"),sQuery(id+"F0.wireOp",EDGE,"E120"),sQuery(id+"F0.wireOp",EDGE,"E121"),sQuery(id+"F0.wireOp",EDGE,"E122"),sQuery(id+"F0.wireOp",EDGE,"E123"),sQuery(id+"F0.wireOp",EDGE,"E124"),sQuery(id+"F0.wireOp",EDGE,"E125"),sQuery(id+"F0.wireOp",EDGE,"E126.right"),sQuery(id+"F0.wireOp",EDGE,"E126.left"),sQuery(id+"F0.wireOp",EDGE,"E127"),sQuery(id+"F0.wireOp",EDGE,"E128"),sQuery(id+"F0.wireOp",EDGE,"E129"),sQuery(id+"F0.wireOp",EDGE,"E130")])]});
            var Q6;
            Q6=makeQuery(id+"F8.opPattern","COPY",BODY,{"derivedFrom":makeQuery(id+"F3.opExtrude","SWEPT_BODY",BODY,{"disambiguationData":[OSD([sQuery(id+"F0.wireOp",EDGE,"E99.bottom"),sQuery(id+"F0.wireOp",EDGE,"E99.top"),sQuery(id+"F0.wireOp",EDGE,"E102.MirrorCS"),sQuery(id+"F0.wireOp",EDGE,"E103"),sQuery(id+"F0.wireOp",EDGE,"E104"),sQuery(id+"F0.wireOp",EDGE,"E105"),sQuery(id+"F0.wireOp",EDGE,"E106"),sQuery(id+"F0.wireOp",EDGE,"E111"),sQuery(id+"F0.wireOp",EDGE,"E112.MirrorCS"),sQuery(id+"F0.wireOp",EDGE,"E113.MirrorCS"),sQuery(id+"F0.wireOp",EDGE,"E114"),sQuery(id+"F0.wireOp",EDGE,"E115"),sQuery(id+"F0.wireOp",EDGE,"E116"),sQuery(id+"F0.wireOp",EDGE,"E117"),sQuery(id+"F0.wireOp",EDGE,"E118"),sQuery(id+"F0.wireOp",EDGE,"E119"),sQuery(id+"F0.wireOp",EDGE,"E120"),sQuery(id+"F0.wireOp",EDGE,"E121"),sQuery(id+"F0.wireOp",EDGE,"E122"),sQuery(id+"F0.wireOp",EDGE,"E123"),sQuery(id+"F0.wireOp",EDGE,"E124"),sQuery(id+"F0.wireOp",EDGE,"E125"),sQuery(id+"F0.wireOp",EDGE,"E126.right"),sQuery(id+"F0.wireOp",EDGE,"E126.left"),sQuery(id+"F0.wireOp",EDGE,"E127"),sQuery(id+"F0.wireOp",EDGE,"E128"),sQuery(id+"F0.wireOp",EDGE,"E129"),sQuery(id+"F0.wireOp",EDGE,"E130")])]}),"instanceName":"1"});
            var Q7;
            Q7=makeQuery(id+"F3.opExtrude","SWEPT_BODY",BODY,{"disambiguationData":[OSD([sQuery(id+"F0.wireOp",EDGE,"E99.bottom"),sQuery(id+"F0.wireOp",EDGE,"E99.top"),sQuery(id+"F0.wireOp",EDGE,"E99.left"),sQuery(id+"F0.wireOp",EDGE,"E99.right"),sQuery(id+"F0.wireOp",EDGE,"E100.bottom"),sQuery(id+"F0.wireOp",EDGE,"E100.top"),sQuery(id+"F0.wireOp",EDGE,"E100.left"),sQuery(id+"F0.wireOp",EDGE,"E100.right")])]});
            var Q8;
            Q8=makeQuery(id+"F1.opExtrude","SWEPT_BODY",BODY,{"disambiguationData":[OSD([sQuery(id+"F0.wireOp",EDGE,"E99.bottom"),sQuery(id+"F0.wireOp",EDGE,"E99.top"),sQuery(id+"F0.wireOp",EDGE,"E102.MirrorCS"),sQuery(id+"F0.wireOp",EDGE,"E103"),sQuery(id+"F0.wireOp",EDGE,"E104"),sQuery(id+"F0.wireOp",EDGE,"E105"),sQuery(id+"F0.wireOp",EDGE,"E106"),sQuery(id+"F0.wireOp",EDGE,"E111"),sQuery(id+"F0.wireOp",EDGE,"E112.MirrorCS"),sQuery(id+"F0.wireOp",EDGE,"E113.MirrorCS"),sQuery(id+"F0.wireOp",EDGE,"E114"),sQuery(id+"F0.wireOp",EDGE,"E115"),sQuery(id+"F0.wireOp",EDGE,"E116"),sQuery(id+"F0.wireOp",EDGE,"E117"),sQuery(id+"F0.wireOp",EDGE,"E118"),sQuery(id+"F0.wireOp",EDGE,"E119"),sQuery(id+"F0.wireOp",EDGE,"E120"),sQuery(id+"F0.wireOp",EDGE,"E121"),sQuery(id+"F0.wireOp",EDGE,"E122"),sQuery(id+"F0.wireOp",EDGE,"E123"),sQuery(id+"F0.wireOp",EDGE,"E124"),sQuery(id+"F0.wireOp",EDGE,"E125"),sQuery(id+"F0.wireOp",EDGE,"E126.right"),sQuery(id+"F0.wireOp",EDGE,"E126.left"),sQuery(id+"F0.wireOp",EDGE,"E127"),sQuery(id+"F0.wireOp",EDGE,"E128"),sQuery(id+"F0.wireOp",EDGE,"E129"),sQuery(id+"F0.wireOp",EDGE,"E130")])]});
            var Q9;
            Q9=makeQuery(id+"F1.opExtrude","SWEPT_BODY",BODY,{"disambiguationData":[OSD([sQuery(id+"F0.wireOp",EDGE,"E131.bottom"),sQuery(id+"F0.wireOp",EDGE,"E131.top"),sQuery(id+"F0.wireOp",EDGE,"E134"),sQuery(id+"F0.wireOp",EDGE,"E135"),sQuery(id+"F0.wireOp",EDGE,"E136"),sQuery(id+"F0.wireOp",EDGE,"E137"),sQuery(id+"F0.wireOp",EDGE,"E142"),sQuery(id+"F0.wireOp",EDGE,"E143"),sQuery(id+"F0.wireOp",EDGE,"E144"),sQuery(id+"F0.wireOp",EDGE,"E145")])]});
            var Q10;
            Q10=makeQuery(id+"F1.opExtrude","SWEPT_BODY",BODY,{"disambiguationData":[OSD([sQuery(id+"F0.wireOp",EDGE,"E80.bottom"),sQuery(id+"F0.wireOp",EDGE,"E80.top"),sQuery(id+"F0.wireOp",EDGE,"E83.MirrorCS"),sQuery(id+"F0.wireOp",EDGE,"E84"),sQuery(id+"F0.wireOp",EDGE,"E85"),sQuery(id+"F0.wireOp",EDGE,"E86"),sQuery(id+"F0.wireOp",EDGE,"E87"),sQuery(id+"F0.wireOp",EDGE,"E92"),sQuery(id+"F0.wireOp",EDGE,"E93.MirrorCS"),sQuery(id+"F0.wireOp",EDGE,"E94.MirrorCS"),sQuery(id+"F0.wireOp",EDGE,"E95.MirrorCS"),sQuery(id+"F0.wireOp",EDGE,"E96.MirrorCS"),sQuery(id+"F0.wireOp",EDGE,"E97.MirrorCS"),sQuery(id+"F0.wireOp",EDGE,"E98.MirrorCS")])]});
            var Q11;
            Q11=makeQuery(id+"F3.opExtrude","SWEPT_BODY",BODY,{"disambiguationData":[OSD([sQuery(id+"F0.wireOp",EDGE,"E131.bottom"),sQuery(id+"F0.wireOp",EDGE,"E131.top"),sQuery(id+"F0.wireOp",EDGE,"E134"),sQuery(id+"F0.wireOp",EDGE,"E135"),sQuery(id+"F0.wireOp",EDGE,"E136"),sQuery(id+"F0.wireOp",EDGE,"E137"),sQuery(id+"F0.wireOp",EDGE,"E142"),sQuery(id+"F0.wireOp",EDGE,"E143"),sQuery(id+"F0.wireOp",EDGE,"E144"),sQuery(id+"F0.wireOp",EDGE,"E145")])]});
            var Q12;
            Q12=qCreatedBy(makeId("Top.planeOp"),FACE);
            transform(context, id + "F10", {"entities" : qUnion([Q0, Q1, Q2, Q3, Q4, Q5, Q6, Q7, Q8, Q9, Q10, Q11]), "transformType" : TransformType.TRANSLATION_DISTANCE, "transformDirection" : qUnion([Q12]), "distance" : 5 * mm, "makeCopy" : false});
        }
        {
            var Q0;
            Q0=makeQuery(id+"F1.opExtrude","SWEPT_BODY",BODY,{"disambiguationData":[OSD([sQuery(id+"F0.wireOp",EDGE,"E80.bottom"),sQuery(id+"F0.wireOp",EDGE,"E80.top"),sQuery(id+"F0.wireOp",EDGE,"E83.MirrorCS"),sQuery(id+"F0.wireOp",EDGE,"E84"),sQuery(id+"F0.wireOp",EDGE,"E85"),sQuery(id+"F0.wireOp",EDGE,"E86"),sQuery(id+"F0.wireOp",EDGE,"E87"),sQuery(id+"F0.wireOp",EDGE,"E92"),sQuery(id+"F0.wireOp",EDGE,"E93.MirrorCS"),sQuery(id+"F0.wireOp",EDGE,"E94.MirrorCS"),sQuery(id+"F0.wireOp",EDGE,"E95.MirrorCS"),sQuery(id+"F0.wireOp",EDGE,"E96.MirrorCS"),sQuery(id+"F0.wireOp",EDGE,"E97.MirrorCS"),sQuery(id+"F0.wireOp",EDGE,"E98.MirrorCS")])]});
            var Q1;
            Q1=makeQuery(id+"F3.opExtrude","SWEPT_BODY",BODY,{"disambiguationData":[OSD([sQuery(id+"F0.wireOp",EDGE,"E0.bottom"),sQuery(id+"F0.wireOp",EDGE,"E0.top"),sQuery(id+"F0.wireOp",EDGE,"E3"),sQuery(id+"F0.wireOp",EDGE,"E4"),sQuery(id+"F0.wireOp",EDGE,"E5"),sQuery(id+"F0.wireOp",EDGE,"E6"),sQuery(id+"F0.wireOp",EDGE,"E7"),sQuery(id+"F0.wireOp",EDGE,"E8"),sQuery(id+"F0.wireOp",EDGE,"E9"),sQuery(id+"F0.wireOp",EDGE,"E11"),sQuery(id+"F0.wireOp",EDGE,"E12"),sQuery(id+"F0.wireOp",EDGE,"E13"),sQuery(id+"F0.wireOp",EDGE,"E14"),sQuery(id+"F0.wireOp",EDGE,"E15"),sQuery(id+"F0.wireOp",EDGE,"E16"),sQuery(id+"F0.wireOp",EDGE,"E17"),sQuery(id+"F0.wireOp",EDGE,"E18"),sQuery(id+"F0.wireOp",EDGE,"E19"),sQuery(id+"F0.wireOp",EDGE,"E20"),sQuery(id+"F0.wireOp",EDGE,"E21"),sQuery(id+"F0.wireOp",EDGE,"E22"),sQuery(id+"F0.wireOp",EDGE,"E23"),sQuery(id+"F0.wireOp",EDGE,"E24"),sQuery(id+"F0.wireOp",EDGE,"E25"),sQuery(id+"F0.wireOp",EDGE,"E26"),sQuery(id+"F0.wireOp",EDGE,"E27"),sQuery(id+"F0.wireOp",EDGE,"E28"),sQuery(id+"F0.wireOp",EDGE,"E29"),sQuery(id+"F0.wireOp",EDGE,"E30"),sQuery(id+"F0.wireOp",EDGE,"E31"),sQuery(id+"F0.wireOp",EDGE,"E32"),sQuery(id+"F0.wireOp",EDGE,"E33"),sQuery(id+"F0.wireOp",EDGE,"E34"),sQuery(id+"F0.wireOp",EDGE,"E35"),sQuery(id+"F0.wireOp",EDGE,"E36"),sQuery(id+"F0.wireOp",EDGE,"E37"),sQuery(id+"F0.wireOp",EDGE,"E38"),sQuery(id+"F0.wireOp",EDGE,"E39"),sQuery(id+"F0.wireOp",EDGE,"E40"),sQuery(id+"F0.wireOp",EDGE,"E41"),sQuery(id+"F0.wireOp",EDGE,"E42"),sQuery(id+"F0.wireOp",EDGE,"E43"),sQuery(id+"F0.wireOp",EDGE,"E44"),sQuery(id+"F0.wireOp",EDGE,"E45"),sQuery(id+"F0.wireOp",EDGE,"E46"),sQuery(id+"F0.wireOp",EDGE,"E47"),sQuery(id+"F0.wireOp",EDGE,"E48"),sQuery(id+"F0.wireOp",EDGE,"E49"),sQuery(id+"F0.wireOp",EDGE,"E50"),sQuery(id+"F0.wireOp",EDGE,"E51"),sQuery(id+"F0.wireOp",EDGE,"E52"),sQuery(id+"F0.wireOp",EDGE,"E53"),sQuery(id+"F0.wireOp",EDGE,"E54"),sQuery(id+"F0.wireOp",EDGE,"E55"),sQuery(id+"F0.wireOp",EDGE,"E56"),sQuery(id+"F0.wireOp",EDGE,"E57"),sQuery(id+"F0.wireOp",EDGE,"E58"),sQuery(id+"F0.wireOp",EDGE,"E59"),sQuery(id+"F0.wireOp",EDGE,"E60"),sQuery(id+"F0.wireOp",EDGE,"E61"),sQuery(id+"F0.wireOp",EDGE,"E62"),sQuery(id+"F0.wireOp",EDGE,"E63"),sQuery(id+"F0.wireOp",EDGE,"E64"),sQuery(id+"F0.wireOp",EDGE,"E65"),sQuery(id+"F0.wireOp",EDGE,"E66"),sQuery(id+"F0.wireOp",EDGE,"E67"),sQuery(id+"F0.wireOp",EDGE,"E68"),sQuery(id+"F0.wireOp",EDGE,"E69"),sQuery(id+"F0.wireOp",EDGE,"E70.MirrorCS"),sQuery(id+"F0.wireOp",EDGE,"E71.MirrorCS"),sQuery(id+"F0.wireOp",EDGE,"E72"),sQuery(id+"F0.wireOp",EDGE,"E73"),sQuery(id+"F0.wireOp",EDGE,"E74"),sQuery(id+"F0.wireOp",EDGE,"E75")])]});
            var Q2;
            Q2=makeQuery(id+"F3.opExtrude","SWEPT_BODY",BODY,{"disambiguationData":[OSD([sQuery(id+"F0.wireOp",EDGE,"E131.bottom"),sQuery(id+"F0.wireOp",EDGE,"E131.top"),sQuery(id+"F0.wireOp",EDGE,"E134"),sQuery(id+"F0.wireOp",EDGE,"E135"),sQuery(id+"F0.wireOp",EDGE,"E136"),sQuery(id+"F0.wireOp",EDGE,"E137"),sQuery(id+"F0.wireOp",EDGE,"E142"),sQuery(id+"F0.wireOp",EDGE,"E143"),sQuery(id+"F0.wireOp",EDGE,"E144"),sQuery(id+"F0.wireOp",EDGE,"E145")])]});
            var Q3;
            Q3=makeQuery(id+"F8.opPattern","COPY",BODY,{"derivedFrom":makeQuery(id+"F1.opExtrude","SWEPT_BODY",BODY,{"disambiguationData":[OSD([sQuery(id+"F0.wireOp",EDGE,"E99.bottom"),sQuery(id+"F0.wireOp",EDGE,"E99.top"),sQuery(id+"F0.wireOp",EDGE,"E102.MirrorCS"),sQuery(id+"F0.wireOp",EDGE,"E103"),sQuery(id+"F0.wireOp",EDGE,"E104"),sQuery(id+"F0.wireOp",EDGE,"E105"),sQuery(id+"F0.wireOp",EDGE,"E106"),sQuery(id+"F0.wireOp",EDGE,"E111"),sQuery(id+"F0.wireOp",EDGE,"E112.MirrorCS"),sQuery(id+"F0.wireOp",EDGE,"E113.MirrorCS"),sQuery(id+"F0.wireOp",EDGE,"E114"),sQuery(id+"F0.wireOp",EDGE,"E115"),sQuery(id+"F0.wireOp",EDGE,"E116"),sQuery(id+"F0.wireOp",EDGE,"E117"),sQuery(id+"F0.wireOp",EDGE,"E118"),sQuery(id+"F0.wireOp",EDGE,"E119"),sQuery(id+"F0.wireOp",EDGE,"E120"),sQuery(id+"F0.wireOp",EDGE,"E121"),sQuery(id+"F0.wireOp",EDGE,"E122"),sQuery(id+"F0.wireOp",EDGE,"E123"),sQuery(id+"F0.wireOp",EDGE,"E124"),sQuery(id+"F0.wireOp",EDGE,"E125"),sQuery(id+"F0.wireOp",EDGE,"E126.right"),sQuery(id+"F0.wireOp",EDGE,"E126.left"),sQuery(id+"F0.wireOp",EDGE,"E127"),sQuery(id+"F0.wireOp",EDGE,"E128"),sQuery(id+"F0.wireOp",EDGE,"E129"),sQuery(id+"F0.wireOp",EDGE,"E130")])]}),"instanceName":"1"});
            var Q4;
            Q4=makeQuery(id+"F8.opPattern","COPY",BODY,{"derivedFrom":makeQuery(id+"F3.opExtrude","SWEPT_BODY",BODY,{"disambiguationData":[OSD([sQuery(id+"F0.wireOp",EDGE,"E99.bottom"),sQuery(id+"F0.wireOp",EDGE,"E99.top"),sQuery(id+"F0.wireOp",EDGE,"E102.MirrorCS"),sQuery(id+"F0.wireOp",EDGE,"E103"),sQuery(id+"F0.wireOp",EDGE,"E104"),sQuery(id+"F0.wireOp",EDGE,"E105"),sQuery(id+"F0.wireOp",EDGE,"E106"),sQuery(id+"F0.wireOp",EDGE,"E111"),sQuery(id+"F0.wireOp",EDGE,"E112.MirrorCS"),sQuery(id+"F0.wireOp",EDGE,"E113.MirrorCS"),sQuery(id+"F0.wireOp",EDGE,"E114"),sQuery(id+"F0.wireOp",EDGE,"E115"),sQuery(id+"F0.wireOp",EDGE,"E116"),sQuery(id+"F0.wireOp",EDGE,"E117"),sQuery(id+"F0.wireOp",EDGE,"E118"),sQuery(id+"F0.wireOp",EDGE,"E119"),sQuery(id+"F0.wireOp",EDGE,"E120"),sQuery(id+"F0.wireOp",EDGE,"E121"),sQuery(id+"F0.wireOp",EDGE,"E122"),sQuery(id+"F0.wireOp",EDGE,"E123"),sQuery(id+"F0.wireOp",EDGE,"E124"),sQuery(id+"F0.wireOp",EDGE,"E125"),sQuery(id+"F0.wireOp",EDGE,"E126.right"),sQuery(id+"F0.wireOp",EDGE,"E126.left"),sQuery(id+"F0.wireOp",EDGE,"E127"),sQuery(id+"F0.wireOp",EDGE,"E128"),sQuery(id+"F0.wireOp",EDGE,"E129"),sQuery(id+"F0.wireOp",EDGE,"E130")])]}),"instanceName":"1"});
            var Q5;
            Q5=sQuery(id+"F0.wireOp",VERTEX,"E39.start");
            transform(context, id + "F11", {"entities" : qUnion([Q0, Q1, Q2, Q3, Q4]), "transformType" : TransformType.SCALE_UNIFORMLY, "scale" : 0.22, "scalePoint" : qUnion([Q5]), "makeCopy" : false});
        }
        {
            var Q0;
            Q0=makeQuery(id+"F7.opPattern","COPY",EDGE,{"derivedFrom":makeQuery(id+"F2.opExtrude","CAP_EDGE",EDGE,{"disambiguationData":[OSD([sQuery(id+"F0.wireOp",EDGE,"E89.MirrorC")])],"isStart":false}),"instanceName":"1"});
            var Q1;
            Q1=makeQuery(id+"F7.opPattern","COPY",EDGE,{"derivedFrom":makeQuery(id+"F2.opExtrude","CAP_EDGE",EDGE,{"disambiguationData":[OSD([sQuery(id+"F0.wireOp",EDGE,"E88")])],"isStart":false}),"instanceName":"1"});
            var Q2;
            Q2=makeQuery(id+"F8.opPattern","COPY",EDGE,{"derivedFrom":makeQuery(id+"F2.opExtrude","CAP_EDGE",EDGE,{"disambiguationData":[OSD([sQuery(id+"F0.wireOp",EDGE,"E108.MirrorC")])],"isStart":false}),"instanceName":"1"});
            var Q3;
            Q3=makeQuery(id+"F8.opPattern","COPY",EDGE,{"derivedFrom":makeQuery(id+"F2.opExtrude","CAP_EDGE",EDGE,{"disambiguationData":[OSD([sQuery(id+"F0.wireOp",EDGE,"E107")])],"isStart":false}),"instanceName":"1"});
            var Q4;
            Q4=makeQuery(id+"F2.opExtrude","CAP_EDGE",EDGE,{"disambiguationData":[OSD([sQuery(id+"F0.wireOp",EDGE,"E107")])],"isStart":false});
            var Q5;
            Q5=makeQuery(id+"F2.opExtrude","CAP_EDGE",EDGE,{"disambiguationData":[OSD([sQuery(id+"F0.wireOp",EDGE,"E108.MirrorC")])],"isStart":false});
            var Q6;
            Q6=makeQuery(id+"F2.opExtrude","CAP_EDGE",EDGE,{"disambiguationData":[OSD([sQuery(id+"F0.wireOp",EDGE,"E88")])],"isStart":false});
            var Q7;
            Q7=makeQuery(id+"F2.opExtrude","CAP_EDGE",EDGE,{"disambiguationData":[OSD([sQuery(id+"F0.wireOp",EDGE,"E89.MirrorC")])],"isStart":false});
            var Q8;
            Q8=makeQuery(id+"F2.opExtrude","CAP_EDGE",EDGE,{"disambiguationData":[OSD([sQuery(id+"F0.wireOp",EDGE,"E76")])],"isStart":false});
            var Q9;
            Q9=makeQuery(id+"F2.opExtrude","CAP_EDGE",EDGE,{"disambiguationData":[OSD([sQuery(id+"F0.wireOp",EDGE,"E77.MirrorC")])],"isStart":false});
            var Q10;
            Q10=makeQuery(id+"F6.opPattern","COPY",EDGE,{"derivedFrom":makeQuery(id+"F2.opExtrude","CAP_EDGE",EDGE,{"disambiguationData":[OSD([sQuery(id+"F0.wireOp",EDGE,"E77.MirrorC")])],"isStart":false}),"instanceName":"1"});
            var Q11;
            Q11=makeQuery(id+"F6.opPattern","COPY",EDGE,{"derivedFrom":makeQuery(id+"F2.opExtrude","CAP_EDGE",EDGE,{"disambiguationData":[OSD([sQuery(id+"F0.wireOp",EDGE,"E76")])],"isStart":false}),"instanceName":"1"});
            var Q12;
            Q12=makeQuery(id+"F2.opExtrude","CAP_EDGE",EDGE,{"disambiguationData":[OSD([sQuery(id+"F0.wireOp",EDGE,"E138")])],"isStart":false});
            var Q13;
            Q13=makeQuery(id+"F2.opExtrude","CAP_EDGE",EDGE,{"disambiguationData":[OSD([sQuery(id+"F0.wireOp",EDGE,"E139.MirrorC")])],"isStart":false});
            var Q14;
            Q14=makeQuery(id+"F9.opPattern","COPY",EDGE,{"derivedFrom":makeQuery(id+"F2.opExtrude","CAP_EDGE",EDGE,{"disambiguationData":[OSD([sQuery(id+"F0.wireOp",EDGE,"E139.MirrorC")])],"isStart":false}),"instanceName":"1"});
            var Q15;
            Q15=makeQuery(id+"F9.opPattern","COPY",EDGE,{"derivedFrom":makeQuery(id+"F2.opExtrude","CAP_EDGE",EDGE,{"disambiguationData":[OSD([sQuery(id+"F0.wireOp",EDGE,"E138")])],"isStart":false}),"instanceName":"1"});
            fillet(context, id + "F12", {"entities" : qUnion([Q0, Q1, Q2, Q3, Q4, Q5, Q6, Q7, Q8, Q9, Q10, Q11, Q12, Q13, Q14, Q15]), "radius" : .82 * mm, "tangentPropagation" : true, "allowEdgeOverflow" : false});
        }
    });
